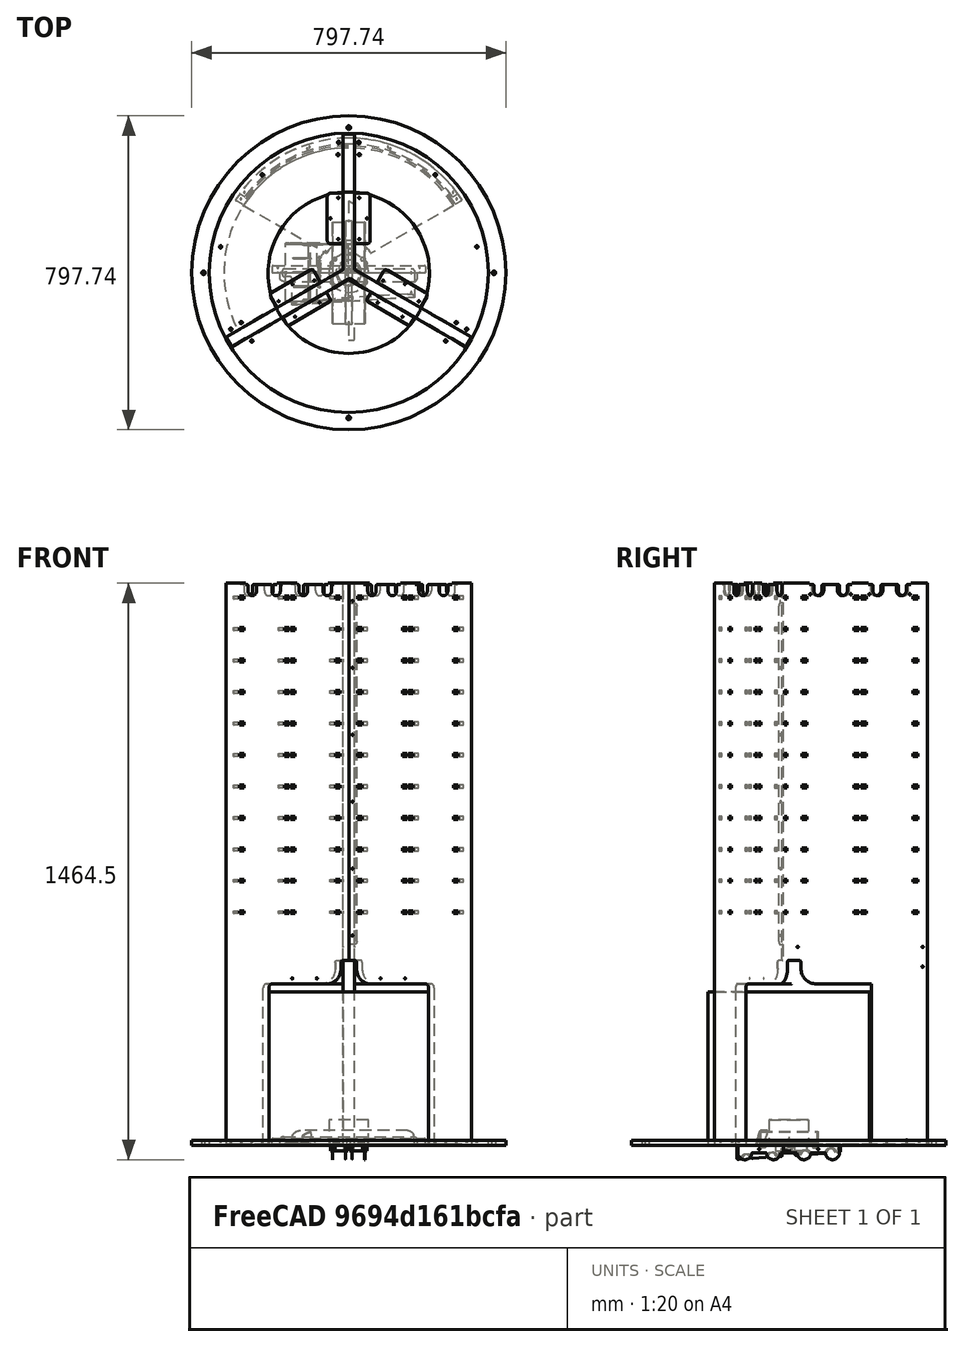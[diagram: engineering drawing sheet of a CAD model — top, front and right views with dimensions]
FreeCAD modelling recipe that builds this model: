
FCSTD DOCUMENT  (FreeCAD 0.21R32532 (Git))
Label: composit_full_size
License: All rights reserved
LicenseURL: http://en.wikipedia.org/wiki/All_rights_reserved
objects: Sketcher::SketchObject×64, PartDesign::Pocket×50, PartDesign::CoordinateSystem×29, PartDesign::Mirrored×20, PartDesign::Body×18, PartDesign::PolarPattern×17, PartDesign::Plane×14, PartDesign::SubShapeBinder×14, PartDesign::FeaturePython×12, PartDesign::Pad×11, PartDesign::MultiTransform×11, PartDesign::LinearPattern×7, Spreadsheet::Sheet×5, PartDesign::Line×4, App::DocumentObjectGroup×2, PartDesign::Fillet×2, Part::Feature×1, PartDesign::FeatureBase×1, PartDesign::Point×1, PartDesign::ShapeBinder×1, +2 more types
note: 344 computed .brp shape members not serialized (recipe doc carries the construction recipe); baked Part::Feature solids carry a one-line shape summary decoded from their .brp
EXTERNAL_REF file=composit_stand2_reserve.FCStd obj=Body_2

FEATURE [Sketcher::SketchObject] Sketch
  FullyConstrained = true
  MapMode = 5
  Support = -> [XY_Plane]
  expr: Constraints[29] = <<main>>.end_face_width
  expr: Constraints[32] = <<main>>.work_plane_width
  sketch-geometry (18):
    g0: LineSegment StartX=14.5 StartY=8.37158 StartZ=0 EndX=-14.5 EndY=8.37158 EndZ=0
    g1: LineSegment StartX=-14.5 StartY=8.37158 StartZ=0 EndX=-14.5 EndY=351.872 EndZ=0
    g2: LineSegment StartX=-14.5 StartY=351.872 StartZ=0 EndX=14.5 EndY=351.872 EndZ=0
    g3: LineSegment StartX=14.5 StartY=351.872 StartZ=0 EndX=14.5 EndY=8.37158 EndZ=0
    g4: LineSegment StartX=-14.5 StartY=8.37158 StartZ=0 EndX=-311.98 EndY=-163.378 EndZ=0
    g5: LineSegment StartX=-311.98 StartY=-163.378 StartZ=0 EndX=-297.48 EndY=-188.493 EndZ=0
    g6: LineSegment StartX=-297.48 StartY=-188.493 StartZ=0 EndX=3 EndY=-15.0111 EndZ=0
    g7: LineSegment StartX=0 StartY=-16.7432 StartZ=0 EndX=-14.5 EndY=8.37158 EndZ=0
    g8: LineSegment StartX=14.5 StartY=8.37158 StartZ=0 EndX=311.98 EndY=-163.378 EndZ=0
    g9: LineSegment StartX=311.98 StartY=-163.378 StartZ=0 EndX=297.48 EndY=-188.493 EndZ=0
    g10: LineSegment StartX=0 StartY=-16.7432 StartZ=0 EndX=14.5 EndY=8.37158 EndZ=0
    g11: LineSegment StartX=-14.5 StartY=8.37158 StartZ=0 EndX=0 EndY=0 EndZ=0
    g12: LineSegment StartX=0 StartY=0 StartZ=0 EndX=0 EndY=-16.7432 EndZ=0
    g13: LineSegment StartX=0 StartY=0 StartZ=0 EndX=14.5 EndY=8.37158 EndZ=0
    g14: LineSegment StartX=297.48 StartY=-188.493 StartZ=0 EndX=0.216506 EndY=-16.8682 EndZ=0
    g15: LineSegment StartX=0.216506 StartY=-16.8682 StartZ=0 EndX=0 EndY=-16.7432 EndZ=0
    g16: LineSegment StartX=3 StartY=-15.0111 StartZ=0 EndX=20.3205 EndY=-25.0111 EndZ=0
    g17: LineSegment StartX=0 StartY=0 StartZ=0 EndX=-5.75 EndY=-9.95929 EndZ=0
  constraints (54):
    c: Coincident(g0,g1)
    c: Coincident(g1,g2)
    c: Coincident(g2,g3)
    c: Coincident(g3,g0)
    c: Horizontal(g0)
    c: Horizontal(g2)
    c: Vertical(g1)
    c: Vertical(g3)
    c: Coincident(g4,g5)
    c: Coincident(g7,g4)
    c: Parallel(g4,g6)
    c: Parallel(g5,g7)
    c: Coincident(g8,g9)
    c: Coincident(g9,g14)
    c: Coincident(g15,g10)
    c: Coincident(g10,g8)
    c: Perpendicular(g5,g4)
    c: Coincident(g4,g0)
    c: Coincident(g8,g0)
    c: Parallel(g10,g9)
    c: Perpendicular(g8,g10)
    c: Equal(g7,g10)
    c: Equal(g10,g0)
    c: Coincident(g11,g1)
    c: Coincident(g11,g-1)
    c: Coincident(g12,g11)
    c: Coincident(g13,g11)
    c: Coincident(g13,g3)
    c: Equal(g12,g13)
    c: DistanceX(g2,g2) = 29
    c: Equal(g4,g1)
    c: DistanceY(g12,g12) = 16.7432  'petal_connection_distance'
    c: DistanceY(g3,g3) = 343.5
    c: DistanceY(g3) = 8.37158  'petal_offset'
    c: Distance(g2,g11) = 352.17  'max_r'
    c: Coincident(g14,g15)
    c: Parallel(g14,g8)
    c: Parallel(g15,g8)
    c: Equal(g8,g3)
    c: Distance(g14,g15) = 0.25
    c: Coincident(g7,g12)
    c: Coincident(g15,g7)
    c: PointOnObject(g15,g-2)
    c: Coincident(g6,g5)
    c: PointOnObject(g7,g6)
    c: Distance(g6,g14) = 3
    c: Coincident(g16,g6)
    c: Parallel(g16,g14)
    c: Distance(g16) = 20
    c: Coincident(g17,g11)
    c: Perpendicular(g17,g16)
    c: PointOnObject(g17,g16)
    c: Distance(g16,g17) = 30.1036  'overlap_from_origin'
    c: Distance(g6,g7) = 3.4641  'overlap_proj_thickness'
FEATURE [PartDesign::FeaturePython] BaseBend  # WARN: FeaturePython — macro-defined, semantics opaque (R4)
  BendSide = 0
  BendSketch = -> Sketch
  MidPlane = false
  Reverse = false
  length = 1428
  radius = 0.1
  thickness = 0.3
  expr: length = <<main>>.total_length
  expr: radius = <<main>>.bend_r
  expr: thickness = 0.3
FEATURE [Spreadsheet::Sheet] Spreadsheet  label="module"
  cells = B2(module_width)==148 mm; B3(module_height)==160 mm; B4(module_fixture_distance_x)==132 mm; C4(module_fixture_distance_y)==80 mm; B5(module_hole_x)==13 mm; B6(module_hole_y)==7 mm
FEATURE [Spreadsheet::Sheet] Spreadsheet001  label="main"
  cells = B2(work_plane_width)==27.5 mm + <<module>>.module_width * 2 + 20 mm; C2(modules_center_offset)==<<module>>.module_width + 25 mm; D2(rivet_d)==3.4 mm; E2(pillar_offset)==398 mm; F2(plexiglass_shield_bottom_offset)==471 mm; B3(work_plane_height)==basin_height + <<module>>.module_fixture_distance_y * number_of_modules + <<module>>.module_height; C3(work_plane_height_middle)==basin_height + work_plane_height / 2; D3(planes_fix_holes_distance)==130 mm; B4(end_face_width)==29 mm; C4(inner_width)==end_face_width - thickness * 2; D4(gutter_fix_holes_distance)==51 mm; B5(basin_height)==410 mm; B6(thickness)==3 mm; C6(al_thickness)==0.3 mm; D6(number_of_modules)=11; E6(modules_array_height)==<<module>>.module_height + (number_of_modules - 1) * <<module>>.module_fixture_distance_y; F6(distance_farest_droppers)==<<dropper>>.distance_between_droppers2 + <<dropper>>.d + 20 mm + modules_offset_x; B7(total_length)==basin_height + distance_basin_cutout_modules_bottom + modules_array_height + distance_gutter_holes_modules_top + distance_gutter_holes_dropper_cutout + <<dropper>>.center_height_offset; D7(distance_basin_cutout_modules_bottom)==22 mm; B8(bend_r)==0.1 mm; D8(distance_gutter_holes_modules_top)==8 mm; B9(module_distance_x)==2 mm; D9(distance_gutter_holes_dropper_cutout)==9 mm; B10(modules_offset_x)==<<module>>.module_width + module_distance_x; D10(modules_centres_dictance_x)==module_distance_x + <<module>>.module_width; B11(plexiglass_offset)==10 mm; D11(leg_width)==110 mm
FEATURE [Spreadsheet::Sheet] Spreadsheet002  label="dropper"
  cells = B2(d)==23.25 mm; B3(fixture_d)=; B4(center_height_offset)==19 mm; B5(distance_between_droppers1)==60 mm; C5(distance_between_droppers2)==70 mm
FEATURE [Spreadsheet::Sheet] Spreadsheet003  label="gutter"
  cells = B2(length)==300 mm; C2(plane_middle)==60 mm; B3(bend_angle)==4 °; B4(high_edge_length)==30 mm; B5(low_edge_length)==20 mm
FEATURE [Part::Feature] Part__Feature  label="module002"
  shape: bbox 170 x 148 x 41.12 mm, 715 faces (baked)
FEATURE [PartDesign::CoordinateSystem] LCS_0
  AttacherType = Attacher::AttachEngine3D
  MapMode = 2
  Support = -> [X_Axis001]
FEATURE [PartDesign::FeatureBase] BaseFeature
  BaseFeature = -> Part__Feature
  Placement = pos=(2e-15,0.749157,-0.233873) rot=(0,0,1;0rad)
FEATURE [PartDesign::Line] DatumLine
  AttacherType = Attacher::AttachEngineLine
  Length = 20
  MapMode = 29
  Placement = pos=(2e-15,0.749157,-0.233873) rot=(0,0.707107,0.707107;3.14159rad)
  ResizeMode = 0
  Support = -> [BaseFeature]
FEATURE [PartDesign::Body] module_body
  BaseFeature = -> Part__Feature
  Group = -> [BaseFeature,LCS_0,DatumLine]
  Origin = -> Origin001
  Tip = -> BaseFeature
FEATURE [Sketcher::SketchObject] Sketch002  label="cover_holder_corner"
  FullyConstrained = true
  MapMode = 5
  Placement = pos=(0,0,0) rot=(0.57735,0.57735,0.57735;2.0944rad)
  Support = -> [YZ_Plane]
  expr: Constraints[8] = <<main>>.basin_height
  sketch-geometry (4):
    g0: LineSegment StartX=71 StartY=360 StartZ=0 EndX=71 EndY=410 EndZ=0
    g1: LineSegment StartX=71 StartY=410 StartZ=0 EndX=205 EndY=410 EndZ=0
    g2: LineSegment StartX=205 StartY=410 StartZ=0 EndX=205 EndY=360 EndZ=0
    g3: LineSegment StartX=205 StartY=360 StartZ=0 EndX=71 EndY=360 EndZ=0
  constraints (13):
    c: Coincident(g0,g1)
    c: Coincident(g1,g2)
    c: Coincident(g2,g3)
    c: Coincident(g3,g0)
    c: Horizontal(g1)
    c: Horizontal(g3)
    c: Vertical(g0)
    c: Vertical(g2)
    c: DistanceY(g1) = 410
    c: DistanceY(g2,g2) = 50
    c: DistanceX(g0) = 71  'offset'
    c: DistanceX(g1) = 205
    c: DistanceX(g3,g3) = 134  'length'
FEATURE [PartDesign::Pocket] Pocket001
  BaseFeature = -> BaseBend
  Direction = (-1,2e-16,-3e-16)
  Length = 29
  Length2 = 5
  Midplane = true
  Profile = -> Sketch002
  ReferenceAxis = -> Sketch002 [N_Axis]
  Type = 0
  expr: Length = <<main>>.end_face_width
FEATURE [PartDesign::PolarPattern] PolarPattern
  Angle = 360
  Axis = -> Z_Axis
  BaseFeature = -> Pocket001
  Occurrences = 3
  Originals = -> [Pocket001]
  Refine = true
FEATURE [PartDesign::Point] DatumPoint
  AttacherType = Attacher::AttachEnginePoint
  AttachmentOffset = pos=(0,8.37158,0) rot=(0,0,1;0rad)
  MapMode = 32
  Placement = pos=(0,8.37158,0) rot=(0,0,1;0rad)
  Support = -> [XY_Plane]
  expr: .AttachmentOffset.Base.y = Sketch.Constraints.petal_offset
FEATURE [PartDesign::CoordinateSystem] Local_CS
  AttacherType = Attacher::AttachEngine3D
  AttachmentOffset = pos=(0,173,0) rot=(0,0,1;0rad)
  MapMode = 1
  Placement = pos=(0,181.372,0) rot=(0,0,1;0rad)
  Support = -> [DatumPoint]
  expr: .AttachmentOffset.Base.y = <<module>>.module_width + 25 mm
FEATURE [PartDesign::CoordinateSystem] Local_CS001
  AttacherType = Attacher::AttachEngine3D
  AttachmentOffset = pos=(0,0,410) rot=(0,0,1;0rad)
  MapMode = 5
  Placement = pos=(0,181.372,410) rot=(0,0,1;0rad)
  Support = -> [Local_CS]
  expr: .AttachmentOffset.Base.z = <<main>>.basin_height
FEATURE [PartDesign::Plane] DatumPlane
  Length = 717.412
  MapMode = 4
  Placement = pos=(0,181.372,410) rot=(0.57735,0.57735,0.57735;2.0944rad)
  ResizeMode = 0
  Support = -> [Local_CS001]
  Width = 1630.19
FEATURE [PartDesign::PolarPattern] PolarPattern001
  Angle = 360
  Axis = -> Z_Axis
  Occurrences = 3
FEATURE [PartDesign::CoordinateSystem] Local_CS002
  AttacherType = Attacher::AttachEngine3D
  AttachmentOffset = pos=(0,0,1428) rot=(0,0,1;0rad)
  MapMode = 5
  Placement = pos=(0,181.372,1428) rot=(0,0,1;0rad)
  Support = -> [Local_CS]
  expr: .AttachmentOffset.Base.z = <<main>>.total_length
FEATURE [PartDesign::CoordinateSystem] Local_CS003
  AttacherType = Attacher::AttachEngine3D
  AttachmentOffset = pos=(0,-75,0) rot=(0,0,1;0rad)
  MapMode = 5
  Placement = pos=(0,106.372,1428) rot=(0,0,1;0rad)
  Support = -> [Local_CS002]
  expr: .AttachmentOffset.Base.y = -<<main>>.module_distance_x / 2 - <<module>>.module_width / 2
FEATURE [PartDesign::Plane] DatumPlane001
  Length = 814.054
  MapMode = 3
  Placement = pos=(0,106.372,1428) rot=(1,0,0;1.5708rad)
  ResizeMode = 0
  Support = -> [Local_CS003]
  Width = 1643.39
FEATURE [PartDesign::Plane] DatumPlane002
  Length = 814.054
  MapMode = 3
  Placement = pos=(0,181.372,1428) rot=(1,0,0;1.5708rad)
  ResizeMode = 0
  Support = -> [Local_CS002]
  Width = 1643.39
FEATURE [PartDesign::Plane] DatumPlane003
  Length = 717.412
  MapMode = 4
  Placement = pos=(0,106.372,1428) rot=(0.57735,0.57735,0.57735;2.0944rad)
  ResizeMode = 0
  Support = -> [Local_CS003]
  Width = 1630.19
FEATURE [Sketcher::SketchObject] Sketch003
  AttachmentOffset = pos=(-66,-36,0) rot=(0,0,1;0rad)
  FullyConstrained = true
  MapMode = 5
  Placement = pos=(0,40.3716,1392) rot=(0.57735,0.57735,0.57735;2.0944rad)
  Support = -> [DatumPlane003]
  expr: .AttachmentOffset.Base.x = -<<module>>.module_fixture_distance_x / 2
  expr: .AttachmentOffset.Base.y = Sketch005.AttachmentOffset.Base.y - <<main>>.distance_gutter_holes_modules_top
  expr: Constraints[10] = <<module>>.module_hole_x
  expr: Constraints[11] = <<module>>.module_hole_y
  sketch-geometry (5):
    g0: LineSegment StartX=-6.5 StartY=-3.5 StartZ=0 EndX=-6.5 EndY=3.5 EndZ=0
    g1: LineSegment StartX=-6.5 StartY=3.5 StartZ=0 EndX=6.5 EndY=3.5 EndZ=0
    g2: LineSegment StartX=6.5 StartY=3.5 StartZ=0 EndX=6.5 EndY=-3.5 EndZ=0
    g3: LineSegment StartX=6.5 StartY=-3.5 StartZ=0 EndX=-6.5 EndY=-3.5 EndZ=0
    g4: GeomPoint X=0 Y=0 Z=0
  constraints (12):
    c: Coincident(g0,g1)
    c: Coincident(g1,g2)
    c: Coincident(g2,g3)
    c: Coincident(g3,g0)
    c: Horizontal(g1)
    c: Horizontal(g3)
    c: Vertical(g0)
    c: Vertical(g2)
    c: Symmetric(g1,g0,g4)
    c: Coincident(g4,g-1)
    c: DistanceX(g1,g1) = 13
    c: DistanceY(g2,g2) = 7
FEATURE [PartDesign::LinearPattern] LinearPattern
  Direction = -> Sketch003 [H_Axis]
  Length = 132
  Occurrences = 2
  expr: Length = <<module>>.module_fixture_distance_x
FEATURE [PartDesign::LinearPattern] LinearPattern001
  Direction = -> Sketch003 [H_Axis]
  Length = 150
  Occurrences = 2
  expr: Length = <<module>>.module_width + <<main>>.module_distance_x
FEATURE [PartDesign::LinearPattern] LinearPattern002
  Direction = -> Sketch003 [V_Axis]
  Length = 800
  Occurrences = 11
  Reversed = true
  expr: Length = <<module>>.module_fixture_distance_y * (Occurrences - 1)
  expr: Occurrences = <<main>>.number_of_modules
FEATURE [Sketcher::SketchObject] Sketch004
  AttachmentOffset = pos=(-35,-19,0) rot=(0,0,1;0rad)
  FullyConstrained = true
  MapMode = 5
  Placement = pos=(0,71.3716,1409) rot=(0.57735,0.57735,0.57735;2.0944rad)
  Support = -> [DatumPlane003]
  expr: .AttachmentOffset.Base.x = -<<dropper>>.distance_between_droppers2 / 2
  expr: .AttachmentOffset.Base.y = -<<dropper>>.center_height_offset
  expr: .Constraints.d = <<dropper>>.d + 2 mm
  expr: Constraints[10] = <<dropper>>.center_height_offset
  sketch-geometry (4):
    g0: ArcOfCircle CenterX=0 CenterY=0 CenterZ=0 NormalX=0 NormalY=0 NormalZ=1 AngleXU=0 Radius=12.625 StartAngle=3.14159 EndAngle=6.28319
    g1: LineSegment StartX=-12.625 StartY=19 StartZ=0 EndX=-12.625 EndY=0 EndZ=0
    g2: LineSegment StartX=12.625 StartY=-3.1e-15 StartZ=0 EndX=12.625 EndY=19 EndZ=0
    g3: LineSegment StartX=-12.625 StartY=19 StartZ=0 EndX=12.625 EndY=19 EndZ=0
  constraints (11):
    c: PointOnObject(g0,g-2)
    c: Tangent(g2,g0) = -1.5708
    c: Tangent(g1,g0) = -1.5708
    c: Vertical(g2)
    c: Vertical(g1)
    c: Horizontal(g3)
    c: PointOnObject(g0,g-1)
    c: Diameter(g0) = 25.25  'd'
    c: Coincident(g1,g3)
    c: Coincident(g2,g3)
    c: DistanceY(g2) = 19
FEATURE [PartDesign::SubShapeBinder] Binder
  BindCopyOnChange = 0
  BindMode = 0
  ClaimChildren = false
  Context = -> Body [Binder.]
  Fuse = false
  MakeFace = true
  OffsetFill = false
  OffsetIntersection = false
  OffsetJoinType = 0
  OffsetOpenResult = false
  PartialLoad = false
  Placement = pos=(0,5,0) rot=(0,0,1;0rad)
  Relative = true
  Support = -> [Sketch004]
  _Version = 2
  expr: .Placement.Base.y = (<<dropper>>.distance_between_droppers2 - <<dropper>>.distance_between_droppers1) / 2
FEATURE [PartDesign::Mirrored] Mirrored
  MirrorPlane = -> DatumPlane001
FEATURE [PartDesign::Mirrored] Mirrored001
  MirrorPlane = -> DatumPlane002
FEATURE [PartDesign::PolarPattern] PolarPattern002
  Angle = 360
  Axis = -> Z_Axis
  Occurrences = 3
FEATURE [Sketcher::SketchObject] Sketch007
  AttachmentOffset = pos=(-35,-3.5,0) rot=(0,0,1;0rad)
  FullyConstrained = true
  MapMode = 5
  Placement = pos=(0,71.3716,1424.5) rot=(0.57735,0.57735,0.57735;2.0944rad)
  Support = -> [DatumPlane003]
  expr: .AttachmentOffset.Base.x = Sketch004.AttachmentOffset.Base.x
  expr: .AttachmentOffset.Base.y = -Sketch008.Constraints.height
  expr: Constraints[18] = Sketch004.Constraints.d
  sketch-geometry (8):
    g0: ArcOfCircle CenterX=15.125 CenterY=-2.5 CenterZ=0 NormalX=0 NormalY=0 NormalZ=1 AngleXU=0 Radius=2.5 StartAngle=1.57079 EndAngle=3.14159
    g1: LineSegment StartX=-15.125 StartY=0 StartZ=0 EndX=-12.625 EndY=0 EndZ=0
    g2: LineSegment StartX=-12.625 StartY=-2.5 StartZ=0 EndX=-12.625 EndY=0 EndZ=0
    g3: LineSegment StartX=12.625 StartY=-2.5 StartZ=0 EndX=12.625 EndY=0 EndZ=0
    g4: LineSegment StartX=12.625 StartY=0 StartZ=0 EndX=15.125 EndY=-2.9527e-11 EndZ=0
    g5: LineSegment StartX=-12.625 StartY=0 StartZ=0 EndX=0 EndY=0 EndZ=0
    g6: LineSegment StartX=0 StartY=0 StartZ=0 EndX=12.625 EndY=0 EndZ=0
    g7: ArcOfCircle CenterX=-15.125 CenterY=-2.5 CenterZ=0 NormalX=0 NormalY=0 NormalZ=1 AngleXU=0 Radius=2.5 StartAngle=0 EndAngle=1.5708
  constraints (23):
    c: PointOnObject(g0,g-1)
    c: PointOnObject(g1,g-1)
    c: Coincident(g2,g1)
    c: Coincident(g3,g0)
    c: PointOnObject(g3,g-1)
    c: Vertical(g3)
    c: Tangent(g3,g0)
    c: Coincident(g4,g3)
    c: Coincident(g4,g0)
    c: Tangent(g4,g0)
    c: Vertical(g2)
    c: Diameter(g0) = 5
    c: Coincident(g5,g1)
    c: Horizontal(g5)
    c: Coincident(g6,g5)
    c: Coincident(g6,g3)
    c: Equal(g5,g6)
    c: PointOnObject(g5,g-2)
    c: DistanceX(g1,g3) = 25.25
    c: Horizontal(g1)
    c: Tangent(g7,g1) = 1.5708
    c: Tangent(g7,g2) = -1.5708
    c: Equal(g7,g0)
FEATURE [PartDesign::SubShapeBinder] Binder001
  BindCopyOnChange = 0
  BindMode = 0
  ClaimChildren = false
  Context = -> Body [Binder001.]
  Fuse = false
  MakeFace = true
  OffsetFill = false
  OffsetIntersection = false
  OffsetJoinType = 0
  OffsetOpenResult = false
  PartialLoad = false
  Placement = pos=(0,5,0) rot=(0,0,1;0rad)
  Relative = true
  Support = -> [Sketch007]
  _Version = 2
  expr: .Placement.Base.y = Binder.Placement.Base.y
FEATURE [Sketcher::SketchObject] Sketch008
  FullyConstrained = true
  MapMode = 5
  Placement = pos=(0,106.372,1428) rot=(0.57735,0.57735,0.57735;2.0944rad)
  Support = -> [DatumPlane003]
  expr: Constraints[10] = 108.4 / 2
  sketch-geometry (5):
    g0: LineSegment StartX=0 StartY=0 StartZ=0 EndX=-54.2 EndY=0 EndZ=0
    g1: LineSegment StartX=-54.2 StartY=0 StartZ=0 EndX=-54.2 EndY=-3.5 EndZ=0
    g2: LineSegment StartX=-54.2 StartY=-3.5 StartZ=0 EndX=0 EndY=-3.5 EndZ=0
    g3: LineSegment StartX=0 StartY=-3.5 StartZ=0 EndX=0 EndY=0 EndZ=0
    g4: GeomPoint X=54.2 Y=0 Z=0
  constraints (13):
    c: Coincident(g0,g1)
    c: Coincident(g1,g2)
    c: Coincident(g2,g3)
    c: Coincident(g3,g0)
    c: Horizontal(g0)
    c: Horizontal(g2)
    c: Vertical(g1)
    c: Vertical(g3)
    c: Coincident(g0,g-1)
    c: DistanceY(g1,g1) = 3.5  'height'
    c: DistanceX(g0,g0) = 54.2
    c: Symmetric(g4,g0,g-2)
    c: DistanceX(g0,g4) = 108.4
FEATURE [Sketcher::SketchObject] Sketch009
  FullyConstrained = true
  MapMode = 5
  Placement = pos=(0,0,0) rot=(0,0.707107,0.707107;3.14159rad)
  Support = -> [XZ_Plane003]
  expr: .Constraints.high_side_length = -(<<gutter>>.low_edge_length + <<main>>.distance_farest_droppers * tan(<<gutter>>.bend_angle))
  expr: Constraints[11] = <<main>>.end_face_width - <<main>>.thickness * 4
  sketch-geometry (5):
    g0: LineSegment StartX=-8.5 StartY=-38.4082 StartZ=0 EndX=-8.5 EndY=0 EndZ=0
    g1: LineSegment StartX=-8.5 StartY=0 StartZ=0 EndX=8.5 EndY=0 EndZ=0
    g2: LineSegment StartX=8.5 StartY=0 StartZ=0 EndX=8.5 EndY=-38.4082 EndZ=0
    g3: LineSegment StartX=8.5 StartY=-38.4082 StartZ=0 EndX=-8.5 EndY=-38.4082 EndZ=0
    g4: GeomPoint X=0 Y=-19.2041 Z=0
  constraints (13):
    c: Coincident(g0,g1)
    c: Coincident(g1,g2)
    c: Coincident(g2,g3)
    c: Coincident(g3,g0)
    c: Horizontal(g1)
    c: Horizontal(g3)
    c: Vertical(g0)
    c: Vertical(g2)
    c: Symmetric(g1,g0,g4)
    c: PointOnObject(g4,g-2)
    c: PointOnObject(g1,g-1)
    c: DistanceX(g0,g1) = 17
    c: DistanceY(g2) = -38.4082  'high_side_length'
FEATURE [PartDesign::FeaturePython] BaseBend001  # WARN: FeaturePython — macro-defined, semantics opaque (R4)
  BendSide = 1
  BendSketch = -> Sketch009
  MidPlane = true
  Reverse = false
  length = 263.25
  radius = 0.1
  thickness = 0.3
  expr: length = <<main>>.distance_farest_droppers
  expr: radius = <<main>>.bend_r
  expr: thickness = <<main>>.al_thickness
FEATURE [Sketcher::SketchObject] Sketch010
  AttachmentOffset = pos=(0,-38.4082,0) rot=(0,0,1;0rad)
  FullyConstrained = true
  MapMode = 5
  Placement = pos=(8.5e-15,-8.5e-15,-38.4082) rot=(0.57735,0.57735,0.57735;2.0944rad)
  Support = -> [YZ_Plane003]
  expr: .AttachmentOffset.Base.y = Sketch009.Constraints.high_side_length
  expr: Constraints[12] = <<gutter>>.bend_angle
  expr: Constraints[6] = <<main>>.distance_farest_droppers
  sketch-geometry (10):
    g0: LineSegment StartX=-128.951 StartY=0.187012 StartZ=0 EndX=129.299 EndY=18.2456 EndZ=0
    g1: ArcOfCircle CenterX=-129.125 CenterY=2.68092 CenterZ=0 NormalX=0 NormalY=0 NormalZ=1 AngleXU=0 Radius=2.5 StartAngle=3.14159 EndAngle=4.7822
    g2: LineSegment StartX=131.625 StartY=20.7395 StartZ=0 EndX=131.625 EndY=0 EndZ=0
    g3: LineSegment StartX=-131.625 StartY=0 StartZ=0 EndX=-131.625 EndY=2.68092 EndZ=0
    g4: LineSegment StartX=131.625 StartY=0 StartZ=0 EndX=0 EndY=0 EndZ=0
    g5: LineSegment StartX=0 StartY=0 StartZ=0 EndX=-131.625 EndY=0 EndZ=0
    g6: GeomPoint X=-131.625 Y=0 Z=0
    g7: GeomPoint X=131.625 Y=20.7395 Z=0
    g8: ArcOfCircle CenterX=129.125 CenterY=20.7395 CenterZ=0 NormalX=0 NormalY=0 NormalZ=1 AngleXU=0 Radius=2.5 StartAngle=4.7822 EndAngle=6.28319
    g9: GeomPoint X=131.625 Y=18.4082 Z=0
  constraints (25):
    c: Vertical(g2)
    c: Coincident(g4,g2)
    c: Coincident(g3,g5)
    c: Vertical(g3)
    c: Tangent(g3,g1) = 1.5708
    c: Tangent(g1,g0) = -1.5708
    c: DistanceX(g5,g2) = 263.25
    c: Coincident(g4,g5)
    c: Horizontal(g4)
    c: Horizontal(g5)
    c: Equal(g5,g4)
    c: PointOnObject(g4,g-2)
    c: Angle(g-1,g0) = 0.0698132
    c: PointOnObject(g6,g3)
    c: PointOnObject(g6,g0)
    c: PointOnObject(g6,g-1)
    c: Diameter(g1) = 5
    c: PointOnObject(g4,g-1)
    c: Coincident(g8,g7)
    c: Tangent(g2,g8) = 1.5708
    c: Equal(g8,g1)
    c: Tangent(g8,g0) = -1.5708
    c: PointOnObject(g9,g2)
    c: PointOnObject(g9,g0)
    c: DistanceY(g9) = 18.4082
FEATURE [PartDesign::Pocket] Pocket009
  BaseFeature = -> BaseBend001
  Direction = (-1,2e-16,-3e-16)
  Length = 5
  Length2 = 5
  Midplane = true
  Profile = -> Sketch010
  ReferenceAxis = -> Sketch010 [N_Axis]
  Type = 1
FEATURE [PartDesign::CoordinateSystem] Local_CS005
  AttacherType = Attacher::AttachEngine3D
  AttachmentOffset = pos=(0,0,-29.2041) rot=(1,0,0;0.069813rad)
  MapMode = 5
  Placement = pos=(0,0,-29.2041) rot=(1,0,0;0.069813rad)
  Support = -> [XY_Plane003]
  expr: .AttachmentOffset.Base.z = (Sketch009.Constraints.high_side_length + <<gutter>>.low_edge_length) / 2 - <<gutter>>.low_edge_length
  expr: .AttachmentOffset.Rotation.Roll = <<gutter>>.bend_angle
FEATURE [PartDesign::CoordinateSystem] Local_CS006
  AttacherType = Attacher::AttachEngine3D
  AttachmentOffset = pos=(0,75,0) rot=(0,0,1;0rad)
  MapMode = 5
  Placement = pos=(0,74.8173,-23.9724) rot=(1,0,0;0.069813rad)
  Support = -> [Local_CS005]
  expr: .AttachmentOffset.Base.y = <<main>>.module_distance_x / 2 + <<module>>.module_width / 2
FEATURE [PartDesign::Plane] DatumPlane004
  Length = 305.115
  MapMode = 4
  Placement = pos=(0,74.8173,-23.9724) rot=(0.590324,0.550486,0.590324;2.13516rad)
  ResizeMode = 0
  Support = -> [Local_CS006]
  Width = 112.246
FEATURE [Sketcher::SketchObject] Sketch037
  AttachmentOffset = pos=(30,0,0) rot=(0,0,1;0rad)
  FullyConstrained = true
  MapMode = 5
  Placement = pos=(-5e-15,104.744,-21.8797) rot=(0.590324,0.550486,0.590324;2.13516rad)
  Support = -> [DatumPlane004]
  expr: .AttachmentOffset.Base.x = <<dropper>>.distance_between_droppers1 / 2
  expr: Constraints[10] = <<dropper>>.d
  sketch-geometry (12):
    g0: LineSegment StartX=0 StartY=13.625 StartZ=0 EndX=1 EndY=13.625 EndZ=0
    g1: ArcOfCircle CenterX=1 CenterY=2 CenterZ=0 NormalX=0 NormalY=0 NormalZ=1 AngleXU=0 Radius=11.625 StartAngle=0.26174 EndAngle=1.5708
    g2: ArcOfCircle CenterX=17.127 CenterY=0 CenterZ=0 NormalX=0 NormalY=0 NormalZ=1 AngleXU=0 Radius=3 StartAngle=0.25268 EndAngle=1.29556
    g3: LineSegment StartX=12.9232 StartY=4.30451 StartZ=0 EndX=17.9423 EndY=2.88708 EndZ=0
    g4: LineSegment StartX=0 StartY=13.625 StartZ=0 EndX=0 EndY=0 EndZ=0
    g5: LineSegment StartX=0 StartY=0 StartZ=0 EndX=21 EndY=0 EndZ=0
    g6: ArcOfCircle CenterX=21 CenterY=1 CenterZ=0 NormalX=0 NormalY=0 NormalZ=1 AngleXU=0 Radius=1 StartAngle=3.39427 EndAngle=4.71239
    g7: ArcOfCircle CenterX=13.195 CenterY=5.26687 CenterZ=0 NormalX=0 NormalY=0 NormalZ=1 AngleXU=0 Radius=1 StartAngle=3.40333 EndAngle=4.43715
    g8: ArcOfCircle CenterX=18.7577 CenterY=5.77416 CenterZ=0 NormalX=0 NormalY=0 NormalZ=1 AngleXU=0 Radius=3 StartAngle=4.43715 EndAngle=4.71239
    g9: LineSegment StartX=18.7577 StartY=2.77416 StartZ=0 EndX=35 EndY=2.77416 EndZ=0
    g10: LineSegment StartX=35 StartY=2.77416 StartZ=0 EndX=35 EndY=0 EndZ=0
    g11: LineSegment StartX=35 StartY=0 StartZ=0 EndX=21 EndY=0 EndZ=0
  constraints (33):
    c: PointOnObject(g0,g-2)
    c: Horizontal(g0)
    c: PointOnObject(g2,g-1)
    c: Tangent(g3,g2) = 1.5708
    c: Tangent(g1,g0) = 1.5708
    c: Coincident(g4,g0)
    c: Coincident(g4,g-1)
    c: Coincident(g5,g4)
    c: Diameter(g2) = 6
    c: Angle(g3,g-1) = 0.275238
    c: Diameter(g1) = 23.25
    c: Distance(g0) = 1
    c: Horizontal(g5)
    c: Tangent(g6,g5) = -1.5708
    c: Tangent(g6,g2) = 1.5708
    c: Diameter(g6) = 2
    c: Distance(g5) = 21
    c: Tangent(g3,g7) = -1.5708
    c: Tangent(g1,g7) = 1.5708
    c: Diameter(g7) = 2
    c: DistanceY(g2) = 2.88708  'arc_height'
    c: Horizontal(g9)
    c: Coincident(g10,g9)
    c: Vertical(g10)
    c: Coincident(g11,g10)
    c: Coincident(g11,g5)
    c: Equal(g2,g8)
    c: Tangent(g8,g3) = -1.5708
    c: Tangent(g8,g9) = -1.5708
    c: DistanceX(g4,g10) = 35
    c: Horizontal(g11)
    c: DistanceY(g9) = 2.77416  'cut_height'
    c: DistanceY(g1) = 2
FEATURE [PartDesign::ShapeBinder] ShapeBinder
  AttacherType = Attacher::AttachEngine3D
  AttachmentOffset = pos=(35,0,0) rot=(0,0,1;0rad)
  MapMode = 4
  Placement = pos=(-2e-15,104.744,-21.8797) rot=(0.590324,0.550486,0.590324;2.13516rad)
  TraceSupport = false
  expr: .AttachmentOffset.Base.x = <<dropper>>.distance_between_droppers2 / 2
FEATURE [PartDesign::Pocket] Pocket010
  BaseFeature = -> Pocket009
  Direction = (-1,0,0)
  Length = 5
  Length2 = 5
  Profile = -> Sketch037
  ReferenceAxis = -> Sketch037 [N_Axis]
  Type = 1
FEATURE [PartDesign::Mirrored] Mirrored002
  MirrorPlane = -> Sketch037 [V_Axis]
FEATURE [PartDesign::LinearPattern] LinearPattern004
  Direction = -> Sketch037 [H_Axis]
  Length = 60
  Occurrences = 2
  Reversed = true
  expr: Length = <<dropper>>.distance_between_droppers1
FEATURE [PartDesign::LinearPattern] LinearPattern005
  Direction = -> Sketch037 [H_Axis]
  Length = 150
  Occurrences = 2
  Reversed = true
  expr: Length = <<main>>.modules_offset_x
FEATURE [PartDesign::Line] DatumLine001
  AttacherType = Attacher::AttachEngineLine
  Length = 20
  MapMode = 17
  Placement = pos=(0,4e-16,-29.2041) rot=(1,0,0;1.64061rad)
  ResizeMode = 0
  Support = -> [Local_CS005]
FEATURE [PartDesign::LinearPattern] LinearPattern006
  Direction = -> DatumLine001
  Length = 70
  Occurrences = 2
  expr: Length = <<dropper>>.distance_between_droppers2
FEATURE [PartDesign::LinearPattern] LinearPattern007
  Direction = -> DatumLine001
  Length = 150
  Occurrences = 2
  expr: Length = <<main>>.modules_offset_x
FEATURE [PartDesign::CoordinateSystem] Local_CS007
  AttacherType = Attacher::AttachEngine3D
  MapMode = 5
  Support = -> [XY_Plane]
FEATURE [PartDesign::Plane] DatumPlane006
  Length = 305.115
  MapMode = 4
  Placement = pos=(0,4e-16,-29.2041) rot=(0.590324,0.550486,0.590324;2.13516rad)
  ResizeMode = 0
  Support = -> [Local_CS005]
  Width = 112.246
FEATURE [PartDesign::CoordinateSystem] Local_CS009
  AttacherType = Attacher::AttachEngine3D
  AttachmentOffset = pos=(0,0,-28) rot=(0,0,1;0rad)
  MapMode = 5
  Placement = pos=(0,181.372,1400) rot=(0,0,1;0rad)
  Support = -> [Local_CS002]
  expr: .AttachmentOffset.Base.z = -<<dropper>>.center_height_offset - <<main>>.distance_gutter_holes_dropper_cutout
FEATURE [Sketcher::SketchObject] Sketch039
  FullyConstrained = true
  MapMode = 5
  Support = -> [XY_Plane004]
  expr: Constraints[11] = <<module>>.module_width * 2 + <<main>>.module_distance_x + 6.3 mm + 13 mm
  expr: Constraints[15] = <<main>>.module_distance_x
  expr: Constraints[16] = <<main>>.module_distance_x + <<module>>.module_width * 2
  expr: Constraints[2] = <<main>>.rivet_d
  sketch-geometry (9):
    g0: Circle CenterX=-158.65 CenterY=0 CenterZ=0 NormalX=0 NormalY=0 NormalZ=1 AngleXU=0 Radius=1.7
    g1: Circle CenterX=158.65 CenterY=0 CenterZ=0 NormalX=0 NormalY=0 NormalZ=1 AngleXU=0 Radius=1.7
    g2: Circle CenterX=158.65 CenterY=-50 CenterZ=0 NormalX=0 NormalY=0 NormalZ=1 AngleXU=0 Radius=1.7
    g3: LineSegment StartX=-158.65 StartY=0 StartZ=0 EndX=0 EndY=0 EndZ=0
    g4: LineSegment StartX=0 StartY=0 StartZ=0 EndX=158.65 EndY=0 EndZ=0
    g5: GeomPoint X=1 Y=0 Z=0
    g6: GeomPoint X=149 Y=0 Z=0
    g7: GeomPoint X=-1 Y=0 Z=0
    g8: GeomPoint X=-149 Y=0 Z=0
  constraints (19):
    c: Equal(g0,g1)
    c: Equal(g1,g2)
    c: Diameter(g0) = 3.4
    c: PointOnObject(g1,g-1)
    c: PointOnObject(g0,g-1)
    c: Coincident(g3,g0)
    c: Coincident(g3,g-1)
    c: Coincident(g4,g3)
    c: Coincident(g4,g1)
    c: Equal(g3,g4)
    c: Vertical(g2,g1)
    c: DistanceX(g0,g1) = 317.3
    c: DistanceY(g2,g1) = 50
    c: PointOnObject(g6,g-1)
    c: Symmetric(g8,g6,g-2)
    c: DistanceX(g7,g5) = 2
    c: DistanceX(g8,g6) = 298
    c: Symmetric(g5,g7,g3)
    c: PointOnObject(g5,g-1)
FEATURE [Sketcher::SketchObject] Sketch040
  FullyConstrained = true
  MapMode = 5
  Support = -> [XY_Plane004]
  expr: Constraints[34] = Sketch039.Constraints[2]
  expr: Constraints[43] = Sketch039.Constraints[11]
  expr: Constraints[44] = Sketch039.Constraints[12]
  expr: Constraints[48] = Sketch039.Constraints[15]
  expr: Constraints[49] = Sketch039.Constraints[16]
  sketch-geometry (38):
    g0: LineSegment StartX=-149.451 StartY=-10 StartZ=0 EndX=-163.65 EndY=-10 EndZ=0
    g1: LineSegment StartX=-168.65 StartY=-5 StartZ=0 EndX=-168.65 EndY=5 EndZ=0
    g2: LineSegment StartX=-163.65 StartY=10 StartZ=0 EndX=161.65 EndY=10 EndZ=0
    g3: LineSegment StartX=166.65 StartY=5 StartZ=0 EndX=166.65 EndY=-85.9409 EndZ=0
    g4: LineSegment StartX=152.62 StartY=-100.909 StartZ=0 EndX=-119.416 EndY=-118.544 EndZ=0
    g5: GeomPoint X=-141.869 Y=-120 Z=0
    g6: ArcOfCircle CenterX=151.65 CenterY=-85.9409 CenterZ=0 NormalX=0 NormalY=0 NormalZ=1 AngleXU=0 Radius=15 StartAngle=4.77712 EndAngle=6.28319
    g7: GeomPoint X=166.65 Y=-100 Z=0
    g8: ArcOfCircle CenterX=-149.451 CenterY=-15 CenterZ=0 NormalX=0 NormalY=0 NormalZ=1 AngleXU=0 Radius=5 StartAngle=1e-16 EndAngle=1.5708
    g9: GeomPoint X=-149 Y=-10 Z=0
    g10: ArcOfCircle CenterX=-163.65 CenterY=-5 CenterZ=0 NormalX=0 NormalY=0 NormalZ=1 AngleXU=0 Radius=5 StartAngle=3.14159 EndAngle=4.71239
    g11: GeomPoint X=-168.65 Y=-10 Z=0
    g12: ArcOfCircle CenterX=-163.65 CenterY=5 CenterZ=0 NormalX=0 NormalY=0 NormalZ=1 AngleXU=0 Radius=5 StartAngle=1.5708 EndAngle=3.14159
    g13: GeomPoint X=-168.65 Y=10 Z=0
    g14: ArcOfCircle CenterX=161.65 CenterY=5 CenterZ=0 NormalX=0 NormalY=0 NormalZ=1 AngleXU=0 Radius=5 StartAngle=0 EndAngle=1.5708
    g15: GeomPoint X=166.65 Y=10 Z=0
    g16: GeomPoint X=-168.65 Y=0 Z=0
    g17: GeomPoint X=166.65 Y=0 Z=0
    g18: Circle CenterX=-158.65 CenterY=0 CenterZ=0 NormalX=0 NormalY=0 NormalZ=1 AngleXU=0 Radius=1.7
    g19: Circle CenterX=158.65 CenterY=0 CenterZ=0 NormalX=0 NormalY=0 NormalZ=1 AngleXU=0 Radius=1.7
    g20: Circle CenterX=158.65 CenterY=-50 CenterZ=0 NormalX=0 NormalY=0 NormalZ=1 AngleXU=0 Radius=1.7
    g21: LineSegment StartX=-158.65 StartY=0 StartZ=0 EndX=0 EndY=0 EndZ=0
    g22: LineSegment StartX=0 StartY=0 StartZ=0 EndX=158.65 EndY=0 EndZ=0
    g23: GeomPoint X=1 Y=0 Z=0
    g24: GeomPoint X=149 Y=0 Z=0
    g25: GeomPoint X=-1 Y=0 Z=0
    g26: GeomPoint X=-149 Y=0 Z=0
    g27: LineSegment StartX=-158.65 StartY=0 StartZ=0 EndX=-163.65 EndY=5 EndZ=0
    g28: LineSegment StartX=-144.451 StartY=-80.1674 StartZ=0 EndX=166.65 EndY=-60 EndZ=0
    g29: LineSegment StartX=-143.325 StartY=-97.5471 StartZ=0 EndX=-144.441 EndY=-80.3289 EndZ=0
    g30: LineSegment StartX=-144.451 StartY=-80.0055 StartZ=0 EndX=-144.451 EndY=-15 EndZ=0
    g31: LineSegment StartX=-144.451 StartY=-80.1674 StartZ=0 EndX=-144.451 EndY=-97.6202 EndZ=0
    g32: LineSegment StartX=-144.451 StartY=-97.6202 StartZ=0 EndX=-143.325 EndY=-97.5471 EndZ=0
    g33: LineSegment StartX=-143.325 StartY=-97.5471 StartZ=0 EndX=-142.198 EndY=-97.4741 EndZ=0
    g34: LineSegment StartX=-142.198 StartY=-97.4741 StartZ=0 EndX=-144.451 EndY=-80.1674 EndZ=0
    g35: ArcOfCircle CenterX=-120.872 CenterY=-96.0916 CenterZ=0 NormalX=0 NormalY=0 NormalZ=1 AngleXU=0 Radius=22.5 StartAngle=3.20633 EndAngle=4.77712
    g36: ArcOfCircle CenterX=-139.451 CenterY=-80.0055 CenterZ=0 NormalX=0 NormalY=0 NormalZ=1 AngleXU=0 Radius=5 StartAngle=3.14159 EndAngle=3.20633
    g37: GeomPoint X=-144.451 Y=-80.1674 Z=0
  constraints (85):
    c: Horizontal(g0)
    c: Horizontal(g2)
    c: Vertical(g3)
    c: PointOnObject(g5,g4)
    c: PointOnObject(g7,g4)
    c: PointOnObject(g7,g3)
    c: Tangent(g4,g6) = 1.5708
    c: Tangent(g3,g6) = 1.5708
    c: PointOnObject(g9,g0)
    c: Tangent(g0,g8) = -1.5708
    c: PointOnObject(g11,g0)
    c: PointOnObject(g11,g1)
    c: Tangent(g0,g10) = 1.5708
    c: Tangent(g1,g10) = 1.5708
    c: PointOnObject(g13,g1)
    c: PointOnObject(g13,g2)
    c: Tangent(g1,g12) = 1.5708
    c: Tangent(g2,g12) = 1.5708
    c: PointOnObject(g15,g2)
    c: PointOnObject(g15,g3)
    c: Tangent(g2,g14) = 1.5708
    c: Tangent(g3,g14) = 1.5708
    c: Equal(g8,g10)
    c: Equal(g10,g12)
    c: Symmetric(g10,g12,g-1)
    c: PointOnObject(g16,g1)
    c: PointOnObject(g16,g-1)
    c: PointOnObject(g17,g3)
    c: PointOnObject(g17,g-1)
    c: Diameter(g12) = 10
    c: DistanceY(g5,g7) = 20
    c: DistanceY(g0,g2) = 20
    c: Equal(g18,g19)
    c: Equal(g19,g20)
    c: Diameter(g18) = 3.4
    c: PointOnObject(g19,g-1)
    c: PointOnObject(g18,g-1)
    c: Coincident(g21,g18)
    c: Coincident(g21,g-1)
    c: Coincident(g22,g21)
    c: Coincident(g22,g19)
    c: Equal(g21,g22)
    c: Vertical(g20,g19)
    c: DistanceX(g18,g19) = 317.3
    c: DistanceY(g20,g19) = 50
    c: PointOnObject(g23,g-1)
    c: PointOnObject(g24,g-1)
    c: Symmetric(g26,g24,g-2)
    c: DistanceX(g25,g23) = 2
    c: DistanceX(g26,g24) = 298
    c: Vertical(g9,g26)
    c: Equal(g14,g12)
    c: Coincident(g27,g18)
    c: Coincident(g27,g12)
    c: Angle(g-1,g27) = 2.35619
    c: PointOnObject(g28,g3)
    c: Parallel(g4,g28)
    c: DistanceY(g28,g20) = 10
    c: DistanceY(g7,g28) = 40
    c: Symmetric(g23,g25,g21)
    c: DistanceX(g19,g17) = 8
    c: Vertical(g30)
    c: PointOnObject(g5,g29)
    c: PointOnObject(g9,g29)
    c: Coincident(g37,g28)
    c: Perpendicular(g28,g29)
    c: Tangent(g30,g8) = -1.5708
    c: Coincident(g37,g31)
    c: Vertical(g31)
    c: Coincident(g31,g32)
    c: Coincident(g33,g34)
    c: Coincident(g34,g31)
    c: Tangent(g32,g33) = -1.5708
    c: Coincident(g29,g32)
    c: Equal(g32,g33)
    c: Equal(g31,g34)
    c: Tangent(g35,g4) = 1.5708
    c: Diameter(g35) = 45
    c: Tangent(g35,g29) = 1.5708
    c: PointOnObject(g37,g29)
    c: PointOnObject(g37,g30)
    c: Tangent(g29,g36) = 1.5708
    c: Tangent(g30,g36) = 1.5708
    c: Diameter(g36) = 10
    c: Diameter(g6) = 30
FEATURE [PartDesign::Pad] Pad
  Direction = (0,0,1)
  Length = 0.5
  Length2 = 10
  Profile = -> Sketch040
  ReferenceAxis = -> Sketch040 [N_Axis]
  Type = 0
FEATURE [PartDesign::Pocket] Pocket013
  BaseFeature = -> Pad
  Direction = (0,0,-1)
  Length = 5
  Length2 = 5
  Midplane = true
  Profile = -> Sketch039
  ReferenceAxis = -> Sketch039 [N_Axis]
  Type = 1
FEATURE [PartDesign::CoordinateSystem] Local_CS010
  AttacherType = Attacher::AttachEngine3D
  MapMode = 5
  Support = -> [XY_Plane004]
FEATURE [Sketcher::SketchObject] Sketch041
  FullyConstrained = false
  MapMode = 5
  Support = -> [XY_Plane004]
  expr: Constraints[33] = Sketch040.Constraints[29]
  expr: Constraints[34] = Sketch040.Constraints[30]
  expr: Constraints[35] = Sketch040.Constraints[31]
  expr: Constraints[38] = Sketch040.Constraints[34]
  expr: Constraints[47] = Sketch040.Constraints[43]
  expr: Constraints[48] = Sketch040.Constraints[44]
  expr: Constraints[52] = Sketch040.Constraints[48]
  expr: Constraints[53] = Sketch040.Constraints[49]
  expr: Constraints[59] = Sketch040.Constraints[54]
  expr: Constraints[63] = Sketch040.Constraints[57]
  expr: Constraints[64] = Sketch040.Constraints[58]
  sketch-geometry (31):
    g0: LineSegment StartX=-154 StartY=-10 StartZ=0 EndX=-163.65 EndY=-10 EndZ=0
    g1: LineSegment StartX=-168.65 StartY=-5 StartZ=0 EndX=-168.65 EndY=5 EndZ=0
    g2: LineSegment StartX=-163.65 StartY=10 StartZ=0 EndX=158.65 EndY=10 EndZ=0
    g3: LineSegment StartX=163.65 StartY=5 StartZ=0 EndX=163.65 EndY=-78.8933 EndZ=0
    g4: LineSegment StartX=142.586 StartY=-101.347 StartZ=0 EndX=-125.064 EndY=-118.469 EndZ=0
    g5: LineSegment StartX=-149 StartY=-96.0147 StartZ=0 EndX=-149 EndY=-15 EndZ=0
    g6: GeomPoint X=-149 Y=-120 Z=0
    g7: ArcOfCircle CenterX=141.15 CenterY=-78.8933 CenterZ=0 NormalX=0 NormalY=0 NormalZ=1 AngleXU=0 Radius=22.5 StartAngle=4.77627 EndAngle=6.28319
    g8: GeomPoint X=163.65 Y=-100 Z=0
    g9: ArcOfCircle CenterX=-154 CenterY=-15 CenterZ=0 NormalX=0 NormalY=0 NormalZ=1 AngleXU=0 Radius=5 StartAngle=0 EndAngle=1.5708
    g10: GeomPoint X=-149 Y=-10 Z=0
    g11: ArcOfCircle CenterX=-163.65 CenterY=-5 CenterZ=0 NormalX=0 NormalY=0 NormalZ=1 AngleXU=0 Radius=5 StartAngle=3.14159 EndAngle=4.71239
    g12: GeomPoint X=-168.65 Y=-10 Z=0
    g13: ArcOfCircle CenterX=-163.65 CenterY=5 CenterZ=0 NormalX=0 NormalY=0 NormalZ=1 AngleXU=0 Radius=5 StartAngle=1.5708 EndAngle=3.14159
    g14: GeomPoint X=-168.65 Y=10 Z=0
    g15: ArcOfCircle CenterX=158.65 CenterY=5 CenterZ=0 NormalX=0 NormalY=0 NormalZ=1 AngleXU=0 Radius=5 StartAngle=0 EndAngle=1.5708
    g16: GeomPoint X=163.65 Y=10 Z=0
    g17: GeomPoint X=-168.65 Y=0 Z=0
    g18: GeomPoint X=163.65 Y=0 Z=0
    g19: Circle CenterX=-158.65 CenterY=0 CenterZ=0 NormalX=0 NormalY=0 NormalZ=1 AngleXU=0 Radius=1.7
    g20: Circle CenterX=158.65 CenterY=0 CenterZ=0 NormalX=0 NormalY=0 NormalZ=1 AngleXU=0 Radius=1.7
    g21: Circle CenterX=158.65 CenterY=-50 CenterZ=0 NormalX=0 NormalY=0 NormalZ=1 AngleXU=0 Radius=1.7
    g22: LineSegment StartX=-158.65 StartY=0 StartZ=0 EndX=0 EndY=0 EndZ=0
    g23: LineSegment StartX=0 StartY=0 StartZ=0 EndX=158.65 EndY=0 EndZ=0
    g24: GeomPoint X=1 Y=0 Z=0
    g25: GeomPoint X=149 Y=0 Z=0
    g26: GeomPoint X=-1 Y=0 Z=0
    g27: GeomPoint X=-149 Y=0 Z=0
    g28: LineSegment StartX=-158.65 StartY=0 StartZ=0 EndX=-163.65 EndY=5 EndZ=0
    g29: LineSegment StartX=-149 StartY=-80 StartZ=0 EndX=163.65 EndY=-60 EndZ=0
    g30: Circle CenterX=-135.369 CenterY=-84.4535 CenterZ=0 NormalX=0 NormalY=0 NormalZ=1 AngleXU=0 Radius=5
  constraints (67):
    c: Horizontal(g0)
    c: Horizontal(g2)
    c: Vertical(g3)
    c: Vertical(g5)
    c: PointOnObject(g6,g5)
    c: PointOnObject(g6,g4)
    c: PointOnObject(g8,g4)
    c: PointOnObject(g8,g3)
    c: Tangent(g4,g7) = 1.5708
    c: Tangent(g3,g7) = 1.5708
    c: PointOnObject(g10,g0)
    c: PointOnObject(g10,g5)
    c: Tangent(g0,g9) = -1.5708
    c: Tangent(g5,g9) = -1.5708
    c: PointOnObject(g12,g0)
    c: PointOnObject(g12,g1)
    c: Tangent(g0,g11) = 1.5708
    c: Tangent(g1,g11) = 1.5708
    c: PointOnObject(g14,g1)
    c: PointOnObject(g14,g2)
    c: Tangent(g1,g13) = 1.5708
    c: Tangent(g2,g13) = 1.5708
    c: PointOnObject(g16,g2)
    c: PointOnObject(g16,g3)
    c: Tangent(g2,g15) = 1.5708
    c: Tangent(g3,g15) = 1.5708
    c: Equal(g9,g11)
    c: Equal(g11,g13)
    c: Symmetric(g11,g13,g-1)
    c: PointOnObject(g17,g1)
    c: PointOnObject(g17,g-1)
    c: PointOnObject(g18,g3)
    c: PointOnObject(g18,g-1)
    c: Diameter(g13) = 10
    c: DistanceY(g6,g8) = 20
    c: DistanceY(g0,g2) = 20
    c: Equal(g19,g20)
    c: Equal(g20,g21)
    c: Diameter(g19) = 3.4
    c: PointOnObject(g20,g-1)
    c: PointOnObject(g19,g-1)
    c: Coincident(g22,g19)
    c: Coincident(g22,g-1)
    c: Coincident(g23,g22)
    c: Coincident(g23,g20)
    c: Equal(g22,g23)
    c: Vertical(g21,g20)
    c: DistanceX(g19,g20) = 317.3
    c: DistanceY(g21,g20) = 50
    c: PointOnObject(g24,g-1)
    c: PointOnObject(g25,g-1)
    c: Symmetric(g27,g25,g-2)
    c: DistanceX(g26,g24) = 2
    c: DistanceX(g27,g25) = 298
    c: Vertical(g10,g27)
    c: Equal(g15,g13)
    c: Vertical(g15,g20)
    c: Coincident(g28,g19)
    c: Coincident(g28,g13)
    c: Angle(g-1,g28) = 2.35619
    c: PointOnObject(g29,g5)
    c: PointOnObject(g29,g3)
    c: Parallel(g4,g29)
    c: DistanceY(g29,g21) = 10
    c: DistanceY(g8,g29) = 40
    c: Diameter(g30) = 10
    c: Symmetric(g24,g26,g22)
FEATURE [PartDesign::Pocket] Pocket014
  BaseFeature = -> Pocket013
  Direction = (0,0,-1)
  Length = 5
  Length2 = 5
  Midplane = true
  Profile = -> Sketch041
  ReferenceAxis = -> Sketch041 [N_Axis]
  Type = 1
FEATURE [Sketcher::SketchObject] Sketch042
  FullyConstrained = false
  MapMode = 5
  Support = -> [XY_Plane004]
  expr: Constraints[29] = Sketch040.Constraints[29]
  expr: Constraints[30] = Sketch040.Constraints[30]
  expr: Constraints[31] = Sketch040.Constraints[31]
  expr: Constraints[34] = Sketch040.Constraints[34]
  expr: Constraints[43] = Sketch040.Constraints[43]
  expr: Constraints[44] = Sketch040.Constraints[44]
  expr: Constraints[48] = Sketch040.Constraints[48]
  expr: Constraints[49] = Sketch040.Constraints[49]
  expr: Constraints[54] = Sketch040.Constraints[54]
  expr: Constraints[57] = Sketch040.Constraints[57]
  expr: Constraints[58] = Sketch040.Constraints[58]
  expr: Constraints[60] = Sketch040.Constraints[60]
  expr: Constraints[78] = Sketch040.Constraints[77]
  sketch-geometry (36):
    g0: LineSegment StartX=-149.451 StartY=-10 StartZ=0 EndX=-163.65 EndY=-10 EndZ=0
    g1: LineSegment StartX=-168.65 StartY=-5 StartZ=0 EndX=-168.65 EndY=5 EndZ=0
    g2: LineSegment StartX=-163.65 StartY=10 StartZ=0 EndX=161.65 EndY=10 EndZ=0
    g3: LineSegment StartX=166.65 StartY=5 StartZ=0 EndX=166.65 EndY=-78.9113 EndZ=0
    g4: LineSegment StartX=145.606 StartY=-101.364 StartZ=0 EndX=-119.416 EndY=-118.544 EndZ=0
    g5: GeomPoint X=-141.869 Y=-120 Z=0
    g6: ArcOfCircle CenterX=144.15 CenterY=-78.9113 CenterZ=0 NormalX=0 NormalY=0 NormalZ=1 AngleXU=0 Radius=22.5 StartAngle=4.77712 EndAngle=6.28319
    g7: GeomPoint X=166.65 Y=-100 Z=0
    g8: ArcOfCircle CenterX=-149.451 CenterY=-15 CenterZ=0 NormalX=0 NormalY=0 NormalZ=1 AngleXU=0 Radius=5 StartAngle=1e-16 EndAngle=1.5708
    g9: GeomPoint X=-149 Y=-10 Z=0
    g10: ArcOfCircle CenterX=-163.65 CenterY=-5 CenterZ=0 NormalX=0 NormalY=0 NormalZ=1 AngleXU=0 Radius=5 StartAngle=3.14159 EndAngle=4.71239
    g11: GeomPoint X=-168.65 Y=-10 Z=0
    g12: ArcOfCircle CenterX=-163.65 CenterY=5 CenterZ=0 NormalX=0 NormalY=0 NormalZ=1 AngleXU=0 Radius=5 StartAngle=1.5708 EndAngle=3.14159
    g13: GeomPoint X=-168.65 Y=10 Z=0
    g14: ArcOfCircle CenterX=161.65 CenterY=5 CenterZ=0 NormalX=0 NormalY=0 NormalZ=1 AngleXU=0 Radius=5 StartAngle=0 EndAngle=1.5708
    g15: GeomPoint X=166.65 Y=10 Z=0
    g16: GeomPoint X=-168.65 Y=0 Z=0
    g17: GeomPoint X=166.65 Y=0 Z=0
    g18: Circle CenterX=-158.65 CenterY=0 CenterZ=0 NormalX=0 NormalY=0 NormalZ=1 AngleXU=0 Radius=1.7
    g19: Circle CenterX=158.65 CenterY=0 CenterZ=0 NormalX=0 NormalY=0 NormalZ=1 AngleXU=0 Radius=1.7
    g20: Circle CenterX=158.65 CenterY=-50 CenterZ=0 NormalX=0 NormalY=0 NormalZ=1 AngleXU=0 Radius=1.7
    g21: LineSegment StartX=-158.65 StartY=0 StartZ=0 EndX=0 EndY=0 EndZ=0
    g22: LineSegment StartX=0 StartY=0 StartZ=0 EndX=158.65 EndY=0 EndZ=0
    g23: GeomPoint X=1 Y=0 Z=0
    g24: GeomPoint X=149 Y=0 Z=0
    g25: GeomPoint X=-1 Y=0 Z=0
    g26: GeomPoint X=-149 Y=0 Z=0
    g27: LineSegment StartX=-158.65 StartY=0 StartZ=0 EndX=-163.65 EndY=5 EndZ=0
    g28: LineSegment StartX=-144.451 StartY=-80.1674 StartZ=0 EndX=166.65 EndY=-60 EndZ=0
    g29: LineSegment StartX=-143.325 StartY=-97.5471 StartZ=0 EndX=-144.451 EndY=-80.1674 EndZ=0
    g30: LineSegment StartX=-144.451 StartY=-80.1674 StartZ=0 EndX=-144.451 EndY=-15 EndZ=0
    g31: LineSegment StartX=-144.451 StartY=-80.1674 StartZ=0 EndX=-144.451 EndY=-97.6202 EndZ=0
    g32: LineSegment StartX=-144.451 StartY=-97.6202 StartZ=0 EndX=-143.325 EndY=-97.5471 EndZ=0
    g33: LineSegment StartX=-143.325 StartY=-97.5471 StartZ=0 EndX=-142.198 EndY=-97.4741 EndZ=0
    g34: LineSegment StartX=-142.198 StartY=-97.4741 StartZ=0 EndX=-144.451 EndY=-80.1674 EndZ=0
    g35: ArcOfCircle CenterX=-120.872 CenterY=-96.0916 CenterZ=0 NormalX=0 NormalY=0 NormalZ=1 AngleXU=0 Radius=22.5 StartAngle=3.20633 EndAngle=4.77712
  constraints (80):
    c: Horizontal(g0)
    c: Horizontal(g2)
    c: Vertical(g3)
    c: PointOnObject(g5,g4)
    c: PointOnObject(g7,g4)
    c: PointOnObject(g7,g3)
    c: Tangent(g4,g6) = 1.5708
    c: Tangent(g3,g6) = 1.5708
    c: PointOnObject(g9,g0)
    c: Tangent(g0,g8) = -1.5708
    c: PointOnObject(g11,g0)
    c: PointOnObject(g11,g1)
    c: Tangent(g0,g10) = 1.5708
    c: Tangent(g1,g10) = 1.5708
    c: PointOnObject(g13,g1)
    c: PointOnObject(g13,g2)
    c: Tangent(g1,g12) = 1.5708
    c: Tangent(g2,g12) = 1.5708
    c: PointOnObject(g15,g2)
    c: PointOnObject(g15,g3)
    c: Tangent(g2,g14) = 1.5708
    c: Tangent(g3,g14) = 1.5708
    c: Equal(g8,g10)
    c: Equal(g10,g12)
    c: Symmetric(g10,g12,g-1)
    c: PointOnObject(g16,g1)
    c: PointOnObject(g16,g-1)
    c: PointOnObject(g17,g3)
    c: PointOnObject(g17,g-1)
    c: Diameter(g12) = 10
    c: DistanceY(g5,g7) = 20
    c: DistanceY(g0,g2) = 20
    c: Equal(g18,g19)
    c: Equal(g19,g20)
    c: Diameter(g18) = 3.4
    c: PointOnObject(g19,g-1)
    c: PointOnObject(g18,g-1)
    c: Coincident(g21,g18)
    c: Coincident(g21,g-1)
    c: Coincident(g22,g21)
    c: Coincident(g22,g19)
    c: Equal(g21,g22)
    c: Vertical(g20,g19)
    c: DistanceX(g18,g19) = 317.3
    c: DistanceY(g20,g19) = 50
    c: PointOnObject(g23,g-1)
    c: PointOnObject(g24,g-1)
    c: Symmetric(g26,g24,g-2)
    c: DistanceX(g25,g23) = 2
    c: DistanceX(g26,g24) = 298
    c: Vertical(g9,g26)
    c: Equal(g14,g12)
    c: Coincident(g27,g18)
    c: Coincident(g27,g12)
    c: Angle(g-1,g27) = 2.35619
    c: PointOnObject(g28,g3)
    c: Parallel(g4,g28)
    c: DistanceY(g28,g20) = 10
    c: DistanceY(g7,g28) = 40
    c: Symmetric(g23,g25,g21)
    c: DistanceX(g19,g17) = 8
    c: Coincident(g29,g30)
    c: Vertical(g30)
    c: PointOnObject(g5,g29)
    c: PointOnObject(g9,g29)
    c: Coincident(g29,g28)
    c: Perpendicular(g28,g29)
    c: Tangent(g30,g8) = -1.5708
    c: Coincident(g29,g31)
    c: Vertical(g31)
    c: Coincident(g31,g32)
    c: Coincident(g33,g34)
    c: Coincident(g34,g31)
    c: Tangent(g32,g33) = -1.5708
    c: Coincident(g29,g32)
    c: Equal(g32,g33)
    c: Equal(g31,g34)
    c: Tangent(g35,g4) = 1.5708
    c: Diameter(g35) = 45
    c: Tangent(g35,g29) = 1.5708
FEATURE [PartDesign::FeaturePython] Fold  # WARN: FeaturePython — macro-defined, semantics opaque (R4)
  BaseFeature = -> Pocket014
  BendLine = -> Sketch042
  Position = 0
  angle = 105
  baseObject = -> Pocket014 [Face4]
  invert = true
  invertbend = false
  kfactor = 0.5
  radius = 2
  unfold = false
FEATURE [PartDesign::Body] Body003  label="vodostok_material_0.30ansi"
  Group = -> [Sketch039,Sketch040,Pad,Pocket013,Local_CS010,Sketch041,Pocket014,Sketch042,Fold]
  Origin = -> Origin004
  Tip = -> Fold
FEATURE [Sketcher::SketchObject] Sketch043
  FullyConstrained = true
  MapMode = 5
  Placement = pos=(0,0,0) rot=(0.57735,0.57735,0.57735;2.0944rad)
  Support = -> [YZ_Plane]
  expr: .Constraints.offset = Sketch002.Constraints[10]
  expr: Constraints[11] = Sketch002.Constraints[11]
  expr: Constraints[8] = Sketch002.Constraints[8]
  expr: Constraints[9] = Sketch002.Constraints[9]
  sketch-geometry (9):
    g0: LineSegment StartX=71 StartY=360 StartZ=0 EndX=71 EndY=410 EndZ=0
    g1: LineSegment StartX=71 StartY=410 StartZ=0 EndX=205 EndY=410 EndZ=0
    g2: LineSegment StartX=205 StartY=410 StartZ=0 EndX=205 EndY=360 EndZ=0
    g3: LineSegment StartX=205 StartY=360 StartZ=0 EndX=71 EndY=360 EndZ=0
    g4: LineSegment StartX=0 StartY=-10 StartZ=0 EndX=210 EndY=-10 EndZ=0
    g5: LineSegment StartX=210 StartY=-10 StartZ=0 EndX=210 EndY=410 EndZ=0
    g6: LineSegment StartX=0 StartY=410 StartZ=0 EndX=0 EndY=-10 EndZ=0
    g7: LineSegment StartX=210 StartY=410 StartZ=0 EndX=205 EndY=410 EndZ=0
    g8: LineSegment StartX=71 StartY=410 StartZ=0 EndX=0 EndY=410 EndZ=0
  constraints (27):
    c: Coincident(g0,g1)
    c: Coincident(g1,g2)
    c: Coincident(g2,g3)
    c: Coincident(g3,g0)
    c: Horizontal(g1)
    c: Horizontal(g3)
    c: Vertical(g0)
    c: Vertical(g2)
    c: DistanceY(g1) = 410
    c: DistanceY(g2,g2) = 50
    c: DistanceX(g0) = 71  'offset'
    c: DistanceX(g1) = 205
    c: DistanceX(g3,g3) = 134
    c: Coincident(g4,g5)
    c: Coincident(g5,g7)
    c: Coincident(g8,g6)
    c: Coincident(g6,g4)
    c: Horizontal(g4)
    c: Vertical(g5)
    c: Vertical(g6)
    c: PointOnObject(g4,g-2)
    c: Horizontal(g7)
    c: Horizontal(g8)
    c: Coincident(g7,g1)
    c: Coincident(g8,g0)
    c: DistanceY(g4) = -10
    c: DistanceX(g4) = 210  'length'
FEATURE [PartDesign::Line] DatumLine002
  AttacherType = Attacher::AttachEngineLine
  AttachmentOffset = pos=(0,0,0) rot=(0,1,0;1.0472rad)
  Length = 20
  MapMode = 16
  Placement = pos=(0,0,0) rot=(0.186157,0.694747,0.694747;2.77349rad)
  ResizeMode = 0
  Support = -> [XY_Plane]
FEATURE [PartDesign::CoordinateSystem] Local_CS011
  AttacherType = Attacher::AttachEngine3D
  AttachmentOffset = pos=(0,0,94) rot=(0.57735,0.57735,0.57735;2.0944rad)
  MapMode = 5
  Placement = pos=(0,181.372,504) rot=(0.57735,0.57735,0.57735;2.0944rad)
  Support = -> [Local_CS001]
FEATURE [PartDesign::AdditiveCylinder] Cylinder
  Angle = 360
  AttacherType = Attacher::AttachEngine3D
  FirstAngle = 0
  Height = 390
  Radius = 205
  SecondAngle = 0
FEATURE [PartDesign::Body] Body003003  label="basin"
  Group = -> [Cylinder]
  Origin = -> Origin006
  Tip = -> Cylinder
FEATURE [Sketcher::SketchObject] Sketch046
  AttachmentOffset = pos=(0,410,0) rot=(0,0,1;0rad)
  FullyConstrained = true
  MapMode = 5
  Placement = pos=(-9.1e-14,9.1e-14,410) rot=(0.57735,0.57735,0.57735;2.0944rad)
  Support = -> [YZ_Plane]
  expr: .AttachmentOffset.Base.y = <<main>>.basin_height
  sketch-geometry (9):
    g0: LineSegment StartX=71.1 StartY=9.379e-13 StartZ=0 EndX=0 EndY=0 EndZ=0
    g1: LineSegment StartX=0 StartY=0 StartZ=0 EndX=0 EndY=60 EndZ=0
    g2: LineSegment StartX=0 StartY=60 StartZ=0 EndX=26.1 EndY=60 EndZ=0
    g3: ArcOfCircle CenterX=71.1 CenterY=40 CenterZ=0 NormalX=0 NormalY=0 NormalZ=1 AngleXU=0 Radius=40 StartAngle=3.14159 EndAngle=4.71239
    g4: LineSegment StartX=31.1 StartY=40 StartZ=0 EndX=31.1 EndY=55 EndZ=0
    g5: ArcOfCircle CenterX=26.1 CenterY=55 CenterZ=0 NormalX=0 NormalY=0 NormalZ=1 AngleXU=0 Radius=5 StartAngle=5e-16 EndAngle=1.5708
    g6: LineSegment StartX=71.1 StartY=9.379e-13 StartZ=0 EndX=71.1 EndY=-40 EndZ=0
    g7: LineSegment StartX=71.1 StartY=-40 StartZ=0 EndX=0 EndY=-40 EndZ=0
    g8: LineSegment StartX=0 StartY=-40 StartZ=0 EndX=0 EndY=0 EndZ=0
  constraints (24):
    c: PointOnObject(g0,g-1)
    c: Coincident(g0,g-1)
    c: Coincident(g1,g0)
    c: PointOnObject(g1,g-2)
    c: Coincident(g2,g1)
    c: Horizontal(g2)
    c: Coincident(g3,g0)
    c: Diameter(g3) = 80
    c: DistanceY(g1) = 60
    c: Tangent(g3,g-1)
    c: Vertical(g4)
    c: Tangent(g4,g3) = 1.5708
    c: Tangent(g5,g4) = -1.5708
    c: Tangent(g5,g2) = 1.5708
    c: Diameter(g5) = 10
    c: DistanceX(g3) = 31.1
    c: Coincident(g6,g3)
    c: Vertical(g6)
    c: Coincident(g7,g6)
    c: PointOnObject(g7,g-2)
    c: Horizontal(g7)
    c: Coincident(g8,g7)
    c: Coincident(g8,g1)
    c: DistanceY(g7) = -40
FEATURE [PartDesign::FeaturePython] Bend002  label="cover_holders_corners_face"  # WARN: FeaturePython — macro-defined, semantics opaque (R4)
  AutoMiter = true
  BaseFeature = -> PolarPattern
  BendType = 0
  LengthList = [40]
  LengthSpec = 2
  ReliefFactor = 0.7
  UseReliefFactor = false
  angle = 90
  baseObject = -> PolarPattern [Edge166,Edge137,Edge95,Edge65]
  bendAList = [90]
  extend1 = 0
  extend2 = 0
  gap1 = 3.18
  gap2 = 3.18
  invert = false
  kfactor = 0.5
  length = 40
  maxExtendDist = 5
  minGap = 0.1
  minReliefGap = 0.1
  miterangle1 = 0
  miterangle2 = 0
  offset = 0
  radius = 0.1
  reliefType = 0
  reliefd = 0.1
  reliefw = 0.1
  sketchflip = false
  sketchinvert = false
  unfold = false
  expr: gap2 = gap1
  expr: radius = <<main>>.bend_r
FEATURE [PartDesign::FeaturePython] Bend003  label="cover_holders_corners_back"  # WARN: FeaturePython — macro-defined, semantics opaque (R4)
  AutoMiter = true
  BaseFeature = -> Bend002
  BendType = 0
  LengthList = [25]
  LengthSpec = 2
  ReliefFactor = 0.7
  UseReliefFactor = false
  angle = 90
  baseObject = -> Bend002 [Edge358,Edge168]
  bendAList = [90]
  extend1 = 0
  extend2 = 0
  gap1 = 3.18
  gap2 = 3.18
  invert = false
  kfactor = 0.5
  length = 25
  maxExtendDist = 5
  minGap = 0.1
  minReliefGap = 0.1
  miterangle1 = 0
  miterangle2 = 0
  offset = 0
  radius = 0.1
  reliefType = 0
  reliefd = 0.1
  reliefw = 0.1
  sketchflip = false
  sketchinvert = false
  unfold = false
  expr: gap2 = gap1
  expr: radius = <<main>>.bend_r
FEATURE [PartDesign::Plane] DatumPlane007
  AttachmentOffset = pos=(0,0,0) rot=(0,-1,0;0.523599rad)
  Length = 1027.22
  MapMode = 3
  Placement = pos=(0,0,0) rot=(0.935113,-0.250563,-0.250563;1.63783rad)
  ResizeMode = 0
  Support = -> [XY_Plane]
  Width = 1670
FEATURE [Sketcher::SketchObject] Sketch047
  FullyConstrained = true
  MapMode = 5
  Placement = pos=(0,0,0) rot=(0.935113,-0.250563,-0.250563;1.63783rad)
  Support = -> [DatumPlane007]
  expr: .Constraints.bottom = <<main>>.basin_height + 100 mm
  expr: Constraints[10] = <<main>>.total_length
  expr: Constraints[12] = Sketch.Constraints.overlap_from_origin
  sketch-geometry (10):
    g0: LineSegment StartX=30.1036 StartY=0 StartZ=0 EndX=30.1036 EndY=517.5 EndZ=0
    g1: LineSegment StartX=22.6036 StartY=510 StartZ=0 EndX=10.17 EndY=510 EndZ=0
    g2: LineSegment StartX=10.17 StartY=510 StartZ=0 EndX=10.17 EndY=0 EndZ=0
    g3: LineSegment StartX=10.17 StartY=1428 StartZ=0 EndX=30.1036 EndY=1428 EndZ=0
    g4: LineSegment StartX=30.1036 StartY=1428 StartZ=0 EndX=30.1036 EndY=1370.5 EndZ=0
    g5: LineSegment StartX=10.17 StartY=1378 StartZ=0 EndX=10.17 EndY=1428 EndZ=0
    g6: ArcOfCircle CenterX=22.6036 CenterY=517.5 CenterZ=0 NormalX=0 NormalY=0 NormalZ=1 AngleXU=0 Radius=7.5 StartAngle=4.71239 EndAngle=6.28319
    g7: ArcOfCircle CenterX=22.6036 CenterY=1370.5 CenterZ=0 NormalX=0 NormalY=0 NormalZ=1 AngleXU=0 Radius=7.5 StartAngle=1.2e-14 EndAngle=1.5708
    g8: LineSegment StartX=10.17 StartY=1378 StartZ=0 EndX=22.6036 EndY=1378 EndZ=0
    g9: LineSegment StartX=10.17 StartY=0 StartZ=0 EndX=30.1036 EndY=0 EndZ=0
  constraints (28):
    c: Coincident(g1,g2)
    c: Horizontal(g1)
    c: Vertical(g0)
    c: Vertical(g2)
    c: Coincident(g3,g4)
    c: Coincident(g5,g3)
    c: Horizontal(g3)
    c: Vertical(g4)
    c: Vertical(g5)
    c: Vertical(g0,g4)
    c: DistanceY(g3) = 1428
    c: DistanceY(g5,g3) = 50  'top'
    c: DistanceX(g0) = 30.1036
    c: Tangent(g1,g6) = 1.5708
    c: Tangent(g0,g6) = -1.5708
    c: Diameter(g6) = 15
    c: Coincident(g8,g5)
    c: Horizontal(g8)
    c: Tangent(g7,g4) = 1.5708
    c: Tangent(g8,g7) = 1.5708
    c: Equal(g7,g6)
    c: DistanceY(g1) = 510  'bottom'
    c: PointOnObject(g2,g-1)
    c: Coincident(g9,g2)
    c: Coincident(g9,g0)
    c: Horizontal(g9)
    c: Vertical(g5,g1)
    c: DistanceX(g3) = 10.17
FEATURE [PartDesign::Pocket] Pocket021
  BaseFeature = -> Bend003
  Direction = (0.5,0.866025,-1e-16)
  Length = 12.5
  Length2 = 5
  Profile = -> Sketch047
  ReferenceAxis = -> Sketch047 [N_Axis]
  Reversed = true
  Type = 0
  expr: Length = <<main>>.end_face_width / 2 - <<main>>.thickness + 1 mm
FEATURE [PartDesign::Plane] DatumPlane008
  AttachmentOffset = pos=(0,0,0) rot=(0,-1,0;0.523599rad)
  Length = 992.549
  MapMode = 4
  Placement = pos=(0,0,0) rot=(0.774597,0.447214,0.447214;1.82348rad)
  ResizeMode = 0
  Support = -> [XY_Plane]
  Width = 1665.87
FEATURE [Sketcher::SketchObject] Sketch048
  FullyConstrained = false
  MapMode = 5
  Placement = pos=(0,0,0) rot=(0.774597,0.447214,0.447214;1.82348rad)
  Support = -> [DatumPlane008]
  expr: Constraints[0] = <<main>>.thickness - <<main>>.al_thickness - 0.01 mm
  expr: Constraints[1] = <<main>>.total_length
  expr: Constraints[2] = -(<<main>>.end_face_width / 2 - <<main>>.thickness)
  expr: Constraints[8] = <<main>>.thickness
  sketch-geometry (6):
    g0: LineSegment StartX=-14.19 StartY=1428 StartZ=0 EndX=-11.5 EndY=1425 EndZ=0
    g1: LineSegment StartX=-14.19 StartY=1428 StartZ=0 EndX=-11.5 EndY=1428 EndZ=0
    g2: LineSegment StartX=-11.5 StartY=1428 StartZ=0 EndX=-11.5 EndY=1425 EndZ=0
    g3: LineSegment StartX=-11.5 StartY=1428 StartZ=0 EndX=-6.5071 EndY=1428 EndZ=0
    g4: LineSegment StartX=-6.5071 StartY=1428 StartZ=0 EndX=-6.5071 EndY=1425 EndZ=0
    g5: LineSegment StartX=-6.5071 StartY=1425 StartZ=0 EndX=-11.5 EndY=1425 EndZ=0
  constraints (16):
    c: DistanceX(g0,g0) = 2.69
    c: DistanceY(g0) = 1428
    c: DistanceX(g0) = -11.5
    c: Coincident(g1,g0)
    c: Horizontal(g1)
    c: Coincident(g2,g1)
    c: Coincident(g2,g0)
    c: Vertical(g2)
    c: DistanceY(g0,g1) = 3
    c: Coincident(g1,g3)
    c: Horizontal(g3)
    c: Coincident(g3,g4)
    c: Vertical(g4)
    c: Coincident(g4,g5)
    c: Coincident(g5,g0)
    c: Horizontal(g5)
FEATURE [Sketcher::SketchObject] Sketch049
  AttachmentOffset = pos=(-54.5,0,0) rot=(0,0,1;1.5708rad)
  FullyConstrained = true
  MapMode = 5
  Placement = pos=(-54.5,0,0) rot=(0,0,1;1.5708rad)
  Support = -> [XY_Plane]
  expr: .AttachmentOffset.Base.x = -<<main>>.end_face_width / 2 - <<cover_holders_corners_face>>.length
  expr: Constraints[15] = <<cover_holder_corner>>.Constraints.offset + <<cover_holder_corner>>.Constraints.length - <<cover_holders_corners_back>>.gap2
  expr: Constraints[18] = <<cover_holder_corner>>.Constraints.offset + <<cover_holders_corners_back>>.gap1
  sketch-geometry (6):
    g0: ArcOfCircle CenterX=81.68 CenterY=-7.5 CenterZ=0 NormalX=0 NormalY=0 NormalZ=1 AngleXU=0 Radius=7.5 StartAngle=1.5708 EndAngle=3.14159
    g1: LineSegment StartX=74.18 StartY=-7.5 StartZ=0 EndX=74.18 EndY=-5.00551e-11 EndZ=0
    g2: LineSegment StartX=74.18 StartY=-5.00551e-11 StartZ=0 EndX=81.68 EndY=-5.00551e-11 EndZ=0
    g3: ArcOfCircle CenterX=194.32 CenterY=-7.5 CenterZ=0 NormalX=0 NormalY=0 NormalZ=1 AngleXU=0 Radius=7.5 StartAngle=6.28318 EndAngle=7.85398
    g4: LineSegment StartX=201.82 StartY=-7.5 StartZ=0 EndX=201.82 EndY=0 EndZ=0
    g5: LineSegment StartX=194.32 StartY=0 StartZ=0 EndX=201.82 EndY=0 EndZ=0
  constraints (19):
    c: Coincident(g1,g0)
    c: Vertical(g1)
    c: Tangent(g1,g0)
    c: Coincident(g2,g1)
    c: Coincident(g2,g0)
    c: Tangent(g2,g0)
    c: Coincident(g4,g3)
    c: PointOnObject(g4,g-1)
    c: Vertical(g4)
    c: Tangent(g4,g3)
    c: Coincident(g5,g4)
    c: Horizontal(g5)
    c: Diameter(g3) = 15
    c: Tangent(g5,g3) = 1.5708
    c: Horizontal(g2)
    c: DistanceX(g4) = 201.82
    c: PointOnObject(g1,g-1)
    c: Equal(g0,g3)
    c: DistanceX(g1) = 74.18
FEATURE [PartDesign::PolarPattern] PolarPattern005
  Angle = 120
  Axis = -> Z_Axis
  Occurrences = 2
  Reversed = true
FEATURE [PartDesign::Mirrored] Mirrored006
  MirrorPlane = -> YZ_Plane
FEATURE [Sketcher::SketchObject] Sketch050
  FullyConstrained = true
  MapMode = 5
  Support = -> [XY_Plane011]
  expr: Constraints[1] = Sketch.Constraints.max_r * 2 + 5 mm
  sketch-geometry (1):
    g0: Circle CenterX=0 CenterY=0 CenterZ=0 NormalX=0 NormalY=0 NormalZ=1 AngleXU=0 Radius=354.67
  constraints (2):
    c: Coincident(g0,g-1)
    c: Diameter(g0) = 709.34
FEATURE [Sketcher::SketchObject] Sketch051
  FullyConstrained = true
  MapMode = 5
  Support = -> [XY_Plane007]
  expr: Constraints[11] = Sketch.Constraints.petal_connection_distance
  expr: Constraints[18] = <<main>>.end_face_width / 2
  expr: Constraints[2] = Sketch.Constraints.max_r * 2 - 70 mm
  sketch-geometry (8):
    g0: ArcOfCircle CenterX=0 CenterY=0 CenterZ=0 NormalX=0 NormalY=0 NormalZ=1 AngleXU=0 Radius=317.17 StartAngle=0.572643 EndAngle=1.5708
    g1: LineSegment StartX=266.232 StartY=170.452 StartZ=0 EndX=57.1511 EndY=49.7394 EndZ=0
    g2: ArcOfCircle CenterX=0 CenterY=16.7432 CenterZ=0 NormalX=0 NormalY=0 NormalZ=1 AngleXU=0 Radius=65 StartAngle=0.538751 EndAngle=1.5708
    g3: LineSegment StartX=4e-15 StartY=81.7432 StartZ=0 EndX=1.94e-14 EndY=317.17 EndZ=0
    g4: LineSegment StartX=0 StartY=0 StartZ=0 EndX=274.677 EndY=158.585 EndZ=0
    g5: ArcOfCircle CenterX=56.6511 CenterY=50.6054 CenterZ=0 NormalX=0 NormalY=0 NormalZ=1 AngleXU=0 Radius=1 StartAngle=3.68034 EndAngle=5.23599
    g6: ArcOfCircle CenterX=265.732 CenterY=171.318 CenterZ=0 NormalX=0 NormalY=0 NormalZ=1 AngleXU=0 Radius=1 StartAngle=5.23599 EndAngle=6.85583
    g7: GeomPoint X=267.14 Y=170.977 Z=0
  constraints (22):
    c: Coincident(g0,g-1)
    c: PointOnObject(g0,g-2)
    c: Diameter(g0) = 634.34
    c: PointOnObject(g2,g-2)
    c: PointOnObject(g2,g-2)
    c: Coincident(g3,g2)
    c: Coincident(g3,g0)
    c: Coincident(g4,g0)
    c: PointOnObject(g4,g0)
    c: Angle(g-1,g4) = 0.523599
    c: Parallel(g4,g1)
    c: DistanceY(g2) = 16.7432
    c: Tangent(g2,g5) = 1.5708
    c: Tangent(g1,g5) = 1.5708
    c: Tangent(g0,g6) = -1.5708
    c: Tangent(g1,g6) = 1.5708
    c: PointOnObject(g7,g0)
    c: PointOnObject(g7,g1)
    c: Distance(g7,g4) = 14.5
    c: Equal(g6,g5)
    c: Diameter(g5) = 2
    c: Diameter(g2) = 130
FEATURE [PartDesign::Pad] Pad002
  Direction = (0,0,1)
  Length = 3
  Length2 = 10
  Profile = -> Sketch051
  ReferenceAxis = -> Sketch051 [N_Axis]
  Type = 0
FEATURE [PartDesign::SubShapeBinder] Binder004
  BindCopyOnChange = 0
  BindMode = 0
  ClaimChildren = false
  Context = -> Body003005 [Binder004.]
  Fuse = false
  MakeFace = true
  OffsetFill = false
  OffsetIntersection = false
  OffsetJoinType = 0
  OffsetOpenResult = false
  PartialLoad = false
  Relative = false
  Support = -> [Body003004[Pad002.Sketch051.]]
  _Version = 2
FEATURE [PartDesign::Pad] Pad003
  Direction = (0,0,1)
  Length = 3
  Length2 = 10
  Profile = -> Binder004
  Type = 0
FEATURE [PartDesign::Mirrored] Mirrored008
  BaseFeature = -> Pad003
  MirrorPlane = -> YZ_Plane008
  Originals = -> [Pad003]
FEATURE [PartDesign::Body] Body003005  label="cover_back"
  Group = -> [Binder004,Pad003,Mirrored008]
  Origin = -> Origin008
  Tip = -> Mirrored008
FEATURE [Sketcher::SketchObject] Sketch052
  FullyConstrained = true
  MapMode = 5
  Support = -> [XY_Plane009]
  expr: Constraints[18] = <<main>>.end_face_width / 2 + 20 mm
  expr: Constraints[7] = Sketch.Constraints.max_r * 2 - <<main>>.plexiglass_offset * 2
  sketch-geometry (9):
    g0: ArcOfCircle CenterX=0 CenterY=0 CenterZ=0 NormalX=0 NormalY=0 NormalZ=1 AngleXU=0 Radius=342.17 StartAngle=0.627841 EndAngle=1.5708
    g1: ArcOfCircle CenterX=0 CenterY=0 CenterZ=0 NormalX=0 NormalY=0 NormalZ=1 AngleXU=0 Radius=327.17 StartAngle=0.631986 EndAngle=1.5708
    g2: LineSegment StartX=265.286 StartY=193 StartZ=0 EndX=276.608 EndY=199.537 EndZ=0
    g3: LineSegment StartX=0 StartY=0 StartZ=0 EndX=296.328 EndY=171.085 EndZ=0
    g4: ArcOfCircle CenterX=264.786 CenterY=193.866 CenterZ=0 NormalX=0 NormalY=0 NormalZ=1 AngleXU=0 Radius=1 StartAngle=3.77358 EndAngle=5.23599
    g5: ArcOfCircle CenterX=276.108 CenterY=200.403 CenterZ=0 NormalX=0 NormalY=0 NormalZ=1 AngleXU=0 Radius=1 StartAngle=5.23599 EndAngle=6.91103
    g6: GeomPoint X=264.508 Y=192.551 Z=0
    g7: GeomPoint X=277.568 Y=200.091 Z=0
    g8: LineSegment StartX=2e-14 StartY=327.17 StartZ=0 EndX=2.1e-14 EndY=342.17 EndZ=0
  constraints (23):
    c: Coincident(g0,g-1)
    c: PointOnObject(g0,g-2)
    c: Coincident(g1,g0)
    c: PointOnObject(g1,g-2)
    c: Coincident(g3,g0)
    c: PointOnObject(g3,g0)
    c: Parallel(g2,g3)
    c: Diameter(g0) = 684.34
    c: Angle(g-1,g3) = 0.523599
    c: DistanceY(g1,g0) = 15
    c: Tangent(g1,g4) = 1.5708
    c: Tangent(g2,g4) = -1.5708
    c: Tangent(g2,g5) = -1.5708
    c: Tangent(g0,g5) = -1.5708
    c: PointOnObject(g7,g2)
    c: PointOnObject(g6,g2)
    c: PointOnObject(g7,g0)
    c: PointOnObject(g6,g1)
    c: Distance(g7,g3) = 34.5
    c: Equal(g4,g5)
    c: Diameter(g4) = 2
    c: Coincident(g8,g1)
    c: Coincident(g8,g0)
FEATURE [PartDesign::Pad] Pad004
  Direction = (0,0,1)
  Length = 3
  Length2 = 10
  Profile = -> Sketch052
  ReferenceAxis = -> Sketch052 [N_Axis]
  Type = 0
FEATURE [Sketcher::SketchObject] Sketch053
  FullyConstrained = true
  MapMode = 5
  Support = -> [XY_Plane009]
  expr: Constraints[18] = Sketch052.Constraints[18]
  expr: Constraints[20] = Sketch052.Constraints[20]
  expr: Constraints[24] = <<main>>.rivet_d
  expr: Constraints[7] = Sketch052.Constraints[7]
  expr: Constraints[8] = Sketch052.Constraints[8]
  expr: Constraints[9] = Sketch052.Constraints[9]
  sketch-geometry (18):
    g0: ArcOfCircle CenterX=0 CenterY=0 CenterZ=0 NormalX=0 NormalY=0 NormalZ=1 AngleXU=0 Radius=342.17 StartAngle=0.627841 EndAngle=1.5708
    g1: ArcOfCircle CenterX=0 CenterY=0 CenterZ=0 NormalX=0 NormalY=0 NormalZ=1 AngleXU=0 Radius=327.17 StartAngle=0.631986 EndAngle=1.5708
    g2: LineSegment StartX=265.286 StartY=193 StartZ=0 EndX=276.608 EndY=199.537 EndZ=0
    g3: LineSegment StartX=0 StartY=0 StartZ=0 EndX=296.328 EndY=171.085 EndZ=0
    g4: ArcOfCircle CenterX=264.786 CenterY=193.866 CenterZ=0 NormalX=0 NormalY=0 NormalZ=1 AngleXU=0 Radius=1 StartAngle=3.77358 EndAngle=5.23599
    g5: ArcOfCircle CenterX=276.108 CenterY=200.403 CenterZ=0 NormalX=0 NormalY=0 NormalZ=1 AngleXU=0 Radius=1 StartAngle=5.23599 EndAngle=6.91103
    g6: GeomPoint X=264.508 Y=192.551 Z=0
    g7: GeomPoint X=277.568 Y=200.091 Z=0
    g8: Circle CenterX=99.6316 CenterY=319.496 CenterZ=0 NormalX=0 NormalY=0 NormalZ=1 AngleXU=0 Radius=1.7
    g9: Circle CenterX=265.052 CenterY=204.332 CenterZ=0 NormalX=0 NormalY=0 NormalZ=1 AngleXU=0 Radius=1.7
    g10: LineSegment StartX=2.05e-14 StartY=327.17 StartZ=0 EndX=2.05e-14 EndY=334.67 EndZ=0
    g11: LineSegment StartX=2.05e-14 StartY=334.67 StartZ=0 EndX=2.1e-14 EndY=342.17 EndZ=0
    g12: ArcOfCircle CenterX=0 CenterY=0 CenterZ=0 NormalX=0 NormalY=0 NormalZ=1 AngleXU=0 Radius=334.67 StartAngle=0.626869 EndAngle=1.5708
    g13: LineSegment StartX=265.052 StartY=204.332 StartZ=0 EndX=182.342 EndY=261.914 EndZ=0
    g14: LineSegment StartX=182.342 StartY=261.914 StartZ=0 EndX=99.6316 EndY=319.496 EndZ=0
    g15: LineSegment StartX=99.6316 StartY=319.496 StartZ=0 EndX=1.42e-14 EndY=334.67 EndZ=0
    g16: Circle CenterX=-99.6316 CenterY=319.496 CenterZ=0 NormalX=0 NormalY=0 NormalZ=1 AngleXU=0 Radius=1.7
    g17: Circle CenterX=-265.052 CenterY=204.332 CenterZ=0 NormalX=0 NormalY=0 NormalZ=1 AngleXU=0 Radius=1.7
  constraints (47):
    c: Coincident(g0,g-1)
    c: PointOnObject(g0,g-2)
    c: Coincident(g1,g0)
    c: PointOnObject(g1,g-2)
    c: Coincident(g3,g0)
    c: PointOnObject(g3,g0)
    c: Parallel(g2,g3)
    c: Diameter(g0) = 684.34
    c: Angle(g-1,g3) = 0.523599
    c: DistanceY(g1,g0) = 15
    c: Tangent(g1,g4) = 1.5708
    c: Tangent(g2,g4) = -1.5708
    c: Tangent(g2,g5) = -1.5708
    c: Tangent(g0,g5) = -1.5708
    c: PointOnObject(g7,g2)
    c: PointOnObject(g6,g2)
    c: PointOnObject(g7,g0)
    c: PointOnObject(g6,g1)
    c: Distance(g7,g3) = 34.5
    c: Equal(g4,g5)
    c: Diameter(g4) = 2
    c: Coincident(g10,g1)
    c: Coincident(g11,g0)
    c: Equal(g8,g9)
    c: Diameter(g8) = 3.4
    c: Coincident(g10,g11)
    c: Equal(g10,g11)
    c: Vertical(g10)
    c: Coincident(g12,g0)
    c: Coincident(g12,g10)
    c: PointOnObject(g12,g2)
    c: PointOnObject(g9,g12)
    c: PointOnObject(g8,g12)
    c: Coincident(g13,g9)
    c: Coincident(g14,g13)
    c: Coincident(g14,g8)
    c: Coincident(g15,g8)
    c: Coincident(g15,g10)
    c: Equal(g15,g14)
    c: Equal(g14,g13)
    c: Parallel(g13,g14)
    c: Equal(g17,g16)
    c: Equal(g16,g8)
    c: Symmetric(g16,g8,g-2)
    c: Symmetric(g17,g9,g-2)
    c: Distance(g12,g9) = 10
    c: Distance(g9,g8) = 201.561
FEATURE [PartDesign::Mirrored] Mirrored009
  BaseFeature = -> Pad004
  MirrorPlane = -> Sketch052 [V_Axis]
  Originals = -> [Pad004]
  Refine = true
FEATURE [PartDesign::Pocket] Pocket024
  BaseFeature = -> Mirrored009
  Direction = (0,0,-1)
  Length = 5
  Length2 = 5
  Midplane = true
  Profile = -> Sketch053
  ReferenceAxis = -> Sketch053 [N_Axis]
  Type = 1
FEATURE [PartDesign::Body] Body003006  label="plexiglass_holder_top"
  Group = -> [Sketch052,Pad004,Sketch053,Mirrored009,Pocket024]
  Origin = -> Origin009
  Tip = -> Pocket024
FEATURE [PartDesign::SubShapeBinder] Binder005
  BindCopyOnChange = 0
  BindMode = 0
  ClaimChildren = false
  Context = -> Body003004 [Binder005.]
  Fuse = false
  MakeFace = true
  OffsetFill = false
  OffsetIntersection = false
  OffsetJoinType = 0
  OffsetOpenResult = false
  PartialLoad = false
  Relative = false
  Support = -> [Body003006[Pocket024.Sketch053.]]
  _Version = 2
FEATURE [Sketcher::SketchObject] Sketch054
  AttachmentOffset = pos=(0,0,0) rot=(0,0,1;0.523599rad)
  FullyConstrained = true
  MapMode = 5
  Placement = pos=(0,0,0) rot=(0,0,1;0.523599rad)
  Support = -> [XY_Plane007]
  expr: Constraints[12] = <<main>>.rivet_d
  expr: Constraints[18] = <<main>>.end_face_width / 2 + 12 mm
  expr: Constraints[2] = <<cover_holder_corner>>.Constraints.offset
  expr: Constraints[3] = <<cover_holder_corner>>.Constraints.length
  sketch-geometry (9):
    g0: GeomPoint X=71 Y=0 Z=0
    g1: GeomPoint X=205 Y=0 Z=0
    g2: Circle CenterX=85.5 CenterY=26.5 CenterZ=0 NormalX=0 NormalY=0 NormalZ=1 AngleXU=0 Radius=1.7
    g3: Circle CenterX=190.5 CenterY=26.5 CenterZ=0 NormalX=0 NormalY=0 NormalZ=1 AngleXU=0 Radius=1.7
    g4: Circle CenterX=138 CenterY=46.5 CenterZ=0 NormalX=0 NormalY=0 NormalZ=1 AngleXU=0 Radius=1.7
    g5: LineSegment StartX=85.5 StartY=26.5 StartZ=0 EndX=138 EndY=46.5 EndZ=0
    g6: LineSegment StartX=138 StartY=46.5 StartZ=0 EndX=190.5 EndY=26.5 EndZ=0
    g7: LineSegment StartX=71 StartY=0 StartZ=0 EndX=85.5 EndY=26.5 EndZ=0
    g8: LineSegment StartX=190.5 StartY=26.5 StartZ=0 EndX=205 EndY=0 EndZ=0
  constraints (21):
    c: PointOnObject(g0,g-1)
    c: PointOnObject(g1,g-1)
    c: DistanceX(g0) = 71
    c: DistanceX(g0,g1) = 134
    c: Horizontal(g2,g3)
    c: Coincident(g5,g2)
    c: Coincident(g5,g4)
    c: Coincident(g6,g4)
    c: Coincident(g6,g3)
    c: Equal(g6,g5)
    c: Equal(g4,g2)
    c: Equal(g2,g3)
    c: Diameter(g4) = 3.4
    c: Coincident(g7,g0)
    c: Coincident(g7,g2)
    c: Coincident(g8,g3)
    c: Coincident(g8,g1)
    c: Equal(g8,g7)
    c: DistanceY(g2) = 26.5
    c: DistanceY(g2,g4) = 20
    c: DistanceX(g2,g3) = 105
FEATURE [PartDesign::Pocket] Pocket026
  BaseFeature = -> Pad002
  Direction = (0,0,-1)
  Length = 5
  Length2 = 5
  Midplane = true
  Profile = -> Sketch054
  ReferenceAxis = -> Sketch054 [N_Axis]
  Type = 1
FEATURE [PartDesign::Mirrored] Mirrored010
  BaseFeature = -> Pocket026
  MirrorPlane = -> Sketch051 [V_Axis]
  Originals = -> [Pad002,Pocket026]
FEATURE [PartDesign::Pocket] Pocket025
  BaseFeature = -> Mirrored010
  Direction = (0,0,-1)
  Length = 5
  Length2 = 5
  Midplane = true
  Profile = -> Binder005
  Type = 1
FEATURE [PartDesign::Body] Body003004  label="cover_face"
  Group = -> [Sketch051,Pad002,Pocket026,Binder005,Mirrored010,Pocket025,Sketch054]
  Origin = -> Origin007
  Placement = pos=(0,0,0) rot=(0,0,1;1.0472rad)
  Tip = -> Pocket025
FEATURE [PartDesign::SubShapeBinder] Binder006
  BindCopyOnChange = 0
  BindMode = 0
  ClaimChildren = false
  Context = -> Body [Binder006.]
  Fuse = false
  MakeFace = true
  OffsetFill = false
  OffsetIntersection = false
  OffsetJoinType = 0
  OffsetOpenResult = false
  PartialLoad = false
  Placement = pos=(0,0,0) rot=(0,0,1;1.5708rad)
  Relative = false
  Support = -> [Body003004[Pocket026.Sketch054.]]
  _Version = 2
FEATURE [Sketcher::SketchObject] Sketch055  label="basement_hole"
  AttachmentOffset = pos=(300,12.5,0) rot=(0,0,1;0rad)
  FullyConstrained = true
  MapMode = 5
  Placement = pos=(6.38e-14,300,12.5) rot=(0.57735,0.57735,0.57735;2.0944rad)
  Support = -> [YZ_Plane]
  expr: .AttachmentOffset.Base.x = 300 mm
  expr: .AttachmentOffset.Base.y = 12.5
  expr: Constraints[1] = <<main>>.rivet_d
  sketch-geometry (1):
    g0: Circle CenterX=0 CenterY=0 CenterZ=0 NormalX=0 NormalY=0 NormalZ=1 AngleXU=0 Radius=1.7
  constraints (2):
    c: Coincident(g0,g-1)
    c: Diameter(g0) = 3.4
FEATURE [Sketcher::SketchObject] Sketch057
  FullyConstrained = true
  MapMode = 5
  Support = -> [XY_Plane010]
  expr: Constraints[10] = Sketch.Constraints.max_r - <<main>>.plexiglass_offset
  expr: Constraints[16] = <<main>>.end_face_width / 2 + 1 mm
  sketch-geometry (8):
    g0: ArcOfCircle CenterX=0 CenterY=0 CenterZ=0 NormalX=0 NormalY=0 NormalZ=1 AngleXU=0 Radius=322.17 StartAngle=0.577609 EndAngle=1.5708
    g1: ArcOfCircle CenterX=0 CenterY=0 CenterZ=0 NormalX=0 NormalY=0 NormalZ=1 AngleXU=0 Radius=342.17 StartAngle=0.575066 EndAngle=1.5708
    g2: LineSegment StartX=272.58 StartY=175.272 StartZ=0 EndX=286.456 EndY=183.283 EndZ=0
    g3: LineSegment StartX=1.97e-14 StartY=322.17 StartZ=0 EndX=2.1e-14 EndY=342.17 EndZ=0
    g4: LineSegment StartX=0 StartY=0 StartZ=0 EndX=296.328 EndY=171.085 EndZ=0
    g5: ArcOfCircle CenterX=285.456 CenterY=185.015 CenterZ=0 NormalX=0 NormalY=0 NormalZ=1 AngleXU=0 Radius=2 StartAngle=5.23599 EndAngle=6.85825
    g6: GeomPoint X=288.274 Y=184.333 Z=0
    g7: ArcOfCircle CenterX=271.58 CenterY=177.004 CenterZ=0 NormalX=0 NormalY=0 NormalZ=1 AngleXU=0 Radius=2 StartAngle=3.7192 EndAngle=5.23599
  constraints (21):
    c: Coincident(g0,g-1)
    c: PointOnObject(g0,g-2)
    c: Coincident(g1,g0)
    c: PointOnObject(g1,g-2)
    c: Coincident(g3,g0)
    c: Coincident(g3,g1)
    c: Coincident(g4,g0)
    c: Angle(g-1,g4) = 0.523599
    c: PointOnObject(g4,g1)
    c: Parallel(g2,g4)
    c: DistanceY(g1) = 342.17
    c: DistanceY(g0,g1) = 20
    c: Tangent(g1,g5) = -1.5708
    c: Tangent(g2,g5) = -1.5708
    c: PointOnObject(g6,g1)
    c: PointOnObject(g6,g2)
    c: Distance(g6,g4) = 15.5
    c: Tangent(g0,g7) = 1.5708
    c: Tangent(g2,g7) = -1.5708
    c: Equal(g7,g5)
    c: Diameter(g7) = 4
FEATURE [Sketcher::SketchObject] Sketch058
  FullyConstrained = true
  MapMode = 5
  Support = -> [XY_Plane010]
  expr: Constraints[10] = Sketch057.Constraints[10]
  expr: Constraints[11] = Sketch057.Constraints[11]
  expr: Constraints[16] = Sketch057.Constraints[16]
  expr: Constraints[20] = Sketch057.Constraints[20]
  expr: Constraints[31] = <<main>>.rivet_d
  expr: Constraints[7] = Sketch057.Constraints[7]
  sketch-geometry (17):
    g0: ArcOfCircle CenterX=0 CenterY=0 CenterZ=0 NormalX=0 NormalY=0 NormalZ=1 AngleXU=0 Radius=322.17 StartAngle=0.577609 EndAngle=1.5708
    g1: ArcOfCircle CenterX=0 CenterY=0 CenterZ=0 NormalX=0 NormalY=0 NormalZ=1 AngleXU=0 Radius=342.17 StartAngle=0.575066 EndAngle=1.5708
    g2: LineSegment StartX=272.58 StartY=175.272 StartZ=0 EndX=286.456 EndY=183.283 EndZ=0
    g3: LineSegment StartX=0 StartY=0 StartZ=0 EndX=296.328 EndY=171.085 EndZ=0
    g4: ArcOfCircle CenterX=285.456 CenterY=185.015 CenterZ=0 NormalX=0 NormalY=0 NormalZ=1 AngleXU=0 Radius=2 StartAngle=5.23599 EndAngle=6.85825
    g5: GeomPoint X=288.274 Y=184.333 Z=0
    g6: ArcOfCircle CenterX=271.58 CenterY=177.004 CenterZ=0 NormalX=0 NormalY=0 NormalZ=1 AngleXU=0 Radius=2 StartAngle=3.7192 EndAngle=5.23599
    g7: LineSegment StartX=1.97e-14 StartY=322.17 StartZ=0 EndX=2.03e-14 EndY=332.17 EndZ=0
    g8: LineSegment StartX=2.03e-14 StartY=332.17 StartZ=0 EndX=2.1e-14 EndY=342.17 EndZ=0
    g9: Circle CenterX=105.577 CenterY=314.945 CenterZ=0 NormalX=0 NormalY=0 NormalZ=1 AngleXU=0 Radius=1.7
    g10: Circle CenterX=274.069 CenterY=187.679 CenterZ=0 NormalX=0 NormalY=0 NormalZ=1 AngleXU=0 Radius=1.7
    g11: ArcOfCircle CenterX=0 CenterY=0 CenterZ=0 NormalX=0 NormalY=0 NormalZ=1 AngleXU=0 Radius=332.17 StartAngle=0.570279 EndAngle=1.5708
    g12: LineSegment StartX=274.069 StartY=187.679 StartZ=0 EndX=189.823 EndY=251.312 EndZ=0
    g13: LineSegment StartX=189.823 StartY=251.312 StartZ=0 EndX=105.577 EndY=314.945 EndZ=0
    g14: LineSegment StartX=105.577 StartY=314.945 StartZ=0 EndX=0 EndY=314.945 EndZ=0
    g15: Circle CenterX=-105.577 CenterY=314.945 CenterZ=0 NormalX=0 NormalY=0 NormalZ=1 AngleXU=0 Radius=1.7
    g16: Circle CenterX=-274.069 CenterY=187.679 CenterZ=0 NormalX=0 NormalY=0 NormalZ=1 AngleXU=0 Radius=1.7
  constraints (45):
    c: Coincident(g0,g-1)
    c: PointOnObject(g0,g-2)
    c: Coincident(g1,g0)
    c: PointOnObject(g1,g-2)
    c: Coincident(g7,g0)
    c: Coincident(g8,g1)
    c: Coincident(g3,g0)
    c: Angle(g-1,g3) = 0.523599
    c: PointOnObject(g3,g1)
    c: Parallel(g2,g3)
    c: DistanceY(g1) = 342.17
    c: DistanceY(g0,g1) = 20
    c: Tangent(g1,g4) = -1.5708
    c: Tangent(g2,g4) = -1.5708
    c: PointOnObject(g5,g1)
    c: PointOnObject(g5,g2)
    c: Distance(g5,g3) = 15.5
    c: Tangent(g0,g6) = 1.5708
    c: Tangent(g2,g6) = -1.5708
    c: Equal(g6,g4)
    c: Diameter(g6) = 4
    c: Coincident(g7,g8)
    c: Parallel(g7,g8)
    c: Equal(g8,g7)
    c: Equal(g9,g10)
    c: Distance(g10,g2) = 10
    c: Coincident(g11,g0)
    c: Coincident(g11,g7)
    c: PointOnObject(g11,g2)
    c: PointOnObject(g10,g11)
    c: PointOnObject(g9,g11)
    c: Diameter(g9) = 3.4
    c: Coincident(g12,g10)
    c: Coincident(g13,g12)
    c: Coincident(g13,g9)
    c: Coincident(g14,g9)
    c: PointOnObject(g14,g-2)
    c: Horizontal(g14)
    c: Parallel(g12,g13)
    c: Equal(g13,g12)
    c: Equal(g12,g14)
    c: Equal(g9,g15)
    c: Equal(g15,g16)
    c: Symmetric(g15,g9,g-2)
    c: Symmetric(g10,g16,g-2)
FEATURE [PartDesign::Pad] Pad005
  Direction = (0,0,1)
  Length = 3
  Length2 = 10
  Profile = -> Sketch057
  ReferenceAxis = -> Sketch057 [N_Axis]
  Type = 0
  expr: Length = <<main>>.thickness
FEATURE [PartDesign::Mirrored] Mirrored011
  BaseFeature = -> Pad005
  MirrorPlane = -> Sketch057 [V_Axis]
  Originals = -> [Pad005]
  Refine = true
FEATURE [PartDesign::Pocket] Pocket029
  BaseFeature = -> Mirrored011
  Direction = (0,0,-1)
  Length = 5
  Length2 = 5
  Midplane = true
  Profile = -> Sketch058
  ReferenceAxis = -> Sketch058 [N_Axis]
  Type = 1
FEATURE [PartDesign::Pad] Pad006
  Direction = (0,0,1)
  Length = 12
  Length2 = 10
  Profile = -> Sketch050
  ReferenceAxis = -> Sketch050 [N_Axis]
  Type = 0
FEATURE [Sketcher::SketchObject] Sketch059
  FullyConstrained = true
  MapMode = 5
  Support = -> [XY_Plane011]
  expr: Constraints[29] = (76.75 mm + 96.16 mm) / 2
  expr: Constraints[30] = (37.9 mm + 58.4 mm) / 2
  sketch-geometry (12):
    g0: Circle CenterX=43.2275 CenterY=24.075 CenterZ=0 NormalX=0 NormalY=0 NormalZ=1 AngleXU=0 Radius=4.25
    g1: Circle CenterX=-43.2275 CenterY=-24.075 CenterZ=0 NormalX=0 NormalY=0 NormalZ=1 AngleXU=0 Radius=4.25
    g2: Circle CenterX=-43.2275 CenterY=24.075 CenterZ=0 NormalX=0 NormalY=0 NormalZ=1 AngleXU=0 Radius=4.25
    g3: Circle CenterX=43.2275 CenterY=-24.075 CenterZ=0 NormalX=0 NormalY=0 NormalZ=1 AngleXU=0 Radius=4.25
    g4: LineSegment StartX=-39.5145 StartY=-22.0071 StartZ=0 EndX=39.5145 EndY=22.0071 EndZ=0
    g5: Circle CenterX=0 CenterY=0 CenterZ=0 NormalX=0 NormalY=0 NormalZ=1 AngleXU=0 Radius=28.5
    g6: LineSegment StartX=43.2275 StartY=-28.325 StartZ=0 EndX=43.2275 EndY=19.825 EndZ=0
    g7: LineSegment StartX=-47.4775 StartY=24.075 StartZ=0 EndX=38.9775 EndY=24.075 EndZ=0
    g8: GeomPoint X=43.2275 Y=-28.325 Z=0
    g9: GeomPoint X=43.2275 Y=28.325 Z=0
    g10: GeomPoint X=-47.4775 Y=24.075 Z=0
    g11: GeomPoint X=47.4775 Y=24.075 Z=0
  constraints (33):
    c: Diameter(g0) = 8.5
    c: Equal(g0,g1)
    c: Equal(g1,g2)
    c: Equal(g2,g3)
    c: Symmetric(g1,g0,g-1)
    c: PointOnObject(g4,g1)
    c: PointOnObject(g4,g0)
    c: PointOnObject(g0,g4)
    c: PointOnObject(g1,g4)
    c: Coincident(g5,g-1)
    c: Diameter(g5) = 57
    c: PointOnObject(g6,g3)
    c: PointOnObject(g6,g0)
    c: Vertical(g6)
    c: PointOnObject(g3,g6)
    c: PointOnObject(g0,g6)
    c: PointOnObject(g7,g2)
    c: PointOnObject(g7,g0)
    c: Horizontal(g7)
    c: PointOnObject(g0,g7)
    c: PointOnObject(g2,g7)
    c: PointOnObject(g8,g3)
    c: PointOnObject(g9,g0)
    c: PointOnObject(g10,g2)
    c: PointOnObject(g11,g0)
    c: Vertical(g8,g6)
    c: Vertical(g6,g9)
    c: Horizontal(g11,g7)
    c: Horizontal(g7,g10)
    c: DistanceX(g2,g0) = 86.455
    c: DistanceY(g3,g0) = 48.15
    c: Vertical(g1,g2)
    c: Horizontal(g1,g3)
FEATURE [PartDesign::Pocket] Pocket030
  BaseFeature = -> Pad006
  Direction = (0,0,-1)
  Length = 5
  Length2 = 5
  Midplane = true
  Profile = -> Sketch059
  ReferenceAxis = -> Sketch059 [N_Axis]
  Type = 1
FEATURE [Sketcher::SketchObject] Sketch060
  AttachmentOffset = pos=(27,300,12) rot=(0,0,1;0rad)
  FullyConstrained = true
  MapMode = 5
  Placement = pos=(27,300,12) rot=(0,0,1;0rad)
  Support = -> [XY_Plane011]
  expr: .AttachmentOffset.Base.x = <<main>>.end_face_width / 2 + 12.5 mm
  expr: .AttachmentOffset.Base.y = <<basement_hole>>.AttachmentOffset.Base.x
  expr: .AttachmentOffset.Base.z = Pad006.Length
  sketch-geometry (1):
    g0: Circle CenterX=0 CenterY=0 CenterZ=0 NormalX=0 NormalY=0 NormalZ=1 AngleXU=0 Radius=3
  constraints (2):
    c: Coincident(g0,g-1)
    c: Diameter(g0) = 6
FEATURE [PartDesign::Pocket] Pocket031
  BaseFeature = -> Pocket030
  Direction = (0,0,-1)
  Length = 3
  Length2 = 5
  Profile = -> Sketch060
  ReferenceAxis = -> Sketch060 [N_Axis]
  Type = 0
FEATURE [PartDesign::Mirrored] Mirrored012
  MirrorPlane = -> YZ_Plane011
FEATURE [PartDesign::PolarPattern] PolarPattern007
  Angle = 360
  Axis = -> Z_Axis011
  Occurrences = 3
FEATURE [PartDesign::MultiTransform] MultiTransform006
  BaseFeature = -> Pocket031
  Originals = -> [Pocket031]
  Transformations = -> [Mirrored012,PolarPattern007]
FEATURE [PartDesign::SubShapeBinder] Binder007
  BindCopyOnChange = 0
  BindMode = 0
  ClaimChildren = false
  Context = -> Body003008 [Binder007.]
  Fuse = false
  MakeFace = true
  Offset = 1.3
  OffsetFill = false
  OffsetIntersection = false
  OffsetJoinType = 0
  OffsetOpenResult = false
  PartialLoad = false
  Placement = pos=(0,0,12) rot=(0,0,1;1.0472rad)
  Relative = false
  Support = -> [Body003007[Pocket029.Sketch058.]]
  _Version = 2
  expr: .Placement.Base.z = Pad006.Length
  expr: Offset = (6 mm - <<main>>.rivet_d) / 2
FEATURE [PartDesign::Pocket] Pocket032
  BaseFeature = -> MultiTransform006
  Direction = (0,0,-1)
  Length = 3
  Length2 = 5
  Profile = -> Binder007
  Type = 0
FEATURE [PartDesign::PolarPattern] PolarPattern008
  Angle = 120
  Axis = -> Z_Axis011
  BaseFeature = -> Pocket032
  Occurrences = 2
  Originals = -> [Pocket032]
  Reversed = true
FEATURE [PartDesign::CoordinateSystem] bottom
  AttacherType = Attacher::AttachEngine3D
  Support = -> [XY_Plane011]
FEATURE [PartDesign::CoordinateSystem] basement_top
  AttacherType = Attacher::AttachEngine3D
  AttachmentOffset = pos=(0,0,12) rot=(0,0,1;0rad)
  MapMode = 5
  Placement = pos=(0,0,12) rot=(0,0,1;0rad)
  Support = -> [XY_Plane011]
  expr: .AttachmentOffset.Base.z = Pad006.Length
FEATURE [PartDesign::Body] Body003008  label="basement"
  Group = -> [Sketch050,Pad006,Sketch059,Pocket030,Sketch060,Pocket031,MultiTransform006,Mirrored012,PolarPattern007,Binder007,Pocket032,PolarPattern008,bottom,basement_top]
  Origin = -> Origin011
  Tip = -> PolarPattern008
FEATURE [PartDesign::CoordinateSystem] LCS_0001
  AttacherType = Attacher::AttachEngine3D
  MapMode = 2
  Support = -> [X_Axis012]
FEATURE [Sketcher::SketchObject] Sketch_1
  FullyConstrained = true
  Support = -> [XY_Plane012]
  sketch-geometry (1):
    g0: Circle CenterX=0 CenterY=0 CenterZ=0 NormalX=0 NormalY=0 NormalZ=1 AngleXU=0 Radius=354.515
  constraints (2):
    c: Coincident(g0,g-1)
    c: Diameter(g0) = 709.03
FEATURE [PartDesign::Pad] Pad007
  Direction = (0,0,1)
  Length = 0.5
  Length2 = 10
  Profile = -> Sketch_1
  ReferenceAxis = -> Sketch_1 [N_Axis]
  Type = 0
FEATURE [PartDesign::CoordinateSystem] Local_CS012  label="basement_stainless_steel_top"
  AttacherType = Attacher::AttachEngine3D
  AttachmentOffset = pos=(0,0,0.5) rot=(0,0,1;0rad)
  MapMode = 5
  Placement = pos=(0,0,0.5) rot=(0,0,1;0rad)
  Support = -> [XY_Plane012]
  expr: .AttachmentOffset.Base.z = Pad007.Length
FEATURE [PartDesign::Body] basement_stainless_steel
  Group = -> [LCS_0001,Sketch_1,Pad007,Local_CS012]
  Origin = -> Origin012
  Tip = -> Pad007
FEATURE [PartDesign::CoordinateSystem] Local_CS013  label="plexiglass_holder_center"
  AttacherType = Attacher::AttachEngine3D
  MapMode = 5
  Support = -> [XY_Plane010]
FEATURE [PartDesign::Body] Body003007  label="plexiglass_holder_bottom"
  Group = -> [Sketch057,Sketch058,Pad005,Mirrored011,Pocket029,Local_CS013]
  Origin = -> Origin010
  Tip = -> Pocket029
FEATURE [Sketcher::SketchObject] Sketch062
  FullyConstrained = true
  MapMode = 5
  Support = -> [XY_Plane]
  expr: Constraints[2] = <<main>>.rivet_d
  sketch-geometry (2):
    g0: Circle CenterX=-50 CenterY=0 CenterZ=0 NormalX=0 NormalY=0 NormalZ=1 AngleXU=0 Radius=1.7
    g1: Circle CenterX=50 CenterY=0 CenterZ=0 NormalX=0 NormalY=0 NormalZ=1 AngleXU=0 Radius=1.7
  constraints (5):
    c: PointOnObject(g1,g-1)
    c: Equal(g0,g1)
    c: Diameter(g1) = 3.4
    c: Symmetric(g1,g0,g-2)
    c: DistanceX(g0,g1) = 100
FEATURE [PartDesign::Line] DatumLine003
  AttacherType = Attacher::AttachEngineLine
  AttachmentOffset = pos=(0,0,0) rot=(0,1,0;0.523599rad)
  Length = 20
  MapMode = 16
  Placement = pos=(0,0,0) rot=(0.377964,0.654654,0.654654;2.41886rad)
  ResizeMode = 0
  Support = -> [XY_Plane]
FEATURE [PartDesign::Plane] DatumPlane009
  AttachmentOffset = pos=(14.5,-138,410) rot=(0,0,1;-1.5708rad)
  Length = 200
  MapMode = 3
  Placement = pos=(-112.262,-81.5574,410) rot=(0,0,1;3.66519rad)
  ResizeMode = 1
  Support = -> [DatumLine003]
  Width = 200
  expr: .AttachmentOffset.Base.x = <<main>>.end_face_width / 2
  expr: .AttachmentOffset.Base.y = -<<cover_holder_corner>>.Constraints.offset - <<cover_holder_corner>>.Constraints.length / 2
  expr: .AttachmentOffset.Base.z = <<main>>.basin_height
FEATURE [Sketcher::SketchObject] Sketch063
  FullyConstrained = true
  MapMode = 5
  Placement = pos=(-112.262,-81.5574,410) rot=(0,0,1;3.66519rad)
  Support = -> [DatumPlane009]
  expr: Constraints[2] = <<main>>.rivet_d
  sketch-geometry (2):
    g0: Circle CenterX=36 CenterY=14 CenterZ=0 NormalX=0 NormalY=0 NormalZ=1 AngleXU=0 Radius=1.7
    g1: Circle CenterX=-36 CenterY=14 CenterZ=0 NormalX=0 NormalY=0 NormalZ=1 AngleXU=0 Radius=1.7
  constraints (5):
    c: Equal(g0,g1)
    c: DistanceX(g1,g0) = 72
    c: Diameter(g0) = 3.4
    c: DistanceY(g0) = 14
    c: Symmetric(g0,g1,g-2)
FEATURE [PartDesign::PolarPattern] PolarPattern009
  Angle = 90
  Axis = -> Sketch063 [H_Axis]
  Occurrences = 2
FEATURE [PartDesign::Mirrored] Mirrored013
  MirrorPlane = -> YZ_Plane
FEATURE [PartDesign::SubShapeBinder] Binder008
  BindCopyOnChange = 0
  BindMode = 0
  ClaimChildren = false
  Context = -> Body [Binder008.]
  Fuse = false
  MakeFace = true
  OffsetFill = false
  OffsetIntersection = false
  OffsetJoinType = 0
  OffsetOpenResult = false
  PartialLoad = false
  Relative = true
  Support = -> [Body003[Pocket013.Sketch039.]]
  _Version = 2
FEATURE [Sketcher::SketchObject] Sketch064
  AttachmentOffset = pos=(19,958,0) rot=(0,0,1;0rad)
  FullyConstrained = true
  MapMode = 5
  Placement = pos=(16.4545,-9.5,958) rot=(0.935113,-0.250563,-0.250563;1.63783rad)
  Support = -> [DatumPlane007]
  expr: Constraints[0] = <<main>>.rivet_d
  sketch-geometry (6):
    g0: Circle CenterX=0 CenterY=425 CenterZ=0 NormalX=0 NormalY=0 NormalZ=1 AngleXU=0 Radius=1.7
    g1: Circle CenterX=0 CenterY=-425 CenterZ=0 NormalX=0 NormalY=0 NormalZ=1 AngleXU=0 Radius=1.7
    g2: Circle CenterX=0 CenterY=255 CenterZ=0 NormalX=0 NormalY=0 NormalZ=1 AngleXU=0 Radius=1.7
    g3: Circle CenterX=0 CenterY=85 CenterZ=0 NormalX=0 NormalY=0 NormalZ=1 AngleXU=0 Radius=1.7
    g4: Circle CenterX=0 CenterY=-85 CenterZ=0 NormalX=0 NormalY=0 NormalZ=1 AngleXU=0 Radius=1.7
    g5: Circle CenterX=0 CenterY=-255 CenterZ=0 NormalX=0 NormalY=0 NormalZ=1 AngleXU=0 Radius=1.7
  constraints (13):
    c: Diameter(g0) = 3.4
    c: PointOnObject(g0,g-2)
    c: Symmetric(g0,g3,g2)
    c: Symmetric(g2,g4,g3)
    c: Equal(g1,g4)
    c: Equal(g4,g3)
    c: Equal(g3,g2)
    c: Equal(g2,g0)
    c: Symmetric(g5,g3,g4)
    c: Equal(g5,g1)
    c: Symmetric(g1,g4,g5)
    c: DistanceY(g1,g0) = 850
    c: Symmetric(g1,g0,g-1)
FEATURE [PartDesign::Plane] DatumPlane010
  Length = 717.412
  MapMode = 4
  Placement = pos=(0,181.372,1428) rot=(0.57735,0.57735,0.57735;2.0944rad)
  ResizeMode = 0
  Support = -> [Local_CS002]
  Width = 1630.19
FEATURE [Sketcher::SketchObject] Sketch005
  AttachmentOffset = pos=(0,-28,0) rot=(0,0,1;0rad)
  FullyConstrained = true
  MapMode = 5
  Placement = pos=(0,181.372,1400) rot=(0.57735,0.57735,0.57735;2.0944rad)
  Support = -> [DatumPlane010]
  expr: .AttachmentOffset.Base.y = -<<dropper>>.center_height_offset - <<main>>.distance_gutter_holes_dropper_cutout
  expr: Constraints[1] = <<main>>.rivet_d
  expr: Constraints[7] = Local_CS003.AttachmentOffset.Base.y
  sketch-geometry (6):
    g0: Circle CenterX=0 CenterY=0 CenterZ=0 NormalX=0 NormalY=0 NormalZ=1 AngleXU=0 Radius=1.7
    g1: Circle CenterX=-126.5 CenterY=0 CenterZ=0 NormalX=0 NormalY=0 NormalZ=1 AngleXU=0 Radius=1.7
    g2: Circle CenterX=126.5 CenterY=0 CenterZ=0 NormalX=0 NormalY=0 NormalZ=1 AngleXU=0 Radius=1.7
    g3: Circle CenterX=23.5 CenterY=0 CenterZ=0 NormalX=0 NormalY=0 NormalZ=1 AngleXU=0 Radius=1.7
    g4: Circle CenterX=-23.5 CenterY=0 CenterZ=0 NormalX=0 NormalY=0 NormalZ=1 AngleXU=0 Radius=1.7
    g5: GeomPoint X=-75 Y=0 Z=0
  constraints (13):
    c: Coincident(g0,g-1)
    c: Diameter(g0) = 3.4
    c: PointOnObject(g1,g-1)
    c: Symmetric(g1,g2,g-2)
    c: Equal(g1,g2)
    c: Equal(g2,g0)
    c: PointOnObject(g3,g-1)
    c: DistanceX(g5) = -75
    c: Equal(g4,g1)
    c: Equal(g3,g0)
    c: Symmetric(g4,g3,g-2)
    c: DistanceX(g5,g4) = 51.5
    c: Symmetric(g1,g4,g5)
FEATURE [Sketcher::SketchObject] Sketch069
  FullyConstrained = true
  MapMode = 5
  Placement = pos=(0,0,0) rot=(0.935113,-0.250563,-0.250563;1.63783rad)
  Support = -> [DatumPlane007]
  expr: .Constraints.offset = Sketch043.Constraints[10]
  expr: Constraints[11] = Sketch043.Constraints[11]
  expr: Constraints[24] = Sketch043.Constraints[25]
  expr: Constraints[25] = Sketch043.Constraints.length / sin(60)
  expr: Constraints[8] = Sketch043.Constraints[8]
  expr: Constraints[9] = Sketch043.Constraints[9]
  sketch-geometry (11):
    g0: LineSegment StartX=71 StartY=360 StartZ=0 EndX=71 EndY=410 EndZ=0
    g1: LineSegment StartX=71 StartY=410 StartZ=0 EndX=205 EndY=410 EndZ=0
    g2: LineSegment StartX=205 StartY=410 StartZ=0 EndX=205 EndY=360 EndZ=0
    g3: LineSegment StartX=205 StartY=360 StartZ=0 EndX=71 EndY=360 EndZ=0
    g4: LineSegment StartX=0 StartY=-10 StartZ=0 EndX=242.487 EndY=-10 EndZ=0
    g5: LineSegment StartX=242.487 StartY=-10 StartZ=0 EndX=242.487 EndY=400 EndZ=0
    g6: LineSegment StartX=0 StartY=410 StartZ=0 EndX=0 EndY=-10 EndZ=0
    g7: LineSegment StartX=232.487 StartY=410 StartZ=0 EndX=205 EndY=410 EndZ=0
    g8: LineSegment StartX=71 StartY=410 StartZ=0 EndX=0 EndY=410 EndZ=0
    g9: ArcOfCircle CenterX=232.487 CenterY=400 CenterZ=0 NormalX=0 NormalY=0 NormalZ=1 AngleXU=0 Radius=10 StartAngle=-9e-16 EndAngle=1.5708
    g10: GeomPoint X=242.487 Y=410 Z=0
  constraints (31):
    c: Coincident(g0,g1)
    c: Coincident(g1,g2)
    c: Coincident(g2,g3)
    c: Coincident(g3,g0)
    c: Horizontal(g1)
    c: Horizontal(g3)
    c: Vertical(g0)
    c: Vertical(g2)
    c: DistanceY(g1) = 410
    c: DistanceY(g2,g2) = 50
    c: DistanceX(g0) = 71  'offset'
    c: DistanceX(g1) = 205
    c: DistanceX(g3,g3) = 134  'length'
    c: Coincident(g4,g5)
    c: Coincident(g8,g6)
    c: Coincident(g6,g4)
    c: Horizontal(g4)
    c: Vertical(g5)
    c: Vertical(g6)
    c: PointOnObject(g4,g-2)
    c: Horizontal(g7)
    c: Horizontal(g8)
    c: Coincident(g7,g1)
    c: Coincident(g8,g0)
    c: DistanceY(g4) = -10
    c: DistanceX(g10) = 242.487
    c: PointOnObject(g10,g7)
    c: PointOnObject(g10,g5)
    c: Tangent(g7,g9) = -1.5708
    c: Tangent(g5,g9) = -1.5708
    c: Diameter(g9) = 20
FEATURE [PartDesign::Plane] DatumPlane011
  AttachmentOffset = pos=(0,0,0) rot=(0,1,0;0.523599rad)
  Length = 1027.22
  MapMode = 3
  Placement = pos=(0,0,0) rot=(0.935113,0.250563,0.250563;1.63783rad)
  ResizeMode = 0
  Support = -> [XY_Plane]
  Width = 1670
FEATURE [Sketcher::SketchObject] Sketch070
  FullyConstrained = true
  MapMode = 5
  Placement = pos=(0,0,0) rot=(0.935113,0.250563,0.250563;1.63783rad)
  Support = -> [DatumPlane011]
  expr: Constraints[0] = -Sketch.Constraints.petal_offset
  expr: Constraints[1] = <<main>>.total_length
  expr: Constraints[24] = 3
  expr: Constraints[25] = Sketch047.Constraints.bottom
  expr: Constraints[26] = Sketch047.Constraints.top
  sketch-geometry (9):
    g0: LineSegment StartX=-8.37158 StartY=1428 StartZ=0 EndX=-5.37158 EndY=1425 EndZ=0
    g1: LineSegment StartX=-8.37158 StartY=1428 StartZ=0 EndX=0 EndY=1428 EndZ=0
    g2: LineSegment StartX=-5.37158 StartY=1425 StartZ=0 EndX=-5.37158 EndY=1378 EndZ=0
    g3: LineSegment StartX=-5.37158 StartY=1378 StartZ=0 EndX=0 EndY=1378 EndZ=0
    g4: LineSegment StartX=0 StartY=1378 StartZ=0 EndX=0 EndY=1428 EndZ=0
    g5: LineSegment StartX=0 StartY=510 StartZ=0 EndX=-5.37158 EndY=510 EndZ=0
    g6: LineSegment StartX=-5.37158 StartY=510 StartZ=0 EndX=-5.37158 EndY=0 EndZ=0
    g7: LineSegment StartX=-5.37158 StartY=0 StartZ=0 EndX=0 EndY=0 EndZ=0
    g8: LineSegment StartX=0 StartY=0 StartZ=0 EndX=0 EndY=510 EndZ=0
  constraints (27):
    c: DistanceX(g0) = -8.37158
    c: DistanceY(g0) = 1428
    c: Angle(g0,g-2) = 2.35619
    c: Coincident(g1,g0)
    c: PointOnObject(g1,g-2)
    c: Horizontal(g1)
    c: Coincident(g2,g0)
    c: Vertical(g2)
    c: Coincident(g3,g2)
    c: PointOnObject(g3,g-2)
    c: Horizontal(g3)
    c: Coincident(g4,g3)
    c: Coincident(g4,g1)
    c: Coincident(g5,g6)
    c: Coincident(g6,g7)
    c: Coincident(g7,g8)
    c: Coincident(g8,g5)
    c: Horizontal(g5)
    c: Horizontal(g7)
    c: Vertical(g6)
    c: Vertical(g8)
    c: PointOnObject(g5,g-2)
    c: PointOnObject(g6,g-1)
    c: Vertical(g5,g2)
    c: DistanceX(g0,g0) = 3
    c: DistanceY(g5) = 510
    c: DistanceY(g3,g1) = 50
FEATURE [PartDesign::Pocket] Pocket
  BaseFeature = -> Pocket021
  Direction = (-0.5,0.866025,-1e-16)
  Length = 14.569
  Length2 = 5
  Profile = -> Sketch070
  ReferenceAxis = -> Sketch070 [N_Axis]
  Refine = true
  Reversed = true
  Type = 0
  expr: Length = <<main>>.end_face_width / 2 + 0.06900000000000001 mm
FEATURE [PartDesign::Pocket] Pocket042
  BaseFeature = -> Pocket
  Direction = (0,0,-1)
  Length = 5
  Length2 = 5
  Midplane = true
  Profile = -> Sketch049
  ReferenceAxis = -> Sketch049 [N_Axis]
  Type = 1
FEATURE [PartDesign::Pocket] Pocket039
  BaseFeature = -> Pocket042
  Direction = (0.5,0.866025,-1e-16)
  Length = 5
  Length2 = 5
  Profile = -> Sketch064
  ReferenceAxis = -> Sketch064 [N_Axis]
  Reversed = true
  Type = 1
FEATURE [PartDesign::Pocket] Pocket027
  BaseFeature = -> Pocket039
  Direction = (0,0,-1)
  Length = 5
  Length2 = 5
  Midplane = true
  Profile = -> Binder006
  Type = 1
FEATURE [PartDesign::MultiTransform] MultiTransform005
  BaseFeature = -> Pocket027
  Originals = -> [Pocket027,Pocket042]
  Transformations = -> [PolarPattern005,Mirrored006]
FEATURE [PartDesign::Pocket] Pocket033
  BaseFeature = -> MultiTransform005
  Direction = (0,0,-1)
  Length = 5
  Length2 = 5
  Profile = -> Sketch063
  ReferenceAxis = -> Sketch063 [N_Axis]
  Type = 4
FEATURE [PartDesign::MultiTransform] MultiTransform007
  BaseFeature = -> Pocket033
  Originals = -> [Pocket033]
  Transformations = -> [PolarPattern009,Mirrored013]
FEATURE [Sketcher::SketchObject] Sketch061
  FullyConstrained = true
  MapMode = 5
  Support = -> [XY_Plane]
  sketch-geometry (8):
    g0: ArcOfCircle CenterX=18.68 CenterY=-5 CenterZ=0 NormalX=0 NormalY=0 NormalZ=1 AngleXU=0 Radius=5 StartAngle=0 EndAngle=1.57079
    g1: ArcOfCircle CenterX=-18.68 CenterY=-5 CenterZ=0 NormalX=0 NormalY=0 NormalZ=1 AngleXU=0 Radius=5 StartAngle=1.5708 EndAngle=3.14159
    g2: LineSegment StartX=-23.68 StartY=-5 StartZ=0 EndX=-23.68 EndY=0 EndZ=0
    g3: LineSegment StartX=-23.68 StartY=0 StartZ=0 EndX=-18.68 EndY=0 EndZ=0
    g4: LineSegment StartX=18.68 StartY=-6.05453e-11 StartZ=0 EndX=23.68 EndY=0 EndZ=0
    g5: LineSegment StartX=23.68 StartY=0 StartZ=0 EndX=23.68 EndY=-5 EndZ=0
    g6: LineSegment StartX=-18.68 StartY=-5 StartZ=0 EndX=0 EndY=-5 EndZ=0
    g7: LineSegment StartX=0 StartY=-5 StartZ=0 EndX=18.68 EndY=-5 EndZ=0
  constraints (23):
    c: PointOnObject(g0,g-1)
    c: PointOnObject(g1,g-1)
    c: Coincident(g2,g1)
    c: PointOnObject(g2,g-1)
    c: Vertical(g2)
    c: Tangent(g2,g1)
    c: Coincident(g3,g2)
    c: Coincident(g4,g0)
    c: PointOnObject(g4,g-1)
    c: Tangent(g4,g0)
    c: Coincident(g5,g4)
    c: Vertical(g5)
    c: Tangent(g3,g1) = 1.5708
    c: Equal(g1,g0)
    c: Coincident(g6,g1)
    c: PointOnObject(g6,g-2)
    c: Horizontal(g6)
    c: Coincident(g7,g6)
    c: Coincident(g7,g0)
    c: Equal(g7,g6)
    c: Diameter(g0) = 10
    c: DistanceX(g1,g0) = 37.36
    c: Tangent(g5,g0) = 1.5708
FEATURE [Sketcher::SketchObject] Sketch071
  FullyConstrained = true
  MapMode = 5
  Placement = pos=(-112.262,-81.5574,410) rot=(0,0,1;3.66519rad)
  Support = -> [DatumPlane009]
  expr: Constraints[12] = <<cover_holders_corners_back>>.length
  sketch-geometry (6):
    g0: ArcOfCircle CenterX=-58.82 CenterY=20 CenterZ=0 NormalX=0 NormalY=0 NormalZ=1 AngleXU=0 Radius=5 StartAngle=1.57079 EndAngle=3.14159
    g1: ArcOfCircle CenterX=58.82 CenterY=20 CenterZ=0 NormalX=0 NormalY=0 NormalZ=1 AngleXU=0 Radius=5 StartAngle=7.13613e-08 EndAngle=1.57079
    g2: LineSegment StartX=-58.82 StartY=25 StartZ=0 EndX=-63.82 EndY=25 EndZ=0
    g3: LineSegment StartX=-63.82 StartY=25 StartZ=0 EndX=-63.82 EndY=20 EndZ=0
    g4: LineSegment StartX=63.82 StartY=20 StartZ=0 EndX=63.82 EndY=25 EndZ=0
    g5: LineSegment StartX=58.82 StartY=25 StartZ=0 EndX=63.82 EndY=25 EndZ=0
  constraints (18):
    c: Coincident(g2,g0)
    c: Horizontal(g2)
    c: Tangent(g2,g0)
    c: Coincident(g3,g2)
    c: Vertical(g3)
    c: Coincident(g4,g1)
    c: Vertical(g4)
    c: Tangent(g4,g1)
    c: Coincident(g5,g1)
    c: Horizontal(g5)
    c: Tangent(g5,g1)
    c: Coincident(g4,g5)
    c: DistanceY(g4) = 25
    c: Tangent(g3,g0) = -1.5708
    c: Equal(g1,g0)
    c: Diameter(g1) = 10
    c: DistanceX(g4) = 63.82
    c: Symmetric(g2,g4,g-2)
FEATURE [PartDesign::Pocket] Pocket043
  BaseFeature = -> MultiTransform007
  Direction = (0,0,-1)
  Length = 5
  Length2 = 5
  Midplane = true
  Profile = -> Sketch071
  ReferenceAxis = -> Sketch071 [N_Axis]
  Type = 1
FEATURE [PartDesign::Pocket] Pocket020
  BaseFeature = -> Pocket043
  Direction = (-1,2e-16,-3e-16)
  Length = 34
  Length2 = 5
  Midplane = true
  Profile = -> Sketch046
  ReferenceAxis = -> Sketch046 [N_Axis]
  Type = 0
  expr: Length = <<main>>.end_face_width + 5 mm
FEATURE [PartDesign::PolarPattern] PolarPattern004
  Angle = 360
  Axis = -> Z_Axis
  BaseFeature = -> Pocket020
  Occurrences = 3
  Originals = -> [Pocket020]
FEATURE [PartDesign::Pocket] Pocket019
  BaseFeature = -> PolarPattern004
  Direction = (-1,2e-16,-3e-16)
  Length = 29
  Length2 = 5
  Midplane = true
  Profile = -> Sketch043
  ReferenceAxis = -> Sketch043 [N_Axis]
  Refine = true
  Type = 0
  expr: Length = <<main>>.end_face_width
FEATURE [PartDesign::Pocket] Pocket041
  BaseFeature = -> Pocket019
  Direction = (0.5,0.866025,-1e-16)
  Length = 34
  Length2 = 5
  Midplane = true
  Profile = -> Sketch069
  ReferenceAxis = -> Sketch069 [N_Axis]
  Type = 0
  expr: Length = <<main>>.end_face_width + 5 mm
FEATURE [PartDesign::Mirrored] Mirrored014
  BaseFeature = -> Pocket041
  MirrorPlane = -> YZ_Plane
  Originals = -> [Pocket041,Pocket043]
FEATURE [PartDesign::Pocket] Pocket003
  BaseFeature = -> Mirrored014
  Direction = (-1,0,0)
  Length = 5
  Length2 = 5
  Profile = -> Sketch004
  ReferenceAxis = -> Sketch004 [N_Axis]
  Type = 1
FEATURE [PartDesign::Pocket] Pocket004
  BaseFeature = -> Pocket003
  Direction = (-1,0,0)
  Length = 5
  Length2 = 5
  Profile = -> Binder
  Reversed = true
  Type = 1
FEATURE [PartDesign::Pocket] Pocket006
  BaseFeature = -> Pocket004
  Direction = (-1,0,0)
  Length = 5
  Length2 = 5
  Midplane = true
  Profile = -> Sketch008
  ReferenceAxis = -> Sketch008 [N_Axis]
  Type = 1
FEATURE [PartDesign::Pocket] Pocket007
  BaseFeature = -> Pocket006
  Direction = (-1,0,0)
  Length = 5
  Length2 = 5
  Profile = -> Sketch007
  ReferenceAxis = -> Sketch007 [N_Axis]
  Type = 1
FEATURE [PartDesign::Pocket] Pocket008
  BaseFeature = -> Pocket007
  Direction = (-1,0,0)
  Length = 5
  Length2 = 5
  Profile = -> Binder001
  Reversed = true
  Type = 1
FEATURE [PartDesign::MultiTransform] MultiTransform001
  BaseFeature = -> Pocket008
  Originals = -> [Pocket003,Pocket004,Pocket006,Pocket007,Pocket008]
  Transformations = -> [Mirrored,Mirrored001,PolarPattern002]
FEATURE [PartDesign::Pocket] Pocket002
  BaseFeature = -> MultiTransform001
  Direction = (-1,0,0)
  Length = 5
  Length2 = 5
  Midplane = true
  Profile = -> Sketch003
  ReferenceAxis = -> Sketch003 [N_Axis]
  Type = 1
FEATURE [PartDesign::MultiTransform] MultiTransform
  BaseFeature = -> Pocket002
  Originals = -> [Pocket002]
  Refine = true
  Transformations = -> [LinearPattern,LinearPattern001,LinearPattern002,PolarPattern001]
FEATURE [PartDesign::Pocket] Pocket028
  BaseFeature = -> MultiTransform
  Direction = (-1,2e-16,-3e-16)
  Length = 5
  Length2 = 5
  Midplane = true
  Profile = -> Sketch055
  ReferenceAxis = -> Sketch055 [N_Axis]
  Type = 1
FEATURE [PartDesign::Pocket] Pocket005
  BaseFeature = -> Pocket028
  Direction = (-1,0,0)
  Length = 5
  Length2 = 5
  Midplane = true
  Profile = -> Sketch005
  ReferenceAxis = -> Sketch005 [N_Axis]
  Type = 1
FEATURE [PartDesign::SubShapeBinder] Binder011
  BindCopyOnChange = 0
  BindMode = 0
  ClaimChildren = false
  Context = -> Body [Binder011.]
  Fuse = false
  MakeFace = true
  OffsetFill = false
  OffsetIntersection = false
  OffsetJoinType = 0
  OffsetOpenResult = false
  PartialLoad = false
  Placement = pos=(0,181.372,504) rot=(0.57735,0.57735,0.57735;2.0944rad)
  Relative = false
  Support = -> [Body003[Pocket013.Sketch039.]]
  _Version = 2
  expr: Placement = Local_CS011.Placement
FEATURE [PartDesign::Pocket] Pocket044
  BaseFeature = -> Pocket005
  Direction = (-1,4e-16,-3e-16)
  Length = 5
  Length2 = 5
  Midplane = true
  Profile = -> Binder011
  Type = 1
FEATURE [PartDesign::PolarPattern] PolarPattern006
  Angle = 360
  Axis = -> Z_Axis
  BaseFeature = -> Pocket044
  Occurrences = 3
  Originals = -> [Pocket028,Pocket005,Pocket044]
FEATURE [PartDesign::Body] Body  label="Body_material_0.30ansi"
  Group = -> [Sketch,BaseBend,Sketch002,Pocket001,PolarPattern,DatumPoint,Local_CS,Local_CS001,DatumPlane,Sketch003,Sketch004,Local_CS002,Local_CS003,DatumPlane001,DatumPlane002,DatumPlane003,Binder,Sketch043,DatumLine002,Sketch046,Bend002,Bend003,DatumPlane007,Sketch047,Pocket021,DatumPlane008,Sketch048,Sketch064,Sketch049,DatumPlane011,Sketch070,Pocket,Pocket042,Pocket039,Pocket027,MultiTransform005,+50 more]
  Origin = -> Origin
  Tip = -> Pocket044
FEATURE [PartDesign::CoordinateSystem] LCS_0003
  AttacherType = Attacher::AttachEngine3D
  MapMode = 2
  Support = -> [X_Axis015]
FEATURE [Sketcher::SketchObject] Sketch072
  FullyConstrained = true
  MapMode = 5
  Placement = pos=(0,0,0) rot=(1,0,0;1.5708rad)
  Support = -> [XZ_Plane015]
  expr: Constraints[12] = 75 mm + 7 mm
  sketch-geometry (5):
    g0: LineSegment StartX=-41 StartY=-36.5 StartZ=0 EndX=-41 EndY=0 EndZ=0
    g1: LineSegment StartX=-41 StartY=0 StartZ=0 EndX=41 EndY=0 EndZ=0
    g2: LineSegment StartX=41 StartY=0 StartZ=0 EndX=41 EndY=-36.5 EndZ=0
    g3: LineSegment StartX=41 StartY=-36.5 StartZ=0 EndX=-41 EndY=-36.5 EndZ=0
    g4: GeomPoint X=0 Y=-18.25 Z=0
  constraints (13):
    c: Coincident(g0,g1)
    c: Coincident(g1,g2)
    c: Coincident(g2,g3)
    c: Coincident(g3,g0)
    c: Horizontal(g1)
    c: Horizontal(g3)
    c: Vertical(g0)
    c: Vertical(g2)
    c: Symmetric(g1,g0,g4)
    c: PointOnObject(g4,g-2)
    c: PointOnObject(g1,g-1)
    c: DistanceY(g2) = -36.5
    c: DistanceX(g0,g1) = 82
FEATURE [PartDesign::FeaturePython] BaseBend005  # WARN: FeaturePython — macro-defined, semantics opaque (R4)
  BendSide = 0
  BendSketch = -> Sketch072
  MidPlane = true
  Reverse = false
  length = 258.4
  radius = 0.1
  thickness = 0.3
  expr: length = <<top>>.cover_length + <<module>>.module_width + <<main>>.module_distance_x
  expr: radius = <<main>>.bend_r
  expr: thickness = <<main>>.al_thickness
FEATURE [PartDesign::SubShapeBinder] Binder012
  BindCopyOnChange = 0
  BindMode = 0
  ClaimChildren = false
  Context = -> top [Binder012.]
  Fuse = false
  MakeFace = true
  OffsetFill = false
  OffsetIntersection = false
  OffsetJoinType = 0
  OffsetOpenResult = false
  PartialLoad = false
  Placement = pos=(1.7e-14,75,-1.7e-14) rot=(0.57735,0.57735,0.57735;2.0944rad)
  Relative = false
  Support = -> [<external composit_stand2_reserve.FCStd>#Body_2[Pocket050.Sketch091.]]
  _Version = 2
  expr: .Placement.Base.y = <<main>>.module_distance_x / 2 + 108.4 mm / 2
  expr: Placement = Sketch073.Placement
FEATURE [PartDesign::Pocket] Pocket045
  BaseFeature = -> BaseBend005
  Direction = (-1,2e-16,-2e-16)
  Length = 5
  Length2 = 5
  Midplane = true
  Profile = -> Binder012
  Type = 1
FEATURE [PartDesign::Plane] DatumPlane012
  Length = 113.256
  MapMode = 4
  Placement = pos=(1.7e-14,75,-1.7e-14) rot=(0.57735,0.57735,0.57735;4.18879rad)
  ResizeMode = 0
  Support = -> [Binder012]
  Width = 116.686
FEATURE [Sketcher::SketchObject] Sketch073
  AttachmentOffset = pos=(75,0,0) rot=(0,0,1;0rad)
  FullyConstrained = false
  MapMode = 5
  Placement = pos=(1.67e-14,75,-1.67e-14) rot=(0.57735,0.57735,0.57735;2.0944rad)
  Support = -> [YZ_Plane015]
  expr: .AttachmentOffset.Base.x = <<main>>.module_distance_x / 2 + <<module>>.module_width / 2
  sketch-geometry (8):
    g0: LineSegment StartX=-13.2362 StartY=-16.9439 StartZ=0 EndX=-13.2362 EndY=16.9439 EndZ=0
    g1: LineSegment StartX=-13.2362 StartY=16.9439 StartZ=0 EndX=8.35131 EndY=16.9439 EndZ=0
    g2: LineSegment StartX=13.2362 StartY=12.059 StartZ=0 EndX=13.2362 EndY=-16.9439 EndZ=0
    g3: LineSegment StartX=13.2362 StartY=-16.9439 StartZ=0 EndX=-13.2362 EndY=-16.9439 EndZ=0
    g4: GeomPoint X=0 Y=0 Z=0
    g5: LineSegment StartX=-13.2362 StartY=-16.9439 StartZ=0 EndX=13.2362 EndY=16.9439 EndZ=0
    g6: ArcOfCircle CenterX=8.35131 CenterY=12.059 CenterZ=0 NormalX=0 NormalY=0 NormalZ=1 AngleXU=0 Radius=4.88484 StartAngle=2e-16 EndAngle=1.5708
    g7: GeomPoint X=13.2362 Y=16.9439 Z=0
  constraints (15):
    c: Coincident(g0,g1)
    c: Coincident(g2,g3)
    c: Coincident(g3,g0)
    c: Horizontal(g1)
    c: Horizontal(g3)
    c: Vertical(g0)
    c: Vertical(g2)
    c: Symmetric(g7,g0,g4)
    c: Coincident(g4,g-1)
    c: Coincident(g5,g0)
    c: Coincident(g5,g7)
    c: PointOnObject(g7,g1)
    c: PointOnObject(g7,g2)
    c: Tangent(g1,g6) = 1.5708
    c: Tangent(g2,g6) = 1.5708
FEATURE [PartDesign::CoordinateSystem] LCS_0004
  AttacherType = Attacher::AttachEngine3D
  MapMode = 2
  Support = -> [X_Axis018]
FEATURE [Sketcher::SketchObject] Sketch_2
  FullyConstrained = true
  MapMode = 5
  Placement = pos=(0,4e-16,-29.2041) rot=(0.590324,0.550486,0.590324;2.13516rad)
  Support = -> [DatumPlane006]
FEATURE [Sketcher::SketchObject] Sketch076
  FullyConstrained = true
  MapMode = 5
  Placement = pos=(0,4e-16,-29.2041) rot=(0.590324,0.550486,0.590324;2.13516rad)
  Support = -> [DatumPlane006]
  expr: Constraints[11] = <<module>>.module_hole_x + <<main>>.module_distance_x + <<module>>.module_width - <<module>>.module_fixture_distance_x + 2 mm
  expr: Constraints[21] = Sketch037.Constraints.cut_height
  sketch-geometry (11):
    g0: LineSegment StartX=-16.5 StartY=23 StartZ=0 EndX=-16.5 EndY=4.27416 EndZ=0
    g1: LineSegment StartX=-16.5 StartY=0 StartZ=0 EndX=16.5 EndY=0 EndZ=0
    g2: LineSegment StartX=16.5 StartY=0 StartZ=0 EndX=16.5 EndY=2.77416 EndZ=0
    g3: LineSegment StartX=16.5 StartY=23 StartZ=0 EndX=-16.5 EndY=23 EndZ=0
    g4: GeomPoint X=0 Y=11.5 Z=0
    g5: LineSegment StartX=-18 StartY=2.77416 StartZ=0 EndX=-16.5 EndY=2.77416 EndZ=0
    g6: LineSegment StartX=18 StartY=2.77416 StartZ=0 EndX=16.5 EndY=2.77416 EndZ=0
    g7: LineSegment StartX=16.5 StartY=4.27416 StartZ=0 EndX=16.5 EndY=23 EndZ=0
    g8: LineSegment StartX=-16.5 StartY=2.77416 StartZ=0 EndX=-16.5 EndY=0 EndZ=0
    g9: ArcOfCircle CenterX=18 CenterY=4.27416 CenterZ=0 NormalX=0 NormalY=0 NormalZ=1 AngleXU=0 Radius=1.5 StartAngle=3.14159 EndAngle=4.71239
    g10: ArcOfCircle CenterX=-18 CenterY=4.27416 CenterZ=0 NormalX=0 NormalY=0 NormalZ=1 AngleXU=0 Radius=1.5 StartAngle=4.71239 EndAngle=6.28319
  constraints (29):
    c: Coincident(g8,g1)
    c: Coincident(g1,g2)
    c: Coincident(g7,g3)
    c: Coincident(g3,g0)
    c: Horizontal(g1)
    c: Horizontal(g3)
    c: Vertical(g0)
    c: Vertical(g2)
    c: Symmetric(g1,g0,g4)
    c: PointOnObject(g4,g-2)
    c: PointOnObject(g1,g-1)
    c: DistanceX(g8,g1) = 33
    c: DistanceY(g7) = 23
    c: Horizontal(g5)
    c: Horizontal(g6)
    c: Coincident(g2,g6)
    c: Coincident(g8,g5)
    c: Horizontal(g5,g2)
    c: Vertical(g7)
    c: Vertical(g8)
    c: Vertical(g5,g0)
    c: DistanceY(g2) = 2.77416
    c: Tangent(g9,g6) = 1.5708
    c: Tangent(g9,g7) = 1.5708
    c: Vertical(g2,g7)
    c: Diameter(g9) = 3
    c: Tangent(g10,g5) = -1.5708
    c: Tangent(g10,g0) = 1.5708
    c: Equal(g10,g9)
FEATURE [PartDesign::SubShapeBinder] Binder013
  BindCopyOnChange = 0
  BindMode = 0
  ClaimChildren = false
  Context = -> Body001 [Binder013.]
  Fuse = false
  MakeFace = true
  OffsetFill = false
  OffsetIntersection = false
  OffsetJoinType = 0
  OffsetOpenResult = false
  PartialLoad = false
  Placement = pos=(-1e-15,-0.767321,-18.2309) rot=(0.590324,0.550486,0.590324;2.13516rad)
  Relative = false
  Support = -> [Body[Pocket005.Sketch005.]]
  _Version = 2
  expr: Placement = Sketch038.Placement
FEATURE [PartDesign::CoordinateSystem] Local_CS008
  AttacherType = Attacher::AttachEngine3D
  AttachmentOffset = pos=(0,0,0) rot=(0.57735,-0.57735,0.57735;2.0944rad)
  MapMode = 2
  Placement = pos=(-1e-15,-0.767321,-18.2309) rot=(1,0,0;3.21141rad)
  Support = -> [Binder013]
FEATURE [Sketcher::SketchObject] Sketch038
  AttachmentOffset = pos=(0,11,0) rot=(0,0,1;0rad)
  FullyConstrained = true
  MapMode = 5
  Placement = pos=(-6e-16,-0.767321,-18.2309) rot=(0.590324,0.550486,0.590324;2.13516rad)
  Support = -> [DatumPlane006]
  expr: .AttachmentOffset.Base.y = <<main>>.distance_gutter_holes_dropper_cutout + 2 mm
FEATURE [Sketcher::SketchObject] Sketch077
  AttachmentOffset = pos=(35,0,0) rot=(0,0,1;0rad)
  FullyConstrained = true
  MapMode = 5
  Placement = pos=(-5.8e-15,109.732,-21.5309) rot=(0.590324,0.550486,0.590324;2.13516rad)
  Support = -> [DatumPlane004]
  expr: .AttachmentOffset.Base.x = <<dropper>>.distance_between_droppers2 / 2
FEATURE [PartDesign::SubShapeBinder] Binder014
  BindCopyOnChange = 0
  BindMode = 0
  ClaimChildren = false
  Context = -> Body001 [Binder014.]
  Fuse = false
  MakeFace = true
  OffsetFill = false
  OffsetIntersection = false
  OffsetJoinType = 0
  OffsetOpenResult = false
  PartialLoad = false
  Placement = pos=(-2e-15,109.732,-21.5309) rot=(0.590324,0.550486,0.590324;2.13516rad)
  Relative = false
  Support = -> [Pocket010[Sketch037.]]
  _Version = 2
  expr: Placement = Sketch077.Placement
FEATURE [PartDesign::Plane] DatumPlane005
  Length = 94.9977
  MapMode = 4
  Placement = pos=(-2e-15,109.732,-21.5309) rot=(-0.563438,-0.563438,-0.604214;2.05457rad)
  ResizeMode = 0
  Support = -> [Binder014]
  Width = 62.8201
FEATURE [PartDesign::Pocket] Pocket011
  BaseFeature = -> Pocket010
  Direction = (-1,0,0)
  Length = 5
  Length2 = 5
  Profile = -> Binder014
  Reversed = true
  Type = 1
FEATURE [PartDesign::MultiTransform] MultiTransform003
  BaseFeature = -> Pocket011
  Originals = -> [Pocket010]
  Transformations = -> [Mirrored002,LinearPattern004,LinearPattern005]
FEATURE [PartDesign::Mirrored] Mirrored003
  MirrorPlane = -> DatumPlane005
FEATURE [PartDesign::MultiTransform] MultiTransform004
  BaseFeature = -> MultiTransform003
  Originals = -> [Pocket011]
  Transformations = -> [Mirrored003,LinearPattern006,LinearPattern007]
FEATURE [PartDesign::Pocket] Pocket012
  BaseFeature = -> MultiTransform004
  Direction = (-1,-4e-16,-1e-16)
  Length = 5
  Length2 = 5
  Midplane = true
  Profile = -> Binder013
  Type = 1
FEATURE [PartDesign::Pocket] Pocket046
  BaseFeature = -> Pocket012
  Direction = (-1,-2e-16,-1e-16)
  Length = 5
  Length2 = 5
  Midplane = true
  Profile = -> Sketch076
  ReferenceAxis = -> Sketch076 [N_Axis]
  Type = 1
FEATURE [Sketcher::SketchObject] Sketch078
  AttachmentOffset = pos=(0,-38.4082,0) rot=(0,0,1;0rad)
  FullyConstrained = true
  MapMode = 5
  Placement = pos=(8.5e-15,-8.5e-15,-38.4082) rot=(0.57735,0.57735,0.57735;2.0944rad)
  Support = -> [YZ_Plane003]
  expr: AttachmentOffset = Sketch010.AttachmentOffset
  expr: Constraints[12] = Sketch010.Constraints[12]
  expr: Constraints[16] = Sketch010.Constraints[16]
  expr: Constraints[37] = Sketch037.Constraints.cut_height
  expr: Constraints[6] = Sketch010.Constraints[6]
  sketch-geometry (15):
    g0: LineSegment StartX=-128.951 StartY=0.187012 StartZ=0 EndX=129.299 EndY=18.2456 EndZ=0
    g1: ArcOfCircle CenterX=-129.125 CenterY=2.68092 CenterZ=0 NormalX=0 NormalY=0 NormalZ=1 AngleXU=0 Radius=2.5 StartAngle=3.14159 EndAngle=4.7822
    g2: LineSegment StartX=131.625 StartY=20.7395 StartZ=0 EndX=131.625 EndY=0 EndZ=0
    g3: LineSegment StartX=-131.625 StartY=0 StartZ=0 EndX=-131.625 EndY=2.68092 EndZ=0
    g4: LineSegment StartX=131.625 StartY=0 StartZ=0 EndX=0 EndY=0 EndZ=0
    g5: LineSegment StartX=0 StartY=0 StartZ=0 EndX=-131.625 EndY=0 EndZ=0
    g6: GeomPoint X=-131.625 Y=0 Z=0
    g7: GeomPoint X=131.625 Y=20.7395 Z=0
    g8: ArcOfCircle CenterX=129.125 CenterY=20.7395 CenterZ=0 NormalX=0 NormalY=0 NormalZ=1 AngleXU=0 Radius=2.5 StartAngle=4.7822 EndAngle=6.28319
    g9: GeomPoint X=131.625 Y=18.4082 Z=0
    g10: LineSegment StartX=131.625 StartY=20.7395 StartZ=0 EndX=131.625 EndY=23.9867 EndZ=0
    g11: ArcOfCircle CenterX=128.625 CenterY=23.9867 CenterZ=0 NormalX=0 NormalY=0 NormalZ=1 AngleXU=0 Radius=3 StartAngle=4.7822 EndAngle=6.28319
    g12: ArcOfCircle CenterX=-128.625 CenterY=5.99804 CenterZ=0 NormalX=0 NormalY=0 NormalZ=1 AngleXU=0 Radius=3 StartAngle=3.1416 EndAngle=4.7822
    g13: LineSegment StartX=-131.625 StartY=2.68092 StartZ=0 EndX=-131.625 EndY=5.99802 EndZ=0
    g14: LineSegment StartX=-128.416 StartY=3.00535 StartZ=0 EndX=128.834 EndY=20.994 EndZ=0
  constraints (38):
    c: Vertical(g2)
    c: Coincident(g4,g2)
    c: Coincident(g3,g5)
    c: Vertical(g3)
    c: Tangent(g3,g1) = 1.5708
    c: Tangent(g1,g0) = -1.5708
    c: DistanceX(g5,g2) = 263.25
    c: Coincident(g4,g5)
    c: Horizontal(g4)
    c: Horizontal(g5)
    c: Equal(g5,g4)
    c: PointOnObject(g4,g-2)
    c: Angle(g-1,g0) = 0.0698132
    c: PointOnObject(g6,g3)
    c: PointOnObject(g6,g0)
    c: PointOnObject(g6,g-1)
    c: Diameter(g1) = 5
    c: PointOnObject(g4,g-1)
    c: Coincident(g8,g7)
    c: Tangent(g2,g8) = 1.5708
    c: Equal(g8,g1)
    c: Tangent(g8,g0) = -1.5708
    c: PointOnObject(g9,g2)
    c: PointOnObject(g9,g0)
    c: DistanceY(g9) = 18.4082
    c: Coincident(g10,g2)
    c: Vertical(g10)
    c: Coincident(g13,g1)
    c: Coincident(g13,g12)
    c: Vertical(g13)
    c: Tangent(g13,g12)
    c: Tangent(g11,g10) = -1.5708
    c: Tangent(g14,g11) = -1.5708
    c: Tangent(g14,g12) = -1.5708
    c: Equal(g12,g11)
    c: Diameter(g12) = 6
    c: Parallel(g14,g0)
    c: Distance(g0,g14) = 2.77416
FEATURE [PartDesign::Pocket] Pocket047
  BaseFeature = -> Pocket046
  Direction = (-1,2e-16,-3e-16)
  Length = 5
  Length2 = 5
  Midplane = true
  Profile = -> Sketch078
  ReferenceAxis = -> Sketch078 [N_Axis]
  Type = 1
FEATURE [Sketcher::SketchObject] Sketch079
  FullyConstrained = true
  MapMode = 5
  Support = -> [XY_Plane018]
  expr: Constraints[1] = Sketch.Constraints.max_r * 2 + 5 mm
  sketch-geometry (1):
    g0: Circle CenterX=0 CenterY=0 CenterZ=0 NormalX=0 NormalY=0 NormalZ=1 AngleXU=0 Radius=354.67
  constraints (2):
    c: Coincident(g0,g-1)
    c: Diameter(g0) = 709.34
FEATURE [PartDesign::Pad] Pad011
  Direction = (0,0,1)
  Length = 0.3
  Length2 = 10
  Profile = -> Sketch079
  ReferenceAxis = -> Sketch079 [N_Axis]
  Type = 0
  expr: Length = <<main>>.al_thickness
FEATURE [PartDesign::SubShapeBinder] Binder015
  BindCopyOnChange = 0
  BindMode = 0
  ClaimChildren = false
  Context = -> basement_composite [Binder015.]
  Fuse = false
  MakeFace = true
  OffsetFill = false
  OffsetIntersection = false
  OffsetJoinType = 0
  OffsetOpenResult = false
  PartialLoad = false
  Placement = pos=(0,0,0) rot=(0,0,-1;1.0472rad)
  Relative = true
  Support = -> [Body003007[Pocket029.Sketch058.]]
  _Version = 2
FEATURE [PartDesign::Pocket] Pocket048
  BaseFeature = -> Pad011
  Direction = (0,0,-1)
  Length = 5
  Length2 = 5
  Midplane = true
  Profile = -> Binder015
  Type = 1
FEATURE [PartDesign::SubShapeBinder] Binder016
  BindCopyOnChange = 0
  BindMode = 0
  ClaimChildren = false
  Context = -> basement_composite [Binder016.]
  Fuse = false
  MakeFace = true
  OffsetFill = false
  OffsetIntersection = false
  OffsetJoinType = 0
  OffsetOpenResult = false
  PartialLoad = false
  Relative = true
  Support = -> [Body003008[Pocket031.Sketch060.]]
  _Version = 2
FEATURE [PartDesign::Hole] Hole
  BaseFeature = -> Pocket048
  CustomThreadClearance = 0
  Depth = 2026.53
  DepthType = 1
  Diameter = 3.4
  DrillForDepth = false
  DrillPoint = 1
  DrillPointAngle = 118
  HoleCutCountersinkAngle = 90
  HoleCutCustomValues = false
  HoleCutDepth = 0
  HoleCutDiameter = 6.1
  HoleCutType = 0
  Midplane = true
  ModelThread = false
  Profile = -> Binder016
  Tapered = false
  TaperedAngle = 90
  ThreadClass = 0
  ThreadDepth = 2026.53
  ThreadDepthType = 0
  ThreadDirection = 0
  ThreadFit = 0
  ThreadSize = 0
  ThreadType = 0
  Threaded = false
  UseCustomThreadClearance = false
  expr: Diameter = <<main>>.rivet_d
FEATURE [PartDesign::Mirrored] Mirrored017
  MirrorPlane = -> YZ_Plane018
FEATURE [PartDesign::PolarPattern] PolarPattern011
  Angle = 360
  Axis = -> Z_Axis018
  Occurrences = 3
FEATURE [PartDesign::MultiTransform] MultiTransform009
  BaseFeature = -> Hole
  Originals = -> [Hole]
  Transformations = -> [Mirrored017,PolarPattern011]
FEATURE [PartDesign::PolarPattern] PolarPattern012
  Angle = 120
  Axis = -> Z_Axis018
  BaseFeature = -> MultiTransform009
  Occurrences = 2
  Originals = -> [Pocket048]
FEATURE [Sketcher::SketchObject] Sketch080
  FullyConstrained = true
  MapMode = 5
  Support = -> [XY_Plane015]
  expr: Constraints[10] = <<main>>.end_face_width / 2
  expr: Constraints[11] = <<main>>.work_plane_width
  expr: Constraints[18] = Local_CS.Placement.Base.y
  sketch-geometry (7):
    g0: LineSegment StartX=0 StartY=-170.5 StartZ=0 EndX=13 EndY=-170.5 EndZ=0
    g1: LineSegment StartX=14.5 StartY=173 StartZ=0 EndX=0 EndY=181.372 EndZ=0
    g2: LineSegment StartX=0 StartY=181.372 StartZ=0 EndX=0 EndY=-170.5 EndZ=0
    g3: LineSegment StartX=14.5 StartY=-169 StartZ=0 EndX=14.5 EndY=0 EndZ=0
    g4: LineSegment StartX=14.5 StartY=0 StartZ=0 EndX=14.5 EndY=173 EndZ=0
    g5: ArcOfCircle CenterX=13 CenterY=-169 CenterZ=0 NormalX=0 NormalY=0 NormalZ=1 AngleXU=0 Radius=1.5 StartAngle=4.71239 EndAngle=6.28319
    g6: GeomPoint X=14.5 Y=-170.5 Z=0
  constraints (19):
    c: Coincident(g4,g1)
    c: Coincident(g1,g2)
    c: Coincident(g2,g0)
    c: Horizontal(g0)
    c: Vertical(g2)
    c: PointOnObject(g0,g-2)
    c: Coincident(g3,g4)
    c: Vertical(g3)
    c: Vertical(g4)
    c: PointOnObject(g3,g-1)
    c: DistanceX(g1) = 14.5
    c: DistanceY(g6,g1) = 343.5
    c: Angle(g-2,g1) = 1.0472
    c: PointOnObject(g6,g0)
    c: PointOnObject(g6,g3)
    c: Tangent(g0,g5) = -1.5708
    c: Tangent(g3,g5) = -1.5708
    c: Diameter(g5) = 3
    c: DistanceY(g1) = 181.372
FEATURE [PartDesign::Mirrored] Mirrored019
  MirrorPlane = -> DatumPlane012
FEATURE [PartDesign::Mirrored] Mirrored020
  MirrorPlane = -> XZ_Plane015
FEATURE [PartDesign::MultiTransform] MultiTransform008
  BaseFeature = -> Pocket045
  Originals = -> [Pocket045]
  Transformations = -> [Mirrored019,Mirrored020]
FEATURE [PartDesign::Pad] Pad012
  BaseFeature = -> MultiTransform008
  Direction = (0,0,1)
  Length = 0.3
  Length2 = 10
  Profile = -> Sketch080
  ReferenceAxis = -> Sketch080 [N_Axis]
  Reversed = true
  Type = 0
  expr: Length = <<main>>.al_thickness
FEATURE [Spreadsheet::Sheet] Spreadsheet004  label="top"
  cells = B2(cover_width)=; B3(cover_length)==108.4 mm
FEATURE [App::DocumentObjectGroup] Tables
  Group = -> [Spreadsheet,Spreadsheet002,Spreadsheet003,Spreadsheet001,Spreadsheet004]
FEATURE [Sketcher::SketchObject] Sketch081
  FullyConstrained = false
  MapMode = 5
  Support = -> [XY_Plane015]
  expr: Constraints[11] = <<main>>.end_face_width / 2
  expr: Constraints[9] = BaseBend005.length / 2 - <<top>>.cover_length
  sketch-geometry (5):
    g0: LineSegment StartX=56.5269 StartY=20.8 StartZ=0 EndX=56.5269 EndY=-20.8 EndZ=0
    g1: LineSegment StartX=56.5269 StartY=-20.8 StartZ=0 EndX=14.5 EndY=-20.8 EndZ=0
    g2: LineSegment StartX=14.5 StartY=-20.8 StartZ=0 EndX=14.5 EndY=20.8 EndZ=0
    g3: LineSegment StartX=14.5 StartY=20.8 StartZ=0 EndX=56.5269 EndY=20.8 EndZ=0
    g4: GeomPoint X=35.5134 Y=0 Z=0
  constraints (12):
    c: Coincident(g0,g1)
    c: Coincident(g1,g2)
    c: Coincident(g2,g3)
    c: Coincident(g3,g0)
    c: Horizontal(g1)
    c: Horizontal(g3)
    c: Vertical(g0)
    c: Symmetric(g1,g0,g4)
    c: PointOnObject(g4,g-1)
    c: DistanceY(g2) = 20.8
    c: Vertical(g2)
    c: DistanceX(g2) = 14.5
FEATURE [PartDesign::SubShapeBinder] Binder017
  BindCopyOnChange = 0
  BindMode = 0
  ClaimChildren = false
  Context = -> top [Binder017.]
  Fuse = false
  MakeFace = true
  OffsetFill = false
  OffsetIntersection = false
  OffsetJoinType = 0
  OffsetOpenResult = false
  PartialLoad = false
  Placement = pos=(1.7e-14,75,-1.7e-14) rot=(0.57735,0.57735,0.57735;2.0944rad)
  Relative = false
  Support = -> [<external composit_stand2_reserve.FCStd>#Body_2[Pocket051.Sketch092.]]
  _Version = 2
  expr: Placement = Sketch073.Placement
FEATURE [PartDesign::Pocket] Pocket050
  BaseFeature = -> Pad012
  Direction = (-1,2e-16,-2e-16)
  Length = 5
  Length2 = 5
  Midplane = true
  Profile = -> Binder017
  Type = 1
FEATURE [PartDesign::Mirrored] Mirrored021
  BaseFeature = -> Pocket050
  MirrorPlane = -> XZ_Plane015
  Originals = -> [Pocket050]
FEATURE [PartDesign::CoordinateSystem] LCS_0005
  AttacherType = Attacher::AttachEngine3D
  MapMode = 2
  Support = -> [X_Axis020]
FEATURE [Sketcher::SketchObject] Sketch082
  FullyConstrained = false
  MapMode = 5
  Placement = pos=(0,0,0) rot=(0.57735,0.57735,0.57735;2.0944rad)
  Support = -> [YZ_Plane020]
  sketch-geometry (4):
    g0: LineSegment StartX=-22 StartY=0 StartZ=0 EndX=0 EndY=0 EndZ=0
    g1: LineSegment StartX=0 StartY=0 StartZ=0 EndX=0 EndY=22 EndZ=0
    g2: GeomPoint X=-3 Y=3 Z=0
    g3: GeomPoint X=-2.52181 Y=16 Z=0
  constraints (9):
    c: PointOnObject(g0,g-1)
    c: Coincident(g0,g-1)
    c: Coincident(g1,g0)
    c: PointOnObject(g1,g-2)
    c: Equal(g0,g1)
    c: DistanceX(g2) = -3
    c: DistanceY(g2) = 3
    c: DistanceY(g2,g3) = 13
    c: DistanceY(g3,g1) = 6
FEATURE [PartDesign::FeaturePython] BaseBend006  # WARN: FeaturePython — macro-defined, semantics opaque (R4)
  BendSide = 0
  BendSketch = -> Sketch082
  MidPlane = true
  Reverse = false
  length = 350
  radius = 0.1
  thickness = 0.3
FEATURE [PartDesign::CoordinateSystem] Local_CS014
  AttacherType = Attacher::AttachEngine3D
  AttachmentOffset = pos=(0,-3,3) rot=(0,0,1;0rad)
  MapMode = 5
  Placement = pos=(0,-3,3) rot=(0,0,1;0rad)
  Support = -> [XY_Plane020]
FEATURE [PartDesign::Plane] DatumPlane013
  Length = 376.458
  MapMode = 3
  Placement = pos=(0,-3,3) rot=(1,0,0;1.5708rad)
  ResizeMode = 0
  Support = -> [Local_CS014]
  Width = 76.4575
FEATURE [Sketcher::SketchObject] Sketch083
  AttachmentOffset = pos=(0,13,0) rot=(0,0,1;0rad)
  FullyConstrained = false
  MapMode = 5
  Placement = pos=(0,-3,16) rot=(1,0,0;1.5708rad)
  Support = -> [DatumPlane013]
  expr: Constraints[3] = <<main>>.rivet_d
  sketch-geometry (3):
    g0: Circle CenterX=0 CenterY=0 CenterZ=0 NormalX=0 NormalY=0 NormalZ=1 AngleXU=0 Radius=1.7
    g1: Circle CenterX=135 CenterY=0 CenterZ=0 NormalX=0 NormalY=0 NormalZ=1 AngleXU=0 Radius=1.7
    g2: Circle CenterX=-135 CenterY=0 CenterZ=0 NormalX=0 NormalY=0 NormalZ=1 AngleXU=0 Radius=1.7
  constraints (6):
    c: Symmetric(g1,g2,g-2)
    c: Horizontal(g0,g1)
    c: Equal(g0,g1)
    c: Diameter(g0) = 3.4
    c: Coincident(g0,g-1)
    c: DistanceX(g2,g1) = 270
FEATURE [PartDesign::Fillet] Fillet
  Base = -> BaseBend006 [Edge8,Edge25]
  BaseFeature = -> BaseBend006
  Radius = 10
  SupportTransform = false
  UseAllEdges = false
FEATURE [PartDesign::Mirrored] Mirrored022
  BaseFeature = -> Fillet
  MirrorPlane = -> YZ_Plane020
  Originals = -> [Fillet]
FEATURE [PartDesign::Pocket] Pocket051
  BaseFeature = -> Mirrored022
  Direction = (0,1,-2e-16)
  Length = 5
  Length2 = 5
  Midplane = true
  Profile = -> Sketch083
  ReferenceAxis = -> Sketch083 [N_Axis]
  Type = 1
FEATURE [PartDesign::PolarPattern] PolarPattern013
  Angle = 90
  Axis = -> X_Axis020
  BaseFeature = -> Pocket051
  Occurrences = 2
  Originals = -> [Pocket051]
FEATURE [PartDesign::Body] Body_2  label="Body_2_material_0.50ansi"
  Group = -> [LCS_0005,Sketch082,BaseBend006,Local_CS014,DatumPlane013,Sketch083,Fillet,Mirrored022,Pocket051,PolarPattern013]
  Origin = -> Origin020
  Tip = -> Mirrored022
FEATURE [Sketcher::SketchObject] Sketch084
  ExternalGeometry = -> [Binder012]
  FullyConstrained = false
  MapMode = 5
  Placement = pos=(0,0,0) rot=(0.57735,0.57735,0.57735;2.0944rad)
  Support = -> [YZ_Plane015]
  expr: Constraints[10] = (BaseBend005.length / 2 - <<top>>.cover_length) * 2
  sketch-geometry (5):
    g0: LineSegment StartX=-20.8 StartY=-69.0964 StartZ=0 EndX=-20.8 EndY=-18.63 EndZ=0
    g1: LineSegment StartX=-20.8 StartY=-18.63 StartZ=0 EndX=20.8 EndY=-18.63 EndZ=0
    g2: LineSegment StartX=20.8 StartY=-18.63 StartZ=0 EndX=20.8 EndY=-69.0964 EndZ=0
    g3: LineSegment StartX=20.8 StartY=-69.0964 StartZ=0 EndX=-20.8 EndY=-69.0964 EndZ=0
    g4: GeomPoint X=0 Y=-43.8632 Z=0
  constraints (12):
    c: Coincident(g0,g1)
    c: Coincident(g1,g2)
    c: Coincident(g2,g3)
    c: Coincident(g3,g0)
    c: Horizontal(g1)
    c: Horizontal(g3)
    c: Vertical(g0)
    c: Vertical(g2)
    c: Symmetric(g1,g0,g4)
    c: PointOnObject(g4,g-2)
    c: DistanceX(g0,g1) = 41.6
    c: Horizontal(g1,g-3)
FEATURE [PartDesign::Pocket] Pocket052
  BaseFeature = -> Mirrored021
  Direction = (-1,2e-16,-3e-16)
  Length = 5
  Length2 = 5
  Midplane = true
  Profile = -> Sketch084
  ReferenceAxis = -> Sketch084 [N_Axis]
  Type = 1
FEATURE [PartDesign::Mirrored] Mirrored018
  BaseFeature = -> Pocket052
  MirrorPlane = -> Sketch080 [V_Axis]
  Originals = -> [Pad012]
  Refine = true
FEATURE [PartDesign::Body] top  label="top_material_0.50ansi"
  Group = -> [LCS_0003,Sketch072,BaseBend005,Binder012,Pocket045,DatumPlane012,MultiTransform008,Sketch073,Sketch080,Pad012,Sketch081,Binder017,Pocket050,Mirrored021,Sketch084,Pocket052,Mirrored018,Mirrored019,Mirrored020]
  Origin = -> Origin015
  Tip = -> Pocket052
FEATURE [PartDesign::CoordinateSystem] LCS_0006
  AttacherType = Attacher::AttachEngine3D
  MapMode = 2
  Support = -> [X_Axis021]
FEATURE [Sketcher::SketchObject] Sketch085
  FullyConstrained = true
  MapMode = 5
  Support = -> [XY_Plane021]
  expr: Constraints[17] = <<main>>.end_face_width - <<main>>.thickness * 2
  sketch-geometry (15):
    g0: LineSegment StartX=-46.141 StartY=-13.3605 StartZ=0 EndX=-11.5 EndY=6.63953 EndZ=0
    g1: LineSegment StartX=-11.5 StartY=6.63953 StartZ=0 EndX=-11.5 EndY=46.6395 EndZ=0
    g2: LineSegment StartX=-11.5 StartY=46.6395 StartZ=0 EndX=11.5 EndY=46.6395 EndZ=0
    g3: LineSegment StartX=11.5 StartY=46.6395 StartZ=0 EndX=11.5 EndY=6.63953 EndZ=0
    g4: LineSegment StartX=11.5 StartY=6.63953 StartZ=0 EndX=46.141 EndY=-13.3605 EndZ=0
    g5: LineSegment StartX=46.141 StartY=-13.3605 StartZ=0 EndX=34.641 EndY=-33.2791 EndZ=0
    g6: LineSegment StartX=34.641 StartY=-33.2791 StartZ=0 EndX=0 EndY=-13.2791 EndZ=0
    g7: LineSegment StartX=0 StartY=-13.2791 StartZ=0 EndX=-34.641 EndY=-33.2791 EndZ=0
    g8: LineSegment StartX=-34.641 StartY=-33.2791 StartZ=0 EndX=-46.141 EndY=-13.3605 EndZ=0
    g9: LineSegment StartX=0 StartY=-13.2791 StartZ=0 EndX=11.5 EndY=6.63953 EndZ=0
    g10: LineSegment StartX=11.5 StartY=6.63953 StartZ=0 EndX=-11.5 EndY=6.63953 EndZ=0
    g11: LineSegment StartX=-11.5 StartY=6.63953 StartZ=0 EndX=0 EndY=-13.2791 EndZ=0
    g12: LineSegment StartX=0 StartY=-13.2791 StartZ=0 EndX=0 EndY=0 EndZ=0
    g13: LineSegment StartX=0 StartY=0 StartZ=0 EndX=-11.5 EndY=6.63953 EndZ=0
    g14: LineSegment StartX=0 StartY=0 StartZ=0 EndX=11.5 EndY=6.63953 EndZ=0
  constraints (42):
    c: Coincident(g0,g1)
    c: Vertical(g1)
    c: Coincident(g1,g2)
    c: Horizontal(g2)
    c: Coincident(g2,g3)
    c: Vertical(g3)
    c: Coincident(g3,g4)
    c: Coincident(g4,g5)
    c: Coincident(g5,g6)
    c: PointOnObject(g6,g-2)
    c: Coincident(g6,g7)
    c: Coincident(g7,g8)
    c: Coincident(g8,g0)
    c: Perpendicular(g5,g6)
    c: Perpendicular(g4,g5)
    c: Perpendicular(g8,g7)
    c: Perpendicular(g0,g8)
    c: DistanceX(g1,g2) = 23
    c: Coincident(g6,g9)
    c: Coincident(g9,g3)
    c: Coincident(g9,g10)
    c: Coincident(g10,g0)
    c: Coincident(g10,g11)
    c: Coincident(g11,g9)
    c: Coincident(g6,g12)
    c: Coincident(g12,g-1)
    c: Coincident(g12,g13)
    c: Coincident(g13,g0)
    c: Coincident(g12,g14)
    c: Coincident(g14,g3)
    c: Equal(g9,g10)
    c: Equal(g10,g11)
    c: Equal(g12,g13)
    c: Equal(g13,g14)
    c: Equal(g4,g3)
    c: Equal(g0,g1)
    c: Perpendicular(g9,g4)
    c: Perpendicular(g0,g11)
    c: Angle(g-2,g4) = 1.0472
    c: DistanceY(g3,g3) = 40
    c: DistanceY(g12,g12) = 13.2791  'offset'
    c: DistanceY(g3) = 6.63953  'petal_offset'
FEATURE [PartDesign::FeaturePython] BaseBend007  # WARN: FeaturePython — macro-defined, semantics opaque (R4)
  BendSide = 1
  BendSketch = -> Sketch085
  MidPlane = false
  Reverse = false
  length = 100
  radius = 1
  thickness = 0.3
FEATURE [PartDesign::FeaturePython] Bend  # WARN: FeaturePython — macro-defined, semantics opaque (R4)
  AutoMiter = true
  BaseFeature = -> BaseBend007
  BendType = 1
  LengthList = [15]
  LengthSpec = 1
  ReliefFactor = 0.7
  UseReliefFactor = false
  angle = 90
  baseObject = -> BaseBend007 [Edge25,Edge22]
  bendAList = [90]
  extend1 = 0
  extend2 = 0
  gap1 = 0
  gap2 = 0
  invert = false
  kfactor = 0.5
  length = 15
  maxExtendDist = 5
  minGap = 2
  minReliefGap = 1
  miterangle1 = 0
  miterangle2 = 0
  offset = 0
  radius = 0.1
  reliefType = 0
  reliefd = 1
  reliefw = 0.8
  sketchflip = false
  sketchinvert = false
  unfold = false
  expr: radius = <<main>>.bend_r
FEATURE [Sketcher::SketchObject] Sketch086
  AttachmentOffset = pos=(0,-13.2791,0) rot=(0,0,1;0rad)
  FullyConstrained = true
  MapMode = 5
  Placement = pos=(0,-13.2791,0) rot=(0,0,1;0rad)
  Support = -> [XY_Plane021]
  expr: .AttachmentOffset.Base.y = -Sketch085.Constraints.offset
  expr: Constraints[10] = <<main>>.bend_r + <<main>>.al_thickness
  sketch-geometry (4):
    g0: LineSegment StartX=0 StartY=0 StartZ=0 EndX=2.16506 EndY=-1.25 EndZ=0
    g1: LineSegment StartX=2.16506 StartY=-1.25 StartZ=0 EndX=2.36506 EndY=-0.90359 EndZ=0
    g2: LineSegment StartX=2.36506 StartY=-0.90359 StartZ=0 EndX=0 EndY=0.46188 EndZ=0
    g3: LineSegment StartX=0 StartY=0.46188 StartZ=0 EndX=0 EndY=0 EndZ=0
  constraints (11):
    c: Coincident(g-1,g0)
    c: Coincident(g0,g1)
    c: Coincident(g1,g2)
    c: PointOnObject(g2,g-2)
    c: Coincident(g2,g3)
    c: Coincident(g3,g0)
    c: Perpendicular(g1,g0)
    c: Perpendicular(g2,g1)
    c: Angle(g0,g-2) = 2.0944
    c: Distance(g0,g0) = 2.5
    c: Distance(g1) = 0.4
FEATURE [PartDesign::FeaturePython] Bend004  # WARN: FeaturePython — macro-defined, semantics opaque (R4)
  AutoMiter = true
  BaseFeature = -> Bend
  BendType = 1
  LengthList = [15]
  LengthSpec = 1
  ReliefFactor = 0.7
  UseReliefFactor = false
  angle = 90
  baseObject = -> Bend [Edge25,Edge24]
  bendAList = [90]
  extend1 = 0
  extend2 = 0
  gap1 = 0
  gap2 = 0
  invert = false
  kfactor = 0.5
  length = 15
  maxExtendDist = 5
  minGap = 2
  minReliefGap = 1
  miterangle1 = 0
  miterangle2 = 0
  offset = 0
  radius = 0.1
  reliefType = 0
  reliefd = 1
  reliefw = 0.8
  sketchflip = false
  sketchinvert = false
  unfold = false
  expr: length = Bend.length
  expr: minGap = Bend.minGap
  expr: radius = <<main>>.bend_r
FEATURE [PartDesign::FeaturePython] Bend005  # WARN: FeaturePython — macro-defined, semantics opaque (R4)
  AutoMiter = true
  BaseFeature = -> Bend004
  BendType = 1
  LengthList = [15]
  LengthSpec = 1
  ReliefFactor = 0.7
  UseReliefFactor = false
  angle = 90
  baseObject = -> Bend004 [Edge28,Edge27]
  bendAList = [90]
  extend1 = 0
  extend2 = 0
  gap1 = 0
  gap2 = 0
  invert = false
  kfactor = 0.5
  length = 15
  maxExtendDist = 5
  minGap = 2
  minReliefGap = 1
  miterangle1 = 0
  miterangle2 = 0
  offset = 0
  radius = 0.1
  reliefType = 0
  reliefd = 1
  reliefw = 0.8
  sketchflip = false
  sketchinvert = false
  unfold = false
  expr: length = Bend.length
  expr: minGap = Bend.minGap
  expr: radius = <<main>>.bend_r
FEATURE [PartDesign::Mirrored] Mirrored023
  MirrorPlane = -> Sketch086 [V_Axis]
FEATURE [PartDesign::PolarPattern] PolarPattern014
  Angle = 360
  Axis = -> Z_Axis021
  Occurrences = 3
FEATURE [Sketcher::SketchObject] Sketch087
  AttachmentOffset = pos=(8.63953,0,0) rot=(0,0,1;0rad)
  FullyConstrained = true
  MapMode = 5
  Placement = pos=(1.9e-15,8.63953,-1.9e-15) rot=(0.57735,0.57735,0.57735;2.0944rad)
  Support = -> [YZ_Plane021]
  expr: .AttachmentOffset.Base.x = Sketch085.Constraints.petal_offset + 2 mm
  expr: Constraints[7] = -Bend.length
  sketch-geometry (3):
    g0: LineSegment StartX=0 StartY=0 StartZ=0 EndX=8.66025 EndY=-15 EndZ=0
    g1: LineSegment StartX=8.66025 StartY=-15 StartZ=0 EndX=0 EndY=-15 EndZ=0
    g2: LineSegment StartX=0 StartY=-15 StartZ=0 EndX=0 EndY=0 EndZ=0
  constraints (8):
    c: Coincident(g-1,g0)
    c: Coincident(g0,g1)
    c: PointOnObject(g1,g-2)
    c: Horizontal(g1)
    c: Coincident(g1,g2)
    c: Coincident(g2,g0)
    c: Angle(g2,g0) = 0.523599
    c: DistanceY(g1) = -15
FEATURE [Sketcher::SketchObject] Sketch088
  AttachmentOffset = pos=(30,-7,0) rot=(0,0,1;0rad)
  FullyConstrained = true
  MapMode = 5
  Placement = pos=(8.2e-15,30,-7) rot=(0.57735,0.57735,0.57735;2.0944rad)
  Support = -> [YZ_Plane021]
  expr: Constraints[1] = <<main>>.rivet_d
  sketch-geometry (1):
    g0: Circle CenterX=0 CenterY=0 CenterZ=0 NormalX=0 NormalY=0 NormalZ=1 AngleXU=0 Radius=1.7
  constraints (2):
    c: Coincident(g0,g-1)
    c: Diameter(g0) = 3.4
FEATURE [PartDesign::CoordinateSystem] LCS_0007  label="bottom002"
  AttacherType = Attacher::AttachEngine3D
  MapMode = 2
  Support = -> [X_Axis022]
FEATURE [Sketcher::SketchObject] Sketch089
  FullyConstrained = true
  MapMode = 5
  Support = -> [XY_Plane022]
  expr: .Constraints.d = 789.34 mm + (45 mm - 41.3 mm) * 2 + 1 mm
  sketch-geometry (1):
    g0: Circle CenterX=0 CenterY=0 CenterZ=0 NormalX=0 NormalY=0 NormalZ=1 AngleXU=0 Radius=398.87
  constraints (2):
    c: Coincident(g0,g-1)
    c: Diameter(g0) = 797.74  'd'
FEATURE [PartDesign::Pad] Pad013
  Direction = (0,0,1)
  Length = 12
  Length2 = 10
  Profile = -> Sketch089
  ReferenceAxis = -> Sketch089 [N_Axis]
  Type = 0
FEATURE [Sketcher::SketchObject] Sketch090
  FullyConstrained = true
  MapMode = 5
  Support = -> [XY_Plane022]
  sketch-geometry (6):
    g0: Circle CenterX=34.56 CenterY=34.56 CenterZ=0 NormalX=0 NormalY=0 NormalZ=1 AngleXU=0 Radius=4.25
    g1: LineSegment StartX=0 StartY=34.56 StartZ=0 EndX=34.56 EndY=34.56 EndZ=0
    g2: LineSegment StartX=34.56 StartY=34.56 StartZ=0 EndX=34.56 EndY=0 EndZ=0
    g3: Circle CenterX=-34.56 CenterY=34.56 CenterZ=0 NormalX=0 NormalY=0 NormalZ=1 AngleXU=0 Radius=4.25
    g4: Circle CenterX=-34.56 CenterY=-34.56 CenterZ=0 NormalX=0 NormalY=0 NormalZ=1 AngleXU=0 Radius=4.25
    g5: Circle CenterX=34.56 CenterY=-34.56 CenterZ=0 NormalX=0 NormalY=0 NormalZ=1 AngleXU=0 Radius=4.25
  constraints (15):
    c: Diameter(g0) = 8.5
    c: DistanceX(g0) = 34.56
    c: PointOnObject(g1,g-2)
    c: Coincident(g1,g0)
    c: Horizontal(g1)
    c: Coincident(g1,g2)
    c: PointOnObject(g2,g-1)
    c: Vertical(g2)
    c: Equal(g2,g1)
    c: Equal(g0,g5)
    c: Equal(g5,g4)
    c: Equal(g4,g3)
    c: Symmetric(g0,g3,g-2)
    c: Symmetric(g0,g5,g-1)
    c: Symmetric(g0,g4,g-1)
FEATURE [PartDesign::Pocket] Pocket056
  BaseFeature = -> Pad013
  Direction = (0,0,-1)
  Length = 5
  Length2 = 5
  Midplane = true
  Profile = -> Sketch090
  ReferenceAxis = -> Sketch090 [N_Axis]
  Type = 1
FEATURE [Sketcher::SketchObject] Sketch091
  FullyConstrained = true
  MapMode = 5
  Support = -> [XY_Plane022]
  sketch-geometry (1):
    g0: Circle CenterX=0 CenterY=0 CenterZ=0 NormalX=0 NormalY=0 NormalZ=1 AngleXU=0 Radius=32.5
  constraints (2):
    c: Coincident(g0,g-1)
    c: Diameter(g0) = 65
FEATURE [PartDesign::Pocket] Pocket057
  BaseFeature = -> Pocket056
  Direction = (0,0,-1)
  Length = 5
  Length2 = 5
  Midplane = true
  Profile = -> Sketch091
  ReferenceAxis = -> Sketch091 [N_Axis]
  Type = 1
FEATURE [Sketcher::SketchObject] Sketch092
  AttachmentOffset = pos=(368.87,0,0) rot=(0,0,1;0rad)
  FullyConstrained = true
  MapMode = 5
  Placement = pos=(368.87,0,0) rot=(0,0,1;0rad)
  Support = -> [XY_Plane022]
  expr: .AttachmentOffset.Base.x = Sketch089.Constraints.d / 2 - 30 mm
  sketch-geometry (1):
    g0: Circle CenterX=0 CenterY=0 CenterZ=0 NormalX=0 NormalY=0 NormalZ=1 AngleXU=0 Radius=4.5
  constraints (2):
    c: Coincident(g0,g-1)
    c: Diameter(g0) = 9
FEATURE [PartDesign::Pocket] Pocket058
  BaseFeature = -> Pocket057
  Direction = (0,0,-1)
  Length = 5
  Length2 = 5
  Midplane = true
  Profile = -> Sketch092
  ReferenceAxis = -> Sketch092 [N_Axis]
  Type = 1
FEATURE [PartDesign::PolarPattern] PolarPattern016
  Angle = 360
  Axis = -> Z_Axis022
  BaseFeature = -> Pocket058
  Occurrences = 4
  Originals = -> [Pocket058]
FEATURE [Sketcher::SketchObject] Sketch093
  FullyConstrained = true
  MapMode = 5
  Support = -> [XY_Plane023]
  sketch-geometry (1):
    g0: Circle CenterX=0 CenterY=0 CenterZ=0 NormalX=0 NormalY=0 NormalZ=1 AngleXU=0 Radius=50
  constraints (2):
    c: Coincident(g0,g-1)
    c: Diameter(g0) = 100
FEATURE [PartDesign::Pad] Pad014
  Direction = (0,0,1)
  Length = 65
  Length2 = 10
  Profile = -> Sketch093
  ReferenceAxis = -> Sketch093 [N_Axis]
  Type = 0
FEATURE [PartDesign::CoordinateSystem] Local_CS015  label="top001"
  AttacherType = Attacher::AttachEngine3D
  AttachmentOffset = pos=(0,0,65) rot=(0,0,1;0rad)
  MapMode = 5
  Placement = pos=(0,0,65) rot=(0,0,1;0rad)
  Support = -> [XY_Plane023]
  expr: .AttachmentOffset.Base.z = Pad014.Length
FEATURE [PartDesign::CoordinateSystem] Local_CS016  label="top002"
  AttacherType = Attacher::AttachEngine3D
  AttachmentOffset = pos=(0,0,12) rot=(0,0,1;0rad)
  MapMode = 5
  Placement = pos=(0,0,12) rot=(0,0,1;0rad)
  Support = -> [XY_Plane022]
  expr: .AttachmentOffset.Base.z = Pad013.Length
FEATURE [PartDesign::CoordinateSystem] Local_CS017
  AttacherType = Attacher::AttachEngine3D
  AttachmentOffset = pos=(0,0,3) rot=(0,0,1;0rad)
  MapMode = 5
  Placement = pos=(0,0,3) rot=(0,0,1;0rad)
  Support = -> [XY_Plane018]
  expr: .AttachmentOffset.Base.z = <<main>>.thickness
FEATURE [PartDesign::Body] basement_composite
  Group = -> [LCS_0004,Sketch079,Pad011,Binder015,Pocket048,Binder016,Hole,MultiTransform009,Mirrored017,PolarPattern011,PolarPattern012,Local_CS017]
  Origin = -> Origin018
  Tip = -> PolarPattern012
FEATURE [PartDesign::CoordinateSystem] Local_CS018  label="bottom001"
  AttacherType = Attacher::AttachEngine3D
  MapMode = 5
  Support = -> [XY_Plane023]
FEATURE [PartDesign::Body] Body003009  label="hub2108"
  Group = -> [Sketch093,Pad014,Local_CS015,Local_CS018]
  Origin = -> Origin023
  Tip = -> Pad014
FEATURE [PartDesign::CoordinateSystem] Local_CS019
  AttacherType = Attacher::AttachEngine3D
  AttachmentOffset = pos=(0,398.87,0) rot=(0,0,1;1.5708rad)
  MapMode = 5
  Placement = pos=(0,398.87,12) rot=(0,0,1;1.5708rad)
  Support = -> [Local_CS016]
  expr: .AttachmentOffset.Base.y = Sketch089.Constraints.d / 2
FEATURE [PartDesign::Body] Body_4
  Group = -> [LCS_0007,Sketch089,Pad013,Sketch090,Pocket056,Sketch091,Pocket057,Sketch092,Pocket058,PolarPattern016,Local_CS016,Local_CS019]
  Origin = -> Origin022
  Tip = -> PolarPattern016
FEATURE [PartDesign::CoordinateSystem] LCS_0008
  AttacherType = Attacher::AttachEngine3D
  MapMode = 2
  Support = -> [X_Axis026]
FEATURE [Sketcher::SketchObject] Sketch095
  FullyConstrained = true
  MapMode = 5
  Placement = pos=(0,0,0) rot=(0.57735,0.57735,0.57735;2.0944rad)
  Support = -> [YZ_Plane026]
  sketch-geometry (2):
    g0: LineSegment StartX=18 StartY=0 StartZ=0 EndX=0 EndY=0 EndZ=0
    g1: LineSegment StartX=0 StartY=0 StartZ=0 EndX=0 EndY=18 EndZ=0
  constraints (6):
    c: PointOnObject(g0,g-1)
    c: Coincident(g0,g-1)
    c: Coincident(g1,g0)
    c: PointOnObject(g1,g-2)
    c: Equal(g0,g1)
    c: Distance(g0) = 18  'width'
FEATURE [PartDesign::FeaturePython] BaseBend009  # WARN: FeaturePython — macro-defined, semantics opaque (R4)
  BendSide = 0
  BendSketch = -> Sketch095
  MidPlane = true
  Reverse = false
  length = 390
  radius = 2
  thickness = 0.5
FEATURE [Sketcher::SketchObject] Sketch096
  AttachmentOffset = pos=(195,18,0) rot=(0,0,1;0rad)
  FullyConstrained = true
  MapMode = 5
  Placement = pos=(195,18,0) rot=(0,0,1;0rad)
  Support = -> [XY_Plane026]
  expr: .AttachmentOffset.Base.x = BaseBend009.length / 2
  expr: .AttachmentOffset.Base.y = Sketch095.Constraints.width
  sketch-geometry (3):
    g0: ArcOfCircle CenterX=-3 CenterY=-3 CenterZ=0 NormalX=0 NormalY=0 NormalZ=1 AngleXU=0 Radius=3 StartAngle=1.46029e-11 EndAngle=1.5708
    g1: LineSegment StartX=-3 StartY=-2.355e-12 StartZ=0 EndX=0 EndY=0 EndZ=0
    g2: LineSegment StartX=0 StartY=0 StartZ=0 EndX=-2.355e-12 EndY=-3 EndZ=0
  constraints (7):
    c: PointOnObject(g0,g-2)
    c: PointOnObject(g0,g-1)
    c: Coincident(g1,g-1)
    c: Coincident(g2,g1)
    c: Tangent(g2,g0) = 1.5708
    c: Tangent(g1,g0) = 1.5708
    c: Diameter(g0) = 6
FEATURE [PartDesign::Pocket] Pocket063
  BaseFeature = -> BaseBend009
  Direction = (0,0,-1)
  Length = 5
  Length2 = 5
  Midplane = true
  Profile = -> Sketch096
  ReferenceAxis = -> Sketch096 [N_Axis]
  Type = 1
FEATURE [PartDesign::Mirrored] Mirrored028
  MirrorPlane = -> YZ_Plane026
FEATURE [PartDesign::PolarPattern] PolarPattern017
  Angle = 90
  Axis = -> X_Axis026
  Occurrences = 2
FEATURE [PartDesign::MultiTransform] MultiTransform013
  BaseFeature = -> Pocket063
  Originals = -> [Pocket063]
  Transformations = -> [Mirrored028,PolarPattern017]
FEATURE [Sketcher::SketchObject] Sketch097
  AttachmentOffset = pos=(0,13,0) rot=(0,0,1;0rad)
  FullyConstrained = true
  MapMode = 5
  Placement = pos=(0,13,0) rot=(0,0,1;0rad)
  Support = -> [XY_Plane026]
  expr: .AttachmentOffset.Base.y = 12.5 mm + BaseBend009.thickness
  expr: Constraints[7] = <<main>>.rivet_d
  sketch-geometry (3):
    g0: Circle CenterX=-180 CenterY=0 CenterZ=0 NormalX=0 NormalY=0 NormalZ=1 AngleXU=0 Radius=1.7
    g1: Circle CenterX=0 CenterY=0 CenterZ=0 NormalX=0 NormalY=0 NormalZ=1 AngleXU=0 Radius=1.7
    g2: Circle CenterX=180 CenterY=0 CenterZ=0 NormalX=0 NormalY=0 NormalZ=1 AngleXU=0 Radius=1.7
  constraints (8):
    c: Symmetric(g0,g2,g1)
    c: PointOnObject(g0,g-1)
    c: PointOnObject(g1,g-2)
    c: PointOnObject(g1,g-1)
    c: DistanceX(g0,g2) = 360
    c: Equal(g2,g1)
    c: Equal(g2,g0)
    c: Diameter(g2) = 3.4
FEATURE [PartDesign::Pocket] Pocket064
  BaseFeature = -> MultiTransform013
  Direction = (0,0,-1)
  Length = 5
  Length2 = 5
  Midplane = true
  Profile = -> Sketch097
  ReferenceAxis = -> Sketch097 [N_Axis]
  Type = 1
FEATURE [PartDesign::PolarPattern] PolarPattern018
  Angle = 90
  Axis = -> X_Axis026
  BaseFeature = -> Pocket064
  Occurrences = 2
  Originals = -> [Pocket064]
FEATURE [PartDesign::Body] Body_5  label="ugol_big_material_0.30ansi"
  Group = -> [LCS_0008,Sketch095,BaseBend009,Sketch096,Pocket063,MultiTransform013,Mirrored028,PolarPattern017,Sketch097,Pocket064,PolarPattern018]
  Origin = -> Origin026
  Tip = -> PolarPattern018
FEATURE [Sketcher::SketchObject] Sketch099
  AttachmentOffset = pos=(0,-126.625,0) rot=(0,0,1;0rad)
  FullyConstrained = true
  MapMode = 5
  Placement = pos=(0,-126.625,0) rot=(0,0,1;0rad)
  Support = -> [XY_Plane003]
  expr: .AttachmentOffset.Base.y = -(BaseBend001.length / 2 - 5 mm)
  sketch-geometry (1):
    g0: Circle CenterX=0 CenterY=0 CenterZ=0 NormalX=0 NormalY=0 NormalZ=1 AngleXU=0 Radius=1.65
  constraints (2):
    c: Coincident(g0,g-1)
    c: Diameter(g0) = 3.3
FEATURE [PartDesign::Pocket] Pocket065
  BaseFeature = -> Pocket047
  Direction = (0,0,-1)
  Length = 5
  Length2 = 5
  Midplane = true
  Profile = -> Sketch099
  ReferenceAxis = -> Sketch099 [N_Axis]
  Type = 1
FEATURE [PartDesign::Body] Body001  label="gutter_top_material_0.50ansi"
  Group = -> [Sketch009,BaseBend001,Sketch010,Pocket009,Local_CS005,DatumPlane004,Sketch037,Local_CS006,ShapeBinder,DatumPlane005,Sketch_2,Sketch076,Pocket010,Sketch077,Binder014,Pocket011,MultiTransform003,Mirrored002,LinearPattern004,LinearPattern005,DatumLine001,MultiTransform004,Mirrored003,LinearPattern006,LinearPattern007,DatumPlane006,Sketch038,Binder013,Pocket012,Local_CS008,Pocket046,Sketch078,+3 more]
  Origin = -> Origin003
  Tip = -> Pocket065
FEATURE [PartDesign::Fillet] Fillet001
  Base = -> Bend005 [Edge8]
  BaseFeature = -> Bend005
  Radius = 3
  SupportTransform = false
  UseAllEdges = false
FEATURE [Sketcher::SketchObject] Sketch100
  FullyConstrained = true
  MapMode = 5
  Support = -> [XY_Plane021]
  sketch-geometry (1):
    g0: Circle CenterX=0 CenterY=0 CenterZ=0 NormalX=0 NormalY=0 NormalZ=1 AngleXU=0 Radius=7
  constraints (2):
    c: Coincident(g0,g-1)
    c: Diameter(g0) = 14
FEATURE [PartDesign::Pocket] Pocket066
  BaseFeature = -> Fillet001
  Direction = (0,0,-1)
  Length = 5
  Length2 = 5
  Midplane = true
  Profile = -> Sketch100
  ReferenceAxis = -> Sketch100 [N_Axis]
  Type = 1
FEATURE [PartDesign::Pocket] Pocket053
  BaseFeature = -> Pocket066
  Direction = (0,0,-1)
  Length = 5
  Length2 = 5
  Midplane = true
  Profile = -> Sketch086
  ReferenceAxis = -> Sketch086 [N_Axis]
  Type = 1
FEATURE [PartDesign::MultiTransform] MultiTransform010
  BaseFeature = -> Pocket053
  Originals = -> [Pocket053,Fillet001]
  Transformations = -> [Mirrored023,PolarPattern014]
FEATURE [PartDesign::Pocket] Pocket054
  BaseFeature = -> MultiTransform010
  Direction = (-1,2e-16,-3e-16)
  Length = 23
  Length2 = 5
  Midplane = true
  Profile = -> Sketch087
  ReferenceAxis = -> Sketch087 [N_Axis]
  Type = 0
  expr: Length = <<main>>.end_face_width - <<main>>.thickness * 2
FEATURE [PartDesign::Pocket] Pocket055
  BaseFeature = -> Pocket054
  Direction = (-1,2e-16,-3e-16)
  Length = 5
  Length2 = 5
  Midplane = true
  Profile = -> Sketch088
  ReferenceAxis = -> Sketch088 [N_Axis]
  Type = 1
FEATURE [PartDesign::PolarPattern] PolarPattern015
  Angle = 360
  Axis = -> Z_Axis021
  BaseFeature = -> Pocket055
  Occurrences = 3
  Originals = -> [Pocket054,Pocket055]
  Refine = true
FEATURE [PartDesign::Body] Body_3  label="top_amplifier_material_0.50ansi"
  Group = -> [LCS_0006,Sketch085,BaseBend007,Bend,Sketch086,Bend004,Bend005,Fillet001,Sketch100,Pocket066,Pocket053,MultiTransform010,Mirrored023,PolarPattern014,Sketch087,Pocket054,Sketch088,Pocket055,PolarPattern015]
  Origin = -> Origin021
  Tip = -> Pocket066
FEATURE [App::DocumentObjectGroup] Parts
  Group = -> [Body,module_body,Body001,Body003,Body003004,Body003005,Body003006,Body003003,Body003007,Body003008,basement_stainless_steel,top,basement_composite,Body_2,Body_3,Body_4,Body003009,Body_5]
